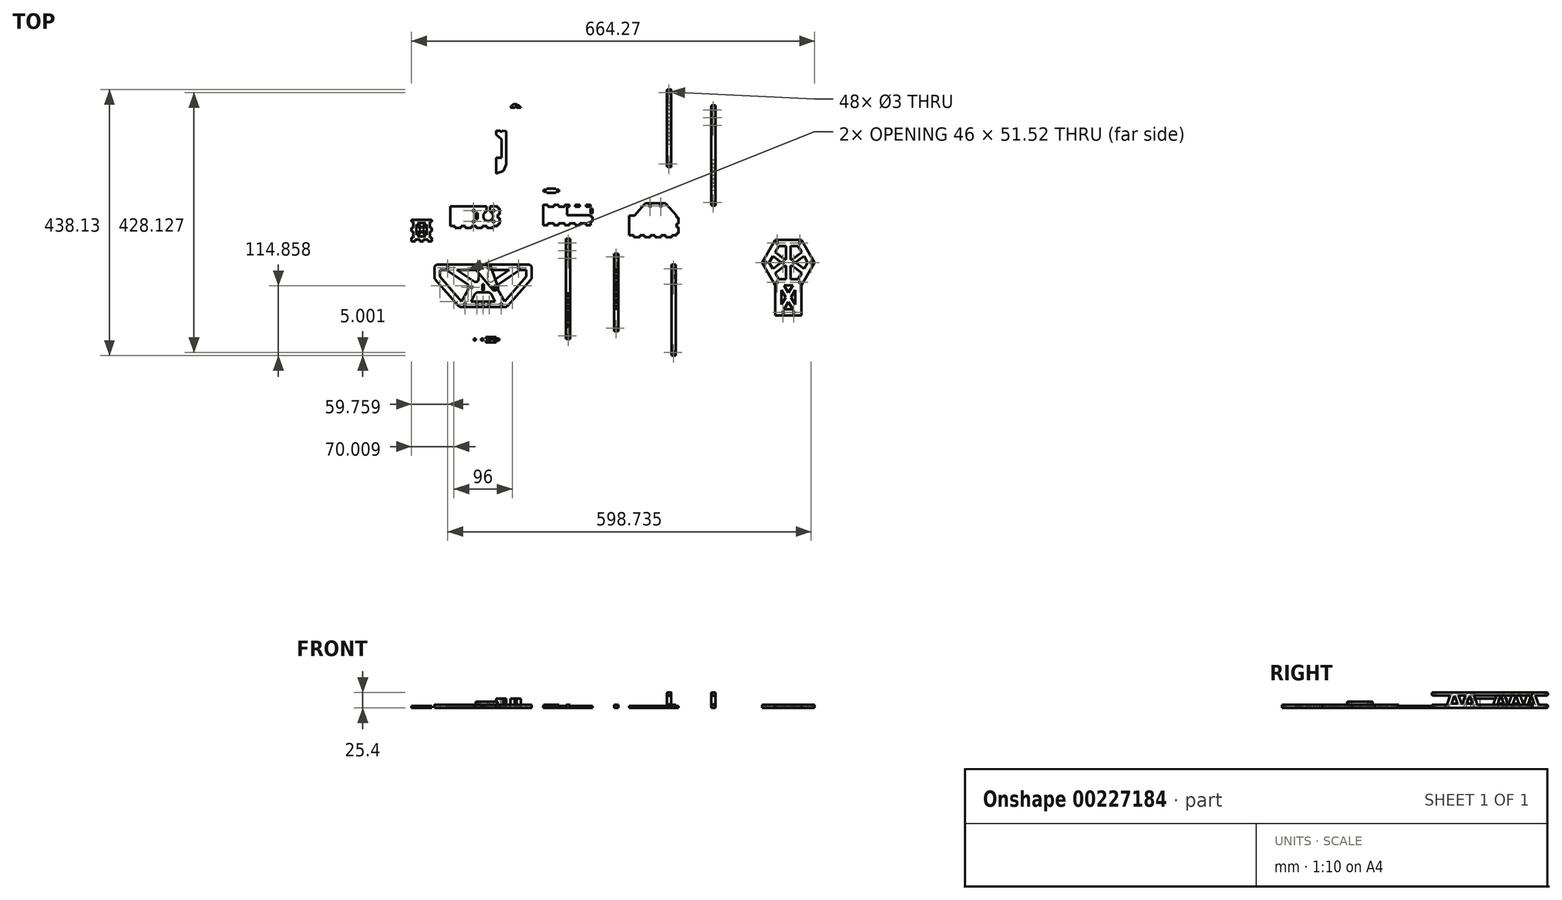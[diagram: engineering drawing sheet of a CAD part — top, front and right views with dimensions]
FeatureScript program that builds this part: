
annotation { "Feature Type Name" : "Feature", "Feature Type Description" : "" }
export const myFeature = defineFeature(function(context is Context, id is Id, definition is map)
    precondition{}
    {
        {
            var Q0;
            Q0=qCreatedBy(makeId("Top.planeOp"),FACE);
            var sketch = newSketch(context, id + "F0", { "sketchPlane" : qUnion([Q0])});
            skLineSegment(sketch, "E0.bottom", {"start": v(-33.91, 60.52) * mm, "end": v(-193.91, 60.52) * mm});
            skLineSegment(sketch, "E0.top", {"start": v(-33.91, 51.52) * mm, "end": v(-193.91, 51.52) * mm});
            skLineSegment(sketch, "E0.left", {"start": v(-33.91, 60.52) * mm, "end": v(-33.91, 51.52) * mm});
            skLineSegment(sketch, "E0.right", {"start": v(-193.91, 60.52) * mm, "end": v(-193.91, 51.52) * mm});
            skCircle(sketch, "E1", {"center": v(-172.16, 55.57) * mm, "radius": 1.5 * mm});
            skLineSegment(sketch, "E2.bottom", {"start": v(-88.91, 27.77) * mm, "end": v(-138.91, 27.77) * mm});
            skLineSegment(sketch, "E2.top", {"start": v(-88.91, 18.77) * mm, "end": v(-138.91, 18.77) * mm});
            skLineSegment(sketch, "E2.left", {"start": v(-88.91, 27.77) * mm, "end": v(-88.91, 18.77) * mm});
            skLineSegment(sketch, "E2.right", {"start": v(-138.91, 27.77) * mm, "end": v(-138.91, 18.77) * mm});
            skPoint(sketch, "E2.centerSnap0", {"position": v(-113.91, 51.52) * mm});
            skLineSegment(sketch, "E3", {"start": v(-121.41, 27.77) * mm, "end": v(-121.41, 51.52) * mm});
            skLineSegment(sketch, "E4", {"start": v(-113.91, 60.52) * mm, "end": v(-113.91, 18.77) * mm, "construction": true});
            skLineSegment(sketch, "E5.MirrorCS", {"start": v(-106.41, 27.77) * mm, "end": v(-106.41, 51.52) * mm});
            skPoint(sketch, "E6.centerSnap0", {"position": v(-138.91, 23.27) * mm});
            skCircle(sketch, "E7.MirrorC", {"center": v(-133.04, 23.27) * mm, "radius": 1.5 * mm});
            skCircle(sketch, "E8", {"center": v(-55.66, 55.57) * mm, "radius": 1.5 * mm});
            skLineSegment(sketch, "E9", {"start": v(-172.16, 55.57) * mm, "end": v(-55.66, 55.57) * mm, "construction": true});
            skLineSegment(sketch, "E10.bottom", {"start": v(-86.41, 0) * mm, "end": v(-141.41, 0) * mm});
            skLineSegment(sketch, "E10.top", {"start": v(-86.41, -9) * mm, "end": v(-141.41, -9) * mm});
            skLineSegment(sketch, "E10.left", {"start": v(-86.41, 0) * mm, "end": v(-86.41, -9) * mm});
            skLineSegment(sketch, "E10.right", {"start": v(-141.41, 0) * mm, "end": v(-141.41, -9) * mm});
            skLineSegment(sketch, "E11", {"start": v(-121.41, 18.77) * mm, "end": v(-121.41, 0) * mm});
            skLineSegment(sketch, "E12", {"start": v(-106.41, 18.77) * mm, "end": v(-106.41, 0) * mm});
            skCircle(sketch, "E13", {"center": v(-143.91, -4.5) * mm, "radius": 1.5 * mm});
            skPoint(sketch, "E13.centerSnap0", {"position": v(-141.41, -4.5) * mm});
            skLineSegment(sketch, "E14", {"start": v(-113.91, 18.77) * mm, "end": v(-113.91, -9) * mm});
            skCircle(sketch, "E15.MirrorC", {"center": v(-83.91, -4.5) * mm, "radius": 1.5 * mm});
            skLineSegment(sketch, "E16.bottom", {"start": v(22.73, 88.38) * mm, "end": v(29.73, 88.38) * mm});
            skLineSegment(sketch, "E16.top", {"start": v(22.73, -61.62) * mm, "end": v(29.73, -61.62) * mm});
            skLineSegment(sketch, "E16.left", {"start": v(22.73, 88.38) * mm, "end": v(22.73, -61.62) * mm});
            skLineSegment(sketch, "E16.right", {"start": v(29.73, 88.38) * mm, "end": v(29.73, -61.62) * mm});
            skCircle(sketch, "E17", {"center": v(26.23, 83.38) * mm, "radius": 1.5 * mm});
            skPoint(sketch, "E17.centerSnap0", {"position": v(26.23, 88.38) * mm});
            skLineSegment(sketch, "E18", {"start": v(22.73, 88.38) * mm, "end": v(22.73, 103.38) * mm});
            skLineSegment(sketch, "E19", {"start": v(22.73, 103.38) * mm, "end": v(29.73, 103.38) * mm});
            skLineSegment(sketch, "E20", {"start": v(29.73, 103.38) * mm, "end": v(29.73, 88.38) * mm});
            skCircle(sketch, "E21", {"center": v(26.23, 96.08) * mm, "radius": 1.5 * mm});
            skCircle(sketch, "E22", {"center": v(26.23, 70.68) * mm, "radius": 1.5 * mm});
            skLineSegment(sketch, "E23", {"start": v(26.23, 83.38) * mm, "end": v(26.23, 70.68) * mm});
            skCircle(sketch, "E24", {"center": v(26.23, -56.62) * mm, "radius": 1.5 * mm});
            skPoint(sketch, "E24.centerSnap0", {"position": v(26.23, -61.62) * mm});
            skLineSegment(sketch, "E25.bottom", {"start": v(101.72, 78.28) * mm, "end": v(108.72, 78.28) * mm});
            skLineSegment(sketch, "E25.top", {"start": v(101.72, -49.22) * mm, "end": v(108.72, -49.22) * mm});
            skLineSegment(sketch, "E25.left", {"start": v(101.72, 78.28) * mm, "end": v(101.72, -49.22) * mm});
            skLineSegment(sketch, "E25.right", {"start": v(108.72, 78.28) * mm, "end": v(108.72, -49.22) * mm});
            skCircle(sketch, "E26", {"center": v(105.22, 73.28) * mm, "radius": 1.5 * mm});
            skPoint(sketch, "E26.centerSnap0", {"position": v(105.22, 78.28) * mm});
            skCircle(sketch, "E27", {"center": v(105.22, -44.22) * mm, "radius": 1.5 * mm});
            skPoint(sketch, "E27.centerSnap0", {"position": v(105.22, -49.22) * mm});
            skLineSegment(sketch, "E28", {"start": v(-141.41, -9) * mm, "end": v(-193.91, 51.52) * mm});
            skLineSegment(sketch, "E29", {"start": v(-153.09, -9) * mm, "end": v(-141.41, -9) * mm});
            skLineSegment(sketch, "E30", {"start": v(-141.41, 0) * mm, "end": v(-149.22, 0) * mm});
            skLineSegment(sketch, "E31.MirrorCS", {"start": v(-86.41, -9) * mm, "end": v(-33.91, 51.52) * mm});
            skLineSegment(sketch, "E32.MirrorCS", {"start": v(-74.74, -9) * mm, "end": v(-86.41, -9) * mm});
            skLineSegment(sketch, "E33.MirrorCS", {"start": v(-86.41, 0) * mm, "end": v(-78.6, 0) * mm});
            skLineSegment(sketch, "E34", {"start": v(-88.91, 18.77) * mm, "end": v(-78.6, 0) * mm});
            skLineSegment(sketch, "E35", {"start": v(-99.18, 18.77) * mm, "end": v(-88.87, 0) * mm});
            skLineSegment(sketch, "E36.MirrorCS", {"start": v(-128.64, 18.77) * mm, "end": v(-138.95, 0) * mm});
            skLineSegment(sketch, "E37.MirrorCS", {"start": v(-138.91, 18.77) * mm, "end": v(-149.22, 0) * mm});
            skLineSegment(sketch, "E38", {"start": v(-42.91, 51.52) * mm, "end": v(-42.91, 41.14) * mm});
            skLineSegment(sketch, "E39", {"start": v(-33.91, 51.52) * mm, "end": v(-33.91, 37.39) * mm});
            skLineSegment(sketch, "E40", {"start": v(-33.91, 37.39) * mm, "end": v(-74.74, -9) * mm});
            skLineSegment(sketch, "E41.MirrorCS", {"start": v(-193.91, 37.39) * mm, "end": v(-153.09, -9) * mm});
            skLineSegment(sketch, "E42.MirrorCS", {"start": v(-193.91, 51.52) * mm, "end": v(-193.91, 37.39) * mm});
            skLineSegment(sketch, "E43.MirrorCS", {"start": v(-184.91, 51.52) * mm, "end": v(-184.91, 41.14) * mm});
            skLineSegment(sketch, "E44", {"start": v(-138.91, 27.77) * mm, "end": v(-174.34, 51.52) * mm});
            skLineSegment(sketch, "E45.MirrorCS", {"start": v(-88.91, 27.77) * mm, "end": v(-53.49, 51.52) * mm});
            skLineSegment(sketch, "E46", {"start": v(-149.22, 0) * mm, "end": v(-149.22, -9) * mm});
            skLineSegment(sketch, "E47", {"start": v(-138.6, -9) * mm, "end": v(-138.6, 0) * mm});
            skLineSegment(sketch, "E48", {"start": v(-138.6, 0) * mm, "end": v(-128.3, 18.77) * mm});
            skLineSegment(sketch, "E49.MirrorCS", {"start": v(-89.22, 0) * mm, "end": v(-99.53, 18.77) * mm});
            skLineSegment(sketch, "E50", {"start": v(-89.22, 0) * mm, "end": v(-89.22, -9) * mm});
            skLineSegment(sketch, "E51", {"start": v(-138.6, -9) * mm, "end": v(-123.35, 18.77) * mm});
            skLineSegment(sketch, "E52.MirrorCS", {"start": v(-89.22, -9) * mm, "end": v(-104.47, 18.77) * mm});
            skPoint(sketch, "E53.endSnap0", {"position": v(-156.62, 39.64) * mm});
            skLineSegment(sketch, "E54", {"start": v(-121.41, 27.77) * mm, "end": v(-156.84, 51.52) * mm});
            skLineSegment(sketch, "E55.MirrorCS", {"start": v(-106.41, 27.77) * mm, "end": v(-70.99, 51.52) * mm});
            skLineSegment(sketch, "E56.bottom", {"start": v(196.57, 45.9) * mm, "end": v(203.57, 45.9) * mm});
            skLineSegment(sketch, "E56.top", {"start": v(196.57, -89.1) * mm, "end": v(203.57, -89.1) * mm});
            skLineSegment(sketch, "E56.left", {"start": v(196.57, 45.9) * mm, "end": v(196.57, -89.1) * mm});
            skLineSegment(sketch, "E56.right", {"start": v(203.57, 45.9) * mm, "end": v(203.57, -89.1) * mm});
            skCircle(sketch, "E57", {"center": v(200.07, 40.9) * mm, "radius": 2.1 * mm});
            skPoint(sketch, "E57.centerSnap0", {"position": v(200.07, 45.9) * mm});
            skLineSegment(sketch, "E58", {"start": v(196.57, 45.9) * mm, "end": v(196.57, 60.9) * mm});
            skLineSegment(sketch, "E59", {"start": v(196.57, 60.9) * mm, "end": v(203.57, 60.9) * mm});
            skLineSegment(sketch, "E60", {"start": v(203.57, 60.9) * mm, "end": v(203.57, 45.9) * mm});
            skCircle(sketch, "E61", {"center": v(200.07, 53.6) * mm, "radius": 1.5 * mm});
            skCircle(sketch, "E62", {"center": v(200.07, 28.2) * mm, "radius": 1.5 * mm});
            skLineSegment(sketch, "E63", {"start": v(200.07, 40.9) * mm, "end": v(200.07, 28.2) * mm});
            skCircle(sketch, "E64", {"center": v(200.07, -84.1) * mm, "radius": 1.5 * mm});
            skPoint(sketch, "E64.centerSnap0", {"position": v(200.07, -89.1) * mm});
            skLineSegment(sketch, "E65.bottom", {"start": v(201.67, 42.5) * mm, "end": v(198.47, 42.5) * mm});
            skLineSegment(sketch, "E65.top", {"start": v(201.67, 39.3) * mm, "end": v(198.47, 39.3) * mm});
            skLineSegment(sketch, "E65.left", {"start": v(201.67, 42.5) * mm, "end": v(201.67, 39.3) * mm});
            skLineSegment(sketch, "E65.right", {"start": v(198.47, 42.5) * mm, "end": v(198.47, 39.3) * mm});
            skCircle(sketch, "E66", {"center": v(-105.16, 55.57) * mm, "radius": 1.5 * mm});
            skCircle(sketch, "E67.MirrorC", {"center": v(-122.66, 55.57) * mm, "radius": 1.5 * mm});
            skLineSegment(sketch, "E68", {"start": v(-127.38, 31.77) * mm, "end": v(-100.45, 31.77) * mm});
            skLineSegment(sketch, "E69.right", {"start": v(-137.03, 156.47) * mm, "end": v(-137.03, 124.47) * mm, "construction": true});
            skCircle(sketch, "E70", {"center": v(-96.53, 149.47) * mm, "radius": 1.5 * mm});
            skLineSegment(sketch, "E71", {"start": v(-137.03, 156.47) * mm, "end": v(-138.03, 156.47) * mm});
            skLineSegment(sketch, "E72", {"start": v(-138.03, 156.47) * mm, "end": v(-138.03, 124.47) * mm, "construction": true});
            skLineSegment(sketch, "E73", {"start": v(-138.03, 124.47) * mm, "end": v(-137.03, 124.47) * mm});
            skLineSegment(sketch, "E74.MirrorCS", {"start": v(-90.03, 156.47) * mm, "end": v(-90.03, 124.47) * mm});
            skLineSegment(sketch, "E75.MirrorCS", {"start": v(-90.03, 153.47) * mm, "end": v(-86.86, 153.47) * mm});
            skLineSegment(sketch, "E76.MirrorCS", {"start": v(-86.86, 153.47) * mm, "end": v(-86.86, 143.47) * mm});
            skLineSegment(sketch, "E77.MirrorCS", {"start": v(-86.86, 143.47) * mm, "end": v(-90.03, 143.47) * mm});
            skLineSegment(sketch, "E78.MirrorCS", {"start": v(-86.86, 137.47) * mm, "end": v(-90.03, 137.47) * mm});
            skLineSegment(sketch, "E79.MirrorCS", {"start": v(-86.86, 127.47) * mm, "end": v(-86.86, 137.47) * mm});
            skLineSegment(sketch, "E80.MirrorCS", {"start": v(-90.03, 127.47) * mm, "end": v(-86.86, 127.47) * mm});
            skCircle(sketch, "E81", {"center": v(-105.53, 140.47) * mm, "radius": 8 * mm});
            skLineSegment(sketch, "E82", {"start": v(-138.03, 156.47) * mm, "end": v(-168.03, 156.47) * mm});
            skLineSegment(sketch, "E83", {"start": v(-168.03, 156.47) * mm, "end": v(-168.03, 124.47) * mm});
            skLineSegment(sketch, "E84", {"start": v(-168.03, 124.47) * mm, "end": v(-138.03, 124.47) * mm});
            skLineSegment(sketch, "E85", {"start": v(-160.43, 124.47) * mm, "end": v(-160.43, 121.3) * mm});
            skLineSegment(sketch, "E86", {"start": v(-160.43, 121.3) * mm, "end": v(-150.43, 121.3) * mm});
            skLineSegment(sketch, "E87", {"start": v(-150.43, 121.3) * mm, "end": v(-150.43, 124.47) * mm});
            skLineSegment(sketch, "E88", {"start": v(-142.83, 124.47) * mm, "end": v(-142.83, 121.3) * mm});
            skLineSegment(sketch, "E89", {"start": v(-142.83, 121.3) * mm, "end": v(-132.83, 121.3) * mm});
            skLineSegment(sketch, "E90", {"start": v(-132.83, 121.3) * mm, "end": v(-132.83, 124.47) * mm});
            skLineSegment(sketch, "E91", {"start": v(-125.23, 124.47) * mm, "end": v(-125.23, 121.3) * mm});
            skLineSegment(sketch, "E92", {"start": v(-125.23, 121.3) * mm, "end": v(-115.23, 121.3) * mm});
            skLineSegment(sketch, "E93", {"start": v(-115.23, 121.3) * mm, "end": v(-115.23, 124.47) * mm});
            skLineSegment(sketch, "E94", {"start": v(-107.63, 124.47) * mm, "end": v(-107.63, 121.3) * mm});
            skLineSegment(sketch, "E95", {"start": v(-107.63, 121.3) * mm, "end": v(-97.63, 121.3) * mm});
            skLineSegment(sketch, "E96", {"start": v(-97.63, 121.3) * mm, "end": v(-97.63, 124.47) * mm});
            skCircle(sketch, "E97", {"center": v(-96.53, 149.47) * mm, "radius": 4 * mm, "construction": true});
            skCircle(sketch, "E98", {"center": v(-96.53, 131.57) * mm, "radius": 1.5 * mm});
            skCircle(sketch, "E99", {"center": v(-96.53, 131.57) * mm, "radius": 4 * mm, "construction": true});
            skLineSegment(sketch, "E100", {"start": v(-96.53, 153.47) * mm, "end": v(-96.53, 127.57) * mm, "construction": true});
            skCircle(sketch, "E101", {"center": v(-129.63, 149.47) * mm, "radius": 1.5 * mm});
            skCircle(sketch, "E102", {"center": v(-129.63, 149.47) * mm, "radius": 4 * mm, "construction": true});
            skLineSegment(sketch, "E103", {"start": v(-92.53, 149.47) * mm, "end": v(-133.63, 149.47) * mm, "construction": true});
            skCircle(sketch, "E104", {"center": v(-129.63, 131.57) * mm, "radius": 4 * mm, "construction": true});
            skCircle(sketch, "E105", {"center": v(-129.63, 131.57) * mm, "radius": 1.5 * mm});
            skLineSegment(sketch, "E106", {"start": v(-129.63, 153.47) * mm, "end": v(-129.63, 127.57) * mm, "construction": true});
            skLineSegment(sketch, "E107", {"start": v(-133.63, 131.57) * mm, "end": v(-92.53, 131.57) * mm, "construction": true});
            skCircle(sketch, "E108", {"center": v(-105.53, 140.47) * mm, "radius": 3 * mm});
            skLineSegment(sketch, "E109", {"start": v(-102.53, 140.47) * mm, "end": v(-102.53, 156.47) * mm});
            skLineSegment(sketch, "E110", {"start": v(-108.53, 140.47) * mm, "end": v(-108.53, 156.47) * mm});
            skLineSegment(sketch, "E111.bottom", {"start": v(63.2, 155.65) * mm, "end": v(-14.8, 155.65) * mm});
            skLineSegment(sketch, "E111.top", {"start": v(63.2, 128.65) * mm, "end": v(-14.8, 128.65) * mm});
            skLineSegment(sketch, "E111.left", {"start": v(63.2, 155.65) * mm, "end": v(63.2, 128.65) * mm});
            skPoint(sketch, "E111.middle", {"position": v(24.2, 142.15) * mm});
            skLineSegment(sketch, "E112.bottom", {"start": v(63.2, 152.65) * mm, "end": v(66.38, 152.65) * mm});
            skLineSegment(sketch, "E112.top", {"start": v(63.2, 145.15) * mm, "end": v(66.38, 145.15) * mm});
            skLineSegment(sketch, "E112.left", {"start": v(63.2, 152.65) * mm, "end": v(63.2, 145.15) * mm});
            skLineSegment(sketch, "E112.right", {"start": v(66.38, 152.65) * mm, "end": v(66.38, 145.15) * mm});
            skLineSegment(sketch, "E113", {"start": v(-14.8, 128.65) * mm, "end": v(-14.8, 125.47) * mm});
            skLineSegment(sketch, "E114", {"start": v(-14.8, 125.47) * mm, "end": v(-7.2, 125.47) * mm});
            skLineSegment(sketch, "E115", {"start": v(-7.2, 125.47) * mm, "end": v(-7.2, 128.65) * mm});
            skLineSegment(sketch, "E116", {"start": v(2.8, 128.65) * mm, "end": v(2.8, 125.49) * mm});
            skLineSegment(sketch, "E117", {"start": v(2.8, 125.49) * mm, "end": v(10.4, 125.49) * mm});
            skLineSegment(sketch, "E118", {"start": v(10.4, 125.49) * mm, "end": v(10.4, 128.66) * mm});
            skLineSegment(sketch, "E119", {"start": v(20.4, 128.65) * mm, "end": v(20.4, 125.49) * mm});
            skLineSegment(sketch, "E120", {"start": v(20.4, 125.49) * mm, "end": v(28, 125.49) * mm});
            skLineSegment(sketch, "E121", {"start": v(28, 125.49) * mm, "end": v(28, 128.65) * mm});
            skLineSegment(sketch, "E122", {"start": v(38, 128.65) * mm, "end": v(38, 125.47) * mm});
            skLineSegment(sketch, "E123", {"start": v(38, 125.47) * mm, "end": v(45.6, 125.47) * mm});
            skLineSegment(sketch, "E124", {"start": v(45.6, 125.47) * mm, "end": v(45.6, 128.65) * mm});
            skLineSegment(sketch, "E125", {"start": v(55.6, 128.65) * mm, "end": v(55.6, 125.47) * mm});
            skLineSegment(sketch, "E126", {"start": v(55.6, 125.47) * mm, "end": v(63.2, 125.47) * mm});
            skLineSegment(sketch, "E127", {"start": v(63.2, 125.47) * mm, "end": v(63.2, 128.65) * mm});
            skLineSegment(sketch, "E128.right", {"start": v(19.92, 142.9) * mm, "end": v(19.92, 149.9) * mm});
            skPoint(sketch, "E128.middle", {"position": v(4.7, 142.15) * mm});
            skLineSegment(sketch, "E129", {"start": v(24.2, 142.15) * mm, "end": v(-14.8, 142.15) * mm});
            skLineSegment(sketch, "E130", {"start": v(24.2, 142.15) * mm, "end": v(63.2, 142.15) * mm});
            skLineSegment(sketch, "E131", {"start": v(19.92, 142.9) * mm, "end": v(23.1, 142.9) * mm});
            skLineSegment(sketch, "E132", {"start": v(23.1, 142.9) * mm, "end": v(23.1, 149.9) * mm});
            skLineSegment(sketch, "E133", {"start": v(23.1, 149.9) * mm, "end": v(19.92, 149.9) * mm});
            skLineSegment(sketch, "E134.bottom", {"start": v(12.1, 142.9) * mm, "end": v(8.92, 142.9) * mm});
            skLineSegment(sketch, "E134.top", {"start": v(12.1, 149.9) * mm, "end": v(8.92, 149.9) * mm});
            skLineSegment(sketch, "E134.left", {"start": v(12.1, 142.9) * mm, "end": v(12.1, 149.9) * mm});
            skLineSegment(sketch, "E134.right", {"start": v(8.92, 142.9) * mm, "end": v(8.92, 149.9) * mm});
            skLineSegment(sketch, "E135", {"start": v(10.5, 142.9) * mm, "end": v(10.5, 149.9) * mm});
            skLineSegment(sketch, "E136", {"start": v(21.5, 142.9) * mm, "end": v(21.5, 149.9) * mm});
            skLineSegment(sketch, "E137", {"start": v(-14.8, 128.65) * mm, "end": v(-14.8, 155.65) * mm});
            skLineSegment(sketch, "E138", {"start": v(24.2, 125.49) * mm, "end": v(24.2, 162.54) * mm});
            skLineSegment(sketch, "E139.MirrorCS", {"start": v(-14.8, 158.82) * mm, "end": v(-7.2, 158.82) * mm});
            skLineSegment(sketch, "E140.MirrorCS", {"start": v(-14.8, 155.65) * mm, "end": v(-14.8, 158.82) * mm});
            skLineSegment(sketch, "E141.MirrorCS", {"start": v(-7.2, 158.82) * mm, "end": v(-7.2, 155.65) * mm});
            skLineSegment(sketch, "E142.MirrorCS", {"start": v(2.8, 158.8) * mm, "end": v(10.4, 158.8) * mm});
            skLineSegment(sketch, "E143.MirrorCS", {"start": v(2.8, 155.65) * mm, "end": v(2.8, 158.8) * mm});
            skLineSegment(sketch, "E144.MirrorCS", {"start": v(10.4, 158.8) * mm, "end": v(10.4, 155.63) * mm});
            skLineSegment(sketch, "E145.MirrorCS", {"start": v(20.4, 158.8) * mm, "end": v(28, 158.8) * mm});
            skLineSegment(sketch, "E146.MirrorCS", {"start": v(20.4, 155.65) * mm, "end": v(20.4, 158.8) * mm});
            skLineSegment(sketch, "E147.MirrorCS", {"start": v(28, 158.8) * mm, "end": v(28, 155.65) * mm});
            skLineSegment(sketch, "E148.MirrorCS", {"start": v(38, 158.82) * mm, "end": v(45.6, 158.82) * mm});
            skLineSegment(sketch, "E149.MirrorCS", {"start": v(38, 155.65) * mm, "end": v(38, 158.82) * mm});
            skLineSegment(sketch, "E150.MirrorCS", {"start": v(45.6, 158.82) * mm, "end": v(45.6, 155.65) * mm});
            skLineSegment(sketch, "E151.MirrorCS", {"start": v(55.6, 155.65) * mm, "end": v(55.6, 158.82) * mm});
            skLineSegment(sketch, "E152.MirrorCS", {"start": v(55.6, 158.82) * mm, "end": v(63.2, 158.82) * mm});
            skLineSegment(sketch, "E153.MirrorCS", {"start": v(63.2, 158.82) * mm, "end": v(63.2, 155.65) * mm});
            skLineSegment(sketch, "E154.MirrorCS", {"start": v(63.2, 139.15) * mm, "end": v(66.38, 139.15) * mm});
            skLineSegment(sketch, "E155.MirrorCS", {"start": v(66.38, 131.65) * mm, "end": v(66.38, 139.15) * mm});
            skLineSegment(sketch, "E156.MirrorCS", {"start": v(63.2, 131.65) * mm, "end": v(66.38, 131.65) * mm});
            skLineSegment(sketch, "E157.MirrorCS", {"start": v(204.72, 141.15) * mm, "end": v(204.72, 109.15) * mm});
            skLineSegment(sketch, "E158.MirrorCS", {"start": v(208.6, 146.33) * mm, "end": v(209.6, 146.33) * mm});
            skLineSegment(sketch, "E159.MirrorCS", {"start": v(207.9, 138.15) * mm, "end": v(207.9, 128.15) * mm});
            skLineSegment(sketch, "E160.MirrorCS", {"start": v(207.9, 112.15) * mm, "end": v(207.9, 122.15) * mm});
            skLineSegment(sketch, "E161", {"start": v(126.72, 141.15) * mm, "end": v(126.72, 109.15) * mm});
            skLineSegment(sketch, "E162", {"start": v(134.32, 109.15) * mm, "end": v(134.32, 105.97) * mm});
            skLineSegment(sketch, "E163", {"start": v(134.32, 105.97) * mm, "end": v(144.32, 105.97) * mm});
            skLineSegment(sketch, "E164", {"start": v(144.32, 105.97) * mm, "end": v(144.32, 109.15) * mm});
            skLineSegment(sketch, "E165", {"start": v(151.92, 109.15) * mm, "end": v(151.92, 105.97) * mm});
            skLineSegment(sketch, "E166", {"start": v(151.92, 105.97) * mm, "end": v(161.92, 105.97) * mm});
            skLineSegment(sketch, "E167", {"start": v(161.92, 105.97) * mm, "end": v(161.92, 109.15) * mm});
            skLineSegment(sketch, "E168", {"start": v(169.52, 109.15) * mm, "end": v(169.52, 105.97) * mm});
            skLineSegment(sketch, "E169", {"start": v(169.52, 105.97) * mm, "end": v(179.52, 105.97) * mm});
            skLineSegment(sketch, "E170", {"start": v(179.52, 105.97) * mm, "end": v(179.52, 109.15) * mm});
            skLineSegment(sketch, "E171", {"start": v(187.12, 109.15) * mm, "end": v(187.12, 105.97) * mm});
            skLineSegment(sketch, "E172", {"start": v(187.12, 105.97) * mm, "end": v(197.12, 105.97) * mm});
            skLineSegment(sketch, "E173", {"start": v(197.12, 105.97) * mm, "end": v(197.12, 109.15) * mm});
            skPoint(sketch, "E174.middle", {"position": v(170.6, 130.33) * mm});
            skLineSegment(sketch, "E175", {"start": v(126.72, 141.15) * mm, "end": v(204.72, 141.15) * mm});
            skLineSegment(sketch, "E176", {"start": v(126.72, 109.15) * mm, "end": v(204.72, 109.15) * mm});
            skLineSegment(sketch, "E177", {"start": v(207.9, 138.15) * mm, "end": v(204.72, 138.15) * mm});
            skLineSegment(sketch, "E178", {"start": v(207.9, 128.15) * mm, "end": v(204.72, 128.15) * mm});
            skLineSegment(sketch, "E179", {"start": v(207.9, 122.15) * mm, "end": v(204.72, 122.15) * mm});
            skLineSegment(sketch, "E180", {"start": v(207.9, 112.15) * mm, "end": v(204.72, 112.15) * mm});
            skLineSegment(sketch, "E181.bottom", {"start": v(126.72, 109.15) * mm, "end": v(108.72, 109.15) * mm});
            skLineSegment(sketch, "E181.top", {"start": v(126.72, 141.15) * mm, "end": v(108.72, 141.15) * mm});
            skLineSegment(sketch, "E181.left", {"start": v(126.72, 109.15) * mm, "end": v(126.72, 141.15) * mm});
            skLineSegment(sketch, "E181.right", {"start": v(108.72, 109.15) * mm, "end": v(108.72, 141.15) * mm});
            skLineSegment(sketch, "E182", {"start": v(108.72, 118.5) * mm, "end": v(126.72, 118.5) * mm});
            skLineSegment(sketch, "E183", {"start": v(108.72, 122.55) * mm, "end": v(126.72, 122.55) * mm});
            skLineSegment(sketch, "E184", {"start": v(126.72, 109.15) * mm, "end": v(108.72, 122.55) * mm});
            skLineSegment(sketch, "E185.bottom", {"start": v(186.35, 161.9) * mm, "end": v(153.8, 161.9) * mm});
            skLineSegment(sketch, "E185.top", {"start": v(186.35, 152.9) * mm, "end": v(153.8, 152.9) * mm});
            skLineSegment(sketch, "E185.left", {"start": v(186.35, 161.9) * mm, "end": v(186.35, 152.9) * mm});
            skLineSegment(sketch, "E185.right", {"start": v(153.8, 161.9) * mm, "end": v(153.8, 152.9) * mm});
            skPoint(sketch, "E185.middle", {"position": v(170.07, 157.4) * mm});
            skLineSegment(sketch, "E186", {"start": v(170.07, 152.9) * mm, "end": v(170.07, 141.15) * mm, "construction": true});
            skLineSegment(sketch, "E187", {"start": v(166.07, 141.15) * mm, "end": v(166.07, 152.9) * mm, "construction": true});
            skLineSegment(sketch, "E188.MirrorCS", {"start": v(174.07, 141.15) * mm, "end": v(174.07, 152.9) * mm, "construction": true});
            skCircle(sketch, "E189", {"center": v(178.82, 157.4) * mm, "radius": 1.5 * mm});
            skLineSegment(sketch, "E190", {"start": v(170.07, 157.4) * mm, "end": v(178.82, 157.4) * mm});
            skCircle(sketch, "E191.MirrorC", {"center": v(161.32, 157.4) * mm, "radius": 1.5 * mm});
            skLineSegment(sketch, "E192.MirrorCS", {"start": v(170.07, 157.4) * mm, "end": v(161.32, 157.4) * mm});
            skLineSegment(sketch, "E193", {"start": v(153.8, 152.9) * mm, "end": v(153.8, 141.15) * mm});
            skLineSegment(sketch, "E194", {"start": v(186.35, 152.9) * mm, "end": v(186.35, 141.15) * mm});
            skLineSegment(sketch, "E195", {"start": v(158.8, 152.9) * mm, "end": v(158.8, 141.15) * mm});
            skLineSegment(sketch, "E196.MirrorCS", {"start": v(181.35, 152.9) * mm, "end": v(181.35, 141.15) * mm});
            skLineSegment(sketch, "E197.bottom", {"start": v(199.72, 136.15) * mm, "end": v(131.72, 136.15) * mm});
            skLineSegment(sketch, "E197.top", {"start": v(199.72, 114.15) * mm, "end": v(131.72, 114.15) * mm});
            skLineSegment(sketch, "E197.left", {"start": v(199.72, 136.15) * mm, "end": v(199.72, 114.15) * mm});
            skLineSegment(sketch, "E197.right", {"start": v(131.72, 136.15) * mm, "end": v(131.72, 114.15) * mm});
            skPoint(sketch, "E197.middle", {"position": v(165.72, 125.15) * mm});
            skPoint(sketch, "E197.middle.positionSnap0", {"position": v(165.72, 141.15) * mm});
            skPoint(sketch, "E197.middle.positionSnap1", {"position": v(126.72, 125.15) * mm});
            skPoint(sketch, "E197.centerSnap0", {"position": v(165.72, 141.15) * mm});
            skPoint(sketch, "E197.centerSnap1", {"position": v(126.72, 125.15) * mm});
            skLineSegment(sketch, "E198", {"start": v(131.72, 136.15) * mm, "end": v(199.72, 114.15) * mm, "construction": true});
            skLineSegment(sketch, "E199", {"start": v(199.72, 136.15) * mm, "end": v(131.72, 114.15) * mm, "construction": true});
            skLineSegment(sketch, "E200", {"start": v(131.72, 115.73) * mm, "end": v(194.84, 136.15) * mm});
            skLineSegment(sketch, "E201", {"start": v(136.59, 114.15) * mm, "end": v(199.72, 134.57) * mm});
            skLineSegment(sketch, "E202", {"start": v(131.72, 134.57) * mm, "end": v(194.84, 114.15) * mm});
            skLineSegment(sketch, "E203", {"start": v(136.59, 136.15) * mm, "end": v(199.72, 115.73) * mm});
            skLineSegment(sketch, "E204.bottom", {"start": v(-201.6, 134.27) * mm, "end": v(-228.6, 134.27) * mm});
            skLineSegment(sketch, "E204.top", {"start": v(-201.6, 102.27) * mm, "end": v(-228.6, 102.27) * mm});
            skLineSegment(sketch, "E204.left", {"start": v(-201.6, 134.27) * mm, "end": v(-201.6, 102.27) * mm});
            skLineSegment(sketch, "E204.right", {"start": v(-228.6, 134.27) * mm, "end": v(-228.6, 102.27) * mm});
            skPoint(sketch, "E204.middle", {"position": v(-215.1, 118.27) * mm});
            skLineSegment(sketch, "E205", {"start": v(-215.1, 134.27) * mm, "end": v(-215.1, 102.27) * mm, "construction": true});
            skLineSegment(sketch, "E206", {"start": v(-218.1, 102.27) * mm, "end": v(-218.1, 99.1) * mm});
            skLineSegment(sketch, "E207", {"start": v(-218.1, 99.1) * mm, "end": v(-212.1, 99.1) * mm});
            skLineSegment(sketch, "E208", {"start": v(-212.1, 99.1) * mm, "end": v(-212.1, 102.27) * mm});
            skLineSegment(sketch, "E209", {"start": v(-204.6, 99.1) * mm, "end": v(-204.6, 102.27) * mm});
            skLineSegment(sketch, "E210", {"start": v(-201.6, 121.27) * mm, "end": v(-198.3, 121.27) * mm});
            skLineSegment(sketch, "E211", {"start": v(-198.3, 121.27) * mm, "end": v(-198.3, 115.27) * mm});
            skLineSegment(sketch, "E212", {"start": v(-198.3, 115.27) * mm, "end": v(-201.6, 115.27) * mm});
            skLineSegment(sketch, "E213", {"start": v(-201.6, 134.27) * mm, "end": v(-198.3, 134.27) * mm});
            skLineSegment(sketch, "E214", {"start": v(-198.3, 134.27) * mm, "end": v(-198.3, 131.27) * mm});
            skLineSegment(sketch, "E215", {"start": v(-198.3, 131.27) * mm, "end": v(-201.6, 131.27) * mm});
            skLineSegment(sketch, "E216", {"start": v(-228.6, 118.27) * mm, "end": v(-201.6, 118.27) * mm, "construction": true});
            skLineSegment(sketch, "E217.MirrorCS", {"start": v(-198.3, 105.27) * mm, "end": v(-201.6, 105.27) * mm});
            skLineSegment(sketch, "E218.MirrorCS", {"start": v(-198.3, 102.27) * mm, "end": v(-198.3, 105.27) * mm});
            skLineSegment(sketch, "E219.MirrorCS", {"start": v(-201.6, 102.27) * mm, "end": v(-198.3, 102.27) * mm});
            skLineSegment(sketch, "E220.MirrorCS", {"start": v(-228.6, 134.27) * mm, "end": v(-231.92, 134.27) * mm});
            skLineSegment(sketch, "E221.MirrorCS", {"start": v(-231.92, 131.27) * mm, "end": v(-228.6, 131.27) * mm});
            skLineSegment(sketch, "E222.MirrorCS", {"start": v(-231.92, 134.27) * mm, "end": v(-231.92, 131.27) * mm});
            skLineSegment(sketch, "E223.MirrorCS", {"start": v(-228.6, 121.27) * mm, "end": v(-231.92, 121.27) * mm});
            skLineSegment(sketch, "E224.MirrorCS", {"start": v(-231.92, 121.27) * mm, "end": v(-231.92, 115.27) * mm});
            skLineSegment(sketch, "E225.MirrorCS", {"start": v(-231.92, 115.27) * mm, "end": v(-228.6, 115.27) * mm});
            skLineSegment(sketch, "E226.MirrorCS", {"start": v(-231.92, 105.27) * mm, "end": v(-228.6, 105.27) * mm});
            skLineSegment(sketch, "E227.MirrorCS", {"start": v(-228.6, 102.27) * mm, "end": v(-231.92, 102.27) * mm});
            skLineSegment(sketch, "E228.MirrorCS", {"start": v(-231.92, 102.27) * mm, "end": v(-231.92, 105.27) * mm});
            skLineSegment(sketch, "E229", {"start": v(-204.6, 99.1) * mm, "end": v(-198.3, 99.1) * mm});
            skLineSegment(sketch, "E230", {"start": v(-198.3, 99.1) * mm, "end": v(-198.3, 102.27) * mm});
            skLineSegment(sketch, "E231.MirrorCS", {"start": v(-225.6, 99.1) * mm, "end": v(-225.6, 102.27) * mm});
            skLineSegment(sketch, "E232.MirrorCS", {"start": v(-225.6, 99.1) * mm, "end": v(-231.92, 99.1) * mm});
            skLineSegment(sketch, "E233.MirrorCS", {"start": v(-231.92, 99.1) * mm, "end": v(-231.92, 102.27) * mm});
            skLineSegment(sketch, "E234.bottom", {"start": v(-206.6, 129.27) * mm, "end": v(-223.6, 129.27) * mm});
            skLineSegment(sketch, "E234.top", {"start": v(-206.6, 107.27) * mm, "end": v(-223.6, 107.27) * mm});
            skLineSegment(sketch, "E234.left", {"start": v(-206.6, 129.27) * mm, "end": v(-206.6, 107.27) * mm});
            skLineSegment(sketch, "E234.right", {"start": v(-223.6, 129.27) * mm, "end": v(-223.6, 107.27) * mm});
            skLineSegment(sketch, "E235", {"start": v(-223.6, 129.27) * mm, "end": v(-206.6, 107.27) * mm, "construction": true});
            skLineSegment(sketch, "E236", {"start": v(-221.71, 129.27) * mm, "end": v(-206.6, 109.72) * mm});
            skLineSegment(sketch, "E237", {"start": v(-223.6, 126.82) * mm, "end": v(-208.5, 107.27) * mm});
            skLineSegment(sketch, "E238", {"start": v(-223.6, 107.27) * mm, "end": v(-206.6, 129.27) * mm, "construction": true});
            skLineSegment(sketch, "E239", {"start": v(-223.6, 109.72) * mm, "end": v(-208.5, 129.27) * mm});
            skLineSegment(sketch, "E240", {"start": v(-221.71, 107.27) * mm, "end": v(-206.6, 126.82) * mm});
            skLineSegment(sketch, "E241.bottom", {"start": v(-98.91, 84.52) * mm, "end": v(-128.91, 84.52) * mm});
            skLineSegment(sketch, "E241.top", {"start": v(-98.91, 75.52) * mm, "end": v(-128.91, 75.52) * mm});
            skLineSegment(sketch, "E241.left", {"start": v(-98.91, 84.52) * mm, "end": v(-98.91, 75.52) * mm});
            skLineSegment(sketch, "E241.right", {"start": v(-128.91, 84.52) * mm, "end": v(-128.91, 75.52) * mm});
            skPoint(sketch, "E241.middle", {"position": v(-113.91, 80.02) * mm});
            skLineSegment(sketch, "E242", {"start": v(-113.91, 60.52) * mm, "end": v(-113.91, 75.52) * mm});
            skPoint(sketch, "E243.centerSnap0", {"position": v(-128.91, 80.02) * mm});
            skCircle(sketch, "E244", {"center": v(-122.66, 80.02) * mm, "radius": 1.5 * mm});
            skCircle(sketch, "E245.MirrorC", {"center": v(-105.16, 80.02) * mm, "radius": 1.5 * mm});
            skLineSegment(sketch, "E246", {"start": v(-128.91, 84.52) * mm, "end": v(-144.39, 60.52) * mm});
            skLineSegment(sketch, "E247", {"start": v(-124, 75.52) * mm, "end": v(-133.68, 60.52) * mm});
            skLineSegment(sketch, "E248.MirrorCS", {"start": v(-103.82, 75.52) * mm, "end": v(-94.14, 60.52) * mm});
            skLineSegment(sketch, "E249.MirrorCS", {"start": v(-98.91, 84.52) * mm, "end": v(-83.43, 60.52) * mm});
            skCircle(sketch, "E250", {"center": v(-94.79, 23.27) * mm, "radius": 2.25 * mm});
            skLineSegment(sketch, "E251", {"start": v(158.8, 152.9) * mm, "end": v(181.35, 141.15) * mm});
            skLineSegment(sketch, "E252", {"start": v(158.8, 141.15) * mm, "end": v(181.35, 152.9) * mm, "construction": true});
            skLineSegment(sketch, "E253", {"start": v(158.8, 151.2) * mm, "end": v(178.1, 141.15) * mm});
            skLineSegment(sketch, "E254", {"start": v(162.04, 152.9) * mm, "end": v(181.35, 142.84) * mm});
            skLineSegment(sketch, "E255", {"start": v(158.8, 142.84) * mm, "end": v(178.1, 152.9) * mm});
            skLineSegment(sketch, "E256", {"start": v(162.04, 141.15) * mm, "end": v(181.35, 151.2) * mm});
            skPoint(sketch, "E257.middle", {"position": v(-118.95, 23.27) * mm});
            skLineSegment(sketch, "E258.bottom", {"start": v(-126.02, -58.38) * mm, "end": v(-92.36, -58.38) * mm});
            skLineSegment(sketch, "E258.top", {"start": v(-126.02, -67.38) * mm, "end": v(-92.36, -67.38) * mm});
            skLineSegment(sketch, "E258.left", {"start": v(-126.02, -58.38) * mm, "end": v(-126.02, -67.38) * mm});
            skLineSegment(sketch, "E258.right", {"start": v(-92.36, -58.38) * mm, "end": v(-92.36, -67.38) * mm});
            skLineSegment(sketch, "E259", {"start": v(-92.36, -61.38) * mm, "end": v(-87.28, -61.38) * mm});
            skLineSegment(sketch, "E260", {"start": v(-87.28, -61.38) * mm, "end": v(-87.28, -64.38) * mm});
            skLineSegment(sketch, "E261", {"start": v(-87.28, -64.38) * mm, "end": v(-92.36, -64.38) * mm});
            skLineSegment(sketch, "E262", {"start": v(-126.02, -61.38) * mm, "end": v(-129.2, -61.38) * mm});
            skLineSegment(sketch, "E263", {"start": v(-129.2, -61.38) * mm, "end": v(-129.2, -64.38) * mm});
            skLineSegment(sketch, "E264", {"start": v(-129.2, -64.38) * mm, "end": v(-126.02, -64.38) * mm});
            skPoint(sketch, "E265.middle.positionSnap0", {"position": v(-168.03, 140.47) * mm});
            skPoint(sketch, "E265.centerSnap0", {"position": v(-168.03, 140.47) * mm});
            skLineSegment(sketch, "E266", {"start": v(-90.03, 156.47) * mm, "end": v(-137.03, 156.47) * mm});
            skLineSegment(sketch, "E267", {"start": v(-90.03, 124.47) * mm, "end": v(-137.03, 124.47) * mm});
            skLineSegment(sketch, "E268.bottom", {"start": v(-112.41, 28.35) * mm, "end": v(-115.41, 28.35) * mm});
            skLineSegment(sketch, "E268.top", {"start": v(-112.41, 23.27) * mm, "end": v(-115.41, 23.27) * mm});
            skLineSegment(sketch, "E268.left", {"start": v(-112.41, 28.35) * mm, "end": v(-112.41, 23.27) * mm});
            skLineSegment(sketch, "E268.right", {"start": v(-115.41, 28.35) * mm, "end": v(-115.41, 23.27) * mm});
            skPoint(sketch, "E268.middle", {"position": v(-113.91, 25.8) * mm});
            skLineSegment(sketch, "E269.MirrorCS", {"start": v(-112.41, 18.19) * mm, "end": v(-115.41, 18.19) * mm});
            skLineSegment(sketch, "E270", {"start": v(-125.55, 14.77) * mm, "end": v(-102.27, 14.77) * mm});
            skLineSegment(sketch, "E271", {"start": v(-168.03, 140.47) * mm, "end": v(-90.03, 140.47) * mm, "construction": true});
            skPoint(sketch, "E272.middle", {"position": v(-127.84, 144.26) * mm});
            skLineSegment(sketch, "E273", {"start": v(-115.41, 23.27) * mm, "end": v(-115.41, 18.19) * mm});
            skLineSegment(sketch, "E274", {"start": v(-112.41, 23.27) * mm, "end": v(-112.41, 18.19) * mm});
            skLineSegment(sketch, "E275.bottom", {"start": v(-123.14, 145.55) * mm, "end": v(-126.14, 145.55) * mm});
            skLineSegment(sketch, "E275.top", {"start": v(-123.14, 135.4) * mm, "end": v(-126.14, 135.4) * mm});
            skLineSegment(sketch, "E275.left", {"start": v(-123.14, 145.55) * mm, "end": v(-123.14, 135.4) * mm});
            skLineSegment(sketch, "E275.right", {"start": v(-126.14, 145.55) * mm, "end": v(-126.14, 135.4) * mm});
            skPoint(sketch, "E275.middle", {"position": v(-124.64, 140.47) * mm});
            skLineSegment(sketch, "E276.bottom", {"start": v(27.73, 43.38) * mm, "end": v(24.73, 43.38) * mm});
            skLineSegment(sketch, "E276.top", {"start": v(27.73, 38.3) * mm, "end": v(24.73, 38.3) * mm});
            skLineSegment(sketch, "E276.left", {"start": v(27.73, 43.38) * mm, "end": v(27.73, 38.3) * mm});
            skLineSegment(sketch, "E276.right", {"start": v(24.73, 43.38) * mm, "end": v(24.73, 38.3) * mm});
            skPoint(sketch, "E276.middle", {"position": v(26.23, 40.84) * mm});
            skLineSegment(sketch, "E277.bottom", {"start": v(-9.18, 185.71) * mm, "end": v(6.06, 185.71) * mm});
            skLineSegment(sketch, "E277.top", {"start": v(-9.18, 178.71) * mm, "end": v(6.06, 178.71) * mm});
            skLineSegment(sketch, "E277.left", {"start": v(-9.18, 185.71) * mm, "end": v(-9.18, 178.71) * mm});
            skLineSegment(sketch, "E277.right", {"start": v(6.06, 185.71) * mm, "end": v(6.06, 178.71) * mm});
            skLineSegment(sketch, "E278", {"start": v(6.06, 183.71) * mm, "end": v(11.14, 183.71) * mm});
            skLineSegment(sketch, "E279", {"start": v(11.14, 183.71) * mm, "end": v(11.14, 180.71) * mm});
            skLineSegment(sketch, "E280", {"start": v(11.14, 180.71) * mm, "end": v(6.06, 180.71) * mm});
            skLineSegment(sketch, "E281", {"start": v(-1.56, 185.71) * mm, "end": v(-1.56, 178.71) * mm, "construction": true});
            skLineSegment(sketch, "E282.MirrorCS", {"start": v(-9.18, 183.71) * mm, "end": v(-14.26, 183.71) * mm});
            skLineSegment(sketch, "E283.MirrorCS", {"start": v(-14.26, 180.71) * mm, "end": v(-9.18, 180.71) * mm});
            skLineSegment(sketch, "E284.MirrorCS", {"start": v(-14.26, 183.71) * mm, "end": v(-14.26, 180.71) * mm});
            skLineSegment(sketch, "E285.bottom", {"start": v(24.73, 33.3) * mm, "end": v(27.73, 33.3) * mm});
            skLineSegment(sketch, "E285.top", {"start": v(24.73, 28.22) * mm, "end": v(27.73, 28.22) * mm});
            skLineSegment(sketch, "E285.left", {"start": v(24.73, 33.3) * mm, "end": v(24.73, 28.22) * mm});
            skLineSegment(sketch, "E285.right", {"start": v(27.73, 33.3) * mm, "end": v(27.73, 28.22) * mm});
            skLineSegment(sketch, "E286.bottom", {"start": v(24.73, 23.22) * mm, "end": v(27.73, 23.22) * mm});
            skLineSegment(sketch, "E286.top", {"start": v(24.73, 18.14) * mm, "end": v(27.73, 18.14) * mm});
            skLineSegment(sketch, "E286.left", {"start": v(24.73, 23.22) * mm, "end": v(24.73, 18.14) * mm});
            skLineSegment(sketch, "E286.right", {"start": v(27.73, 23.22) * mm, "end": v(27.73, 18.14) * mm});
            skLineSegment(sketch, "E287", {"start": v(26.23, 28.22) * mm, "end": v(26.23, 23.22) * mm});
            skLineSegment(sketch, "E288", {"start": v(26.23, 25.72) * mm, "end": v(29.73, 25.72) * mm});
            skLineSegment(sketch, "E289.MirrorCS", {"start": v(27.73, 8.06) * mm, "end": v(24.73, 8.06) * mm});
            skLineSegment(sketch, "E290.MirrorCS", {"start": v(24.73, 8.06) * mm, "end": v(24.73, 13.14) * mm});
            skLineSegment(sketch, "E291.MirrorCS", {"start": v(27.73, 13.14) * mm, "end": v(24.73, 13.14) * mm});
            skLineSegment(sketch, "E292.MirrorCS", {"start": v(27.73, 8.06) * mm, "end": v(27.73, 13.14) * mm});
            skLineSegment(sketch, "E293", {"start": v(26.23, 18.14) * mm, "end": v(26.23, 13.14) * mm});
            skLineSegment(sketch, "E294", {"start": v(26.23, 15.64) * mm, "end": v(29.73, 15.64) * mm});
            skLineSegment(sketch, "E295.MirrorCS", {"start": v(24.73, -2.02) * mm, "end": v(27.73, -2.02) * mm});
            skLineSegment(sketch, "E296.MirrorCS", {"start": v(24.73, -2.02) * mm, "end": v(24.73, 3.06) * mm});
            skLineSegment(sketch, "E297.MirrorCS", {"start": v(24.73, 3.06) * mm, "end": v(27.73, 3.06) * mm});
            skLineSegment(sketch, "E298.MirrorCS", {"start": v(27.73, -2.02) * mm, "end": v(27.73, 3.06) * mm});
            skLineSegment(sketch, "E299.MirrorCS", {"start": v(27.73, -7.02) * mm, "end": v(24.73, -7.02) * mm});
            skLineSegment(sketch, "E300.MirrorCS", {"start": v(24.73, -12.1) * mm, "end": v(24.73, -7.02) * mm});
            skLineSegment(sketch, "E301.MirrorCS", {"start": v(27.73, -12.1) * mm, "end": v(27.73, -7.02) * mm});
            skLineSegment(sketch, "E302.MirrorCS", {"start": v(27.73, -12.1) * mm, "end": v(24.73, -12.1) * mm});
            skLineSegment(sketch, "E303", {"start": v(26.23, -2.02) * mm, "end": v(26.23, -7.02) * mm});
            skLineSegment(sketch, "E304", {"start": v(26.23, -4.52) * mm, "end": v(29.73, -4.52) * mm});
            skLineSegment(sketch, "E305.MirrorCS", {"start": v(27.73, -17.1) * mm, "end": v(24.73, -17.1) * mm});
            skLineSegment(sketch, "E306.MirrorCS", {"start": v(24.73, -17.1) * mm, "end": v(24.73, -22.18) * mm});
            skLineSegment(sketch, "E307.MirrorCS", {"start": v(27.73, -17.1) * mm, "end": v(27.73, -22.18) * mm});
            skLineSegment(sketch, "E308.MirrorCS", {"start": v(27.73, -22.18) * mm, "end": v(24.73, -22.18) * mm});
            skLineSegment(sketch, "E309.MirrorCS", {"start": v(24.73, -27.18) * mm, "end": v(27.73, -27.18) * mm});
            skLineSegment(sketch, "E310.MirrorCS", {"start": v(24.73, -32.26) * mm, "end": v(24.73, -27.18) * mm});
            skLineSegment(sketch, "E311.MirrorCS", {"start": v(27.73, -32.26) * mm, "end": v(27.73, -27.18) * mm});
            skLineSegment(sketch, "E312.MirrorCS", {"start": v(24.73, -32.26) * mm, "end": v(27.73, -32.26) * mm});
            skLineSegment(sketch, "E313.MirrorCS", {"start": v(24.73, -37.26) * mm, "end": v(27.73, -37.26) * mm});
            skLineSegment(sketch, "E314.MirrorCS", {"start": v(27.73, -42.34) * mm, "end": v(27.73, -37.26) * mm});
            skLineSegment(sketch, "E315.MirrorCS", {"start": v(24.73, -42.34) * mm, "end": v(24.73, -37.26) * mm});
            skLineSegment(sketch, "E316.MirrorCS", {"start": v(24.73, -42.34) * mm, "end": v(27.73, -42.34) * mm});
            skLineSegment(sketch, "E317.bottom", {"start": v(106.72, 63.28) * mm, "end": v(103.72, 63.28) * mm});
            skLineSegment(sketch, "E317.top", {"start": v(106.72, 58.2) * mm, "end": v(103.72, 58.2) * mm});
            skLineSegment(sketch, "E317.left", {"start": v(106.72, 63.28) * mm, "end": v(106.72, 58.2) * mm});
            skLineSegment(sketch, "E317.right", {"start": v(103.72, 63.28) * mm, "end": v(103.72, 58.2) * mm});
            skPoint(sketch, "E317.middle", {"position": v(105.22, 60.74) * mm});
            skLineSegment(sketch, "E318.bottom", {"start": v(103.72, 53.2) * mm, "end": v(106.72, 53.2) * mm});
            skLineSegment(sketch, "E318.top", {"start": v(103.72, 48.12) * mm, "end": v(106.72, 48.12) * mm});
            skLineSegment(sketch, "E318.left", {"start": v(103.72, 53.2) * mm, "end": v(103.72, 48.12) * mm});
            skLineSegment(sketch, "E318.right", {"start": v(106.72, 53.2) * mm, "end": v(106.72, 48.12) * mm});
            skLineSegment(sketch, "E319.bottom", {"start": v(103.72, 43.12) * mm, "end": v(106.72, 43.12) * mm});
            skLineSegment(sketch, "E319.top", {"start": v(103.72, 38.04) * mm, "end": v(106.72, 38.04) * mm});
            skLineSegment(sketch, "E319.left", {"start": v(103.72, 43.12) * mm, "end": v(103.72, 38.04) * mm});
            skLineSegment(sketch, "E319.right", {"start": v(106.72, 43.12) * mm, "end": v(106.72, 38.04) * mm});
            skLineSegment(sketch, "E320.bottom", {"start": v(103.72, 33.04) * mm, "end": v(106.72, 33.04) * mm});
            skLineSegment(sketch, "E320.top", {"start": v(103.72, 27.96) * mm, "end": v(106.72, 27.96) * mm});
            skLineSegment(sketch, "E320.left", {"start": v(103.72, 33.04) * mm, "end": v(103.72, 27.96) * mm});
            skLineSegment(sketch, "E320.right", {"start": v(106.72, 33.04) * mm, "end": v(106.72, 27.96) * mm});
            skLineSegment(sketch, "E321.bottom", {"start": v(103.72, 22.96) * mm, "end": v(106.72, 22.96) * mm});
            skLineSegment(sketch, "E321.top", {"start": v(103.72, 17.88) * mm, "end": v(106.72, 17.88) * mm});
            skLineSegment(sketch, "E321.left", {"start": v(103.72, 22.96) * mm, "end": v(103.72, 17.88) * mm});
            skLineSegment(sketch, "E321.right", {"start": v(106.72, 22.96) * mm, "end": v(106.72, 17.88) * mm});
            skLineSegment(sketch, "E322", {"start": v(105.22, 27.96) * mm, "end": v(105.22, 22.96) * mm});
            skLineSegment(sketch, "E323", {"start": v(105.22, 25.46) * mm, "end": v(108.72, 25.46) * mm});
            skLineSegment(sketch, "E324.MirrorCS", {"start": v(103.72, 12.88) * mm, "end": v(106.72, 12.88) * mm});
            skLineSegment(sketch, "E325.MirrorCS", {"start": v(103.72, 7.8) * mm, "end": v(103.72, 12.88) * mm});
            skLineSegment(sketch, "E326.MirrorCS", {"start": v(103.72, 7.8) * mm, "end": v(106.72, 7.8) * mm});
            skLineSegment(sketch, "E327.MirrorCS", {"start": v(106.72, 7.8) * mm, "end": v(106.72, 12.88) * mm});
            skLineSegment(sketch, "E328.MirrorCS", {"start": v(103.72, -2.28) * mm, "end": v(106.72, -2.28) * mm});
            skLineSegment(sketch, "E329.MirrorCS", {"start": v(103.72, -2.28) * mm, "end": v(103.72, 2.8) * mm});
            skLineSegment(sketch, "E330.MirrorCS", {"start": v(103.72, 2.8) * mm, "end": v(106.72, 2.8) * mm});
            skLineSegment(sketch, "E331.MirrorCS", {"start": v(106.72, -2.28) * mm, "end": v(106.72, 2.8) * mm});
            skLineSegment(sketch, "E332.MirrorCS", {"start": v(106.72, -7.28) * mm, "end": v(103.72, -7.28) * mm});
            skLineSegment(sketch, "E333.MirrorCS", {"start": v(103.72, -12.36) * mm, "end": v(103.72, -7.28) * mm});
            skLineSegment(sketch, "E334.MirrorCS", {"start": v(106.72, -12.36) * mm, "end": v(103.72, -12.36) * mm});
            skLineSegment(sketch, "E335.MirrorCS", {"start": v(106.72, -12.36) * mm, "end": v(106.72, -7.28) * mm});
            skLineSegment(sketch, "E336.bottom", {"start": v(103.72, -17.36) * mm, "end": v(106.72, -17.36) * mm});
            skLineSegment(sketch, "E336.top", {"start": v(103.72, -22.44) * mm, "end": v(106.72, -22.44) * mm});
            skLineSegment(sketch, "E336.left", {"start": v(103.72, -17.36) * mm, "end": v(103.72, -22.44) * mm});
            skLineSegment(sketch, "E336.right", {"start": v(106.72, -17.36) * mm, "end": v(106.72, -22.44) * mm});
            skLineSegment(sketch, "E337.bottom", {"start": v(103.72, -27.44) * mm, "end": v(106.72, -27.44) * mm});
            skLineSegment(sketch, "E337.top", {"start": v(103.72, -32.52) * mm, "end": v(106.72, -32.52) * mm});
            skLineSegment(sketch, "E337.left", {"start": v(103.72, -27.44) * mm, "end": v(103.72, -32.52) * mm});
            skLineSegment(sketch, "E337.right", {"start": v(106.72, -27.44) * mm, "end": v(106.72, -32.52) * mm});
            skPoint(sketch, "E338.middle.positionSnap0", {"position": v(-126.02, -62.88) * mm});
            skPoint(sketch, "E338.centerSnap0", {"position": v(-126.02, -62.88) * mm});
            skLineSegment(sketch, "E339", {"start": v(-109.19, -58.38) * mm, "end": v(-109.19, -67.38) * mm});
            skLineSegment(sketch, "E340", {"start": v(186.35, 161.9) * mm, "end": v(204.72, 141.15) * mm});
            skLineSegment(sketch, "E341.MirrorCS", {"start": v(153.8, 161.9) * mm, "end": v(135.43, 141.15) * mm});
            skLineSegment(sketch, "E342.bottom", {"start": v(380.32, 63.96) * mm, "end": v(397.82, 63.96) * mm, "construction": true});
            skLineSegment(sketch, "E342.top", {"start": v(380.32, -18.03) * mm, "end": v(397.82, -18.03) * mm, "construction": true});
            skLineSegment(sketch, "E342.right", {"start": v(397.82, 63.96) * mm, "end": v(397.82, -18.03) * mm, "construction": true});
            skCircle(sketch, "E343", {"center": v(380.32, 63.96) * mm, "radius": 1.5 * mm});
            skCircle(sketch, "E344", {"center": v(397.82, 63.96) * mm, "radius": 1.5 * mm});
            skCircle(sketch, "E345", {"center": v(380.32, -18.03) * mm, "radius": 1.5 * mm});
            skCircle(sketch, "E346", {"center": v(397.82, -18.03) * mm, "radius": 1.5 * mm});
            skPoint(sketch, "E347.startSnap1", {"position": v(389.07, 63.96) * mm});
            skLineSegment(sketch, "E348.MirrorCS", {"start": v(351.57, 63.96) * mm, "end": v(370.32, 96.44) * mm, "construction": true});
            skLineSegment(sketch, "E349", {"start": v(345.8, 63.96) * mm, "end": v(351.57, 63.96) * mm, "construction": true});
            skLineSegment(sketch, "E350", {"start": v(345.8, 63.96) * mm, "end": v(367.44, 101.44) * mm});
            skLineSegment(sketch, "E351.MirrorCS", {"start": v(432.35, 63.96) * mm, "end": v(410.71, 101.44) * mm});
            skLineSegment(sketch, "E352.MirrorCS", {"start": v(345.8, 63.96) * mm, "end": v(367.44, 26.48) * mm});
            skLineSegment(sketch, "E353.MirrorCS", {"start": v(432.35, 63.96) * mm, "end": v(410.71, 26.48) * mm});
            skLineSegment(sketch, "E354", {"start": v(351.57, 63.96) * mm, "end": v(357.35, 63.96) * mm, "construction": true});
            skLineSegment(sketch, "E355", {"start": v(357.35, 63.96) * mm, "end": v(373.21, 91.44) * mm});
            skLineSegment(sketch, "E356.MirrorCS", {"start": v(420.8, 63.96) * mm, "end": v(404.94, 91.44) * mm});
            skLineSegment(sketch, "E357.MirrorCS", {"start": v(357.35, 63.96) * mm, "end": v(373.21, 36.48) * mm});
            skLineSegment(sketch, "E358.MirrorCS", {"start": v(420.8, 63.96) * mm, "end": v(404.94, 36.48) * mm});
            skCircle(sketch, "E359", {"center": v(351.57, 63.96) * mm, "radius": 1.5 * mm});
            skPoint(sketch, "E360.middle", {"position": v(389.07, 22.96) * mm});
            skLineSegment(sketch, "E361.bottom", {"start": v(401.32, 68.96) * mm, "end": v(376.82, 68.96) * mm});
            skLineSegment(sketch, "E361.top", {"start": v(401.32, 58.96) * mm, "end": v(376.82, 58.96) * mm});
            skLineSegment(sketch, "E361.left", {"start": v(401.32, 68.96) * mm, "end": v(401.32, 58.96) * mm});
            skLineSegment(sketch, "E361.right", {"start": v(376.82, 68.96) * mm, "end": v(376.82, 58.96) * mm});
            skLineSegment(sketch, "E362", {"start": v(376.82, 68.96) * mm, "end": v(365.28, 77.7) * mm, "construction": true});
            skLineSegment(sketch, "E363", {"start": v(383.04, 68.96) * mm, "end": v(367.17, 80.97) * mm});
            skLineSegment(sketch, "E364", {"start": v(376.82, 64.26) * mm, "end": v(363.39, 74.42) * mm});
            skLineSegment(sketch, "E365", {"start": v(389.07, 68.96) * mm, "end": v(389.07, 88.44) * mm, "construction": true});
            skLineSegment(sketch, "E366.MirrorCS", {"start": v(395.1, 68.96) * mm, "end": v(410.98, 80.97) * mm});
            skLineSegment(sketch, "E367.MirrorCS", {"start": v(401.32, 68.96) * mm, "end": v(412.87, 77.7) * mm, "construction": true});
            skLineSegment(sketch, "E368.MirrorCS", {"start": v(401.32, 64.26) * mm, "end": v(414.76, 74.42) * mm});
            skLineSegment(sketch, "E369.MirrorCS", {"start": v(401.32, 58.96) * mm, "end": v(412.87, 50.22) * mm, "construction": true});
            skLineSegment(sketch, "E370.MirrorCS", {"start": v(389.07, 58.96) * mm, "end": v(389.07, 39.48) * mm, "construction": true});
            skLineSegment(sketch, "E371.MirrorCS", {"start": v(376.82, 58.96) * mm, "end": v(365.28, 50.22) * mm, "construction": true});
            skLineSegment(sketch, "E372.MirrorCS", {"start": v(376.82, 63.66) * mm, "end": v(363.39, 53.5) * mm});
            skLineSegment(sketch, "E373.MirrorCS", {"start": v(383.04, 58.96) * mm, "end": v(367.17, 46.95) * mm});
            skLineSegment(sketch, "E374.MirrorCS", {"start": v(395.1, 58.96) * mm, "end": v(410.98, 46.95) * mm});
            skLineSegment(sketch, "E375.MirrorCS", {"start": v(401.32, 63.66) * mm, "end": v(414.76, 53.5) * mm});
            skLineSegment(sketch, "E376", {"start": v(373.21, 36.48) * mm, "end": v(404.94, 36.48) * mm});
            skLineSegment(sketch, "E377", {"start": v(367.44, 26.48) * mm, "end": v(410.71, 26.48) * mm});
            skLineSegment(sketch, "E378", {"start": v(367.44, 101.44) * mm, "end": v(410.71, 101.44) * mm});
            skLineSegment(sketch, "E379", {"start": v(373.21, 91.44) * mm, "end": v(404.94, 91.44) * mm});
            skLineSegment(sketch, "E380", {"start": v(380.32, 63.96) * mm, "end": v(380.32, -18.03) * mm, "construction": true});
            skLineSegment(sketch, "E381.bottom", {"start": v(410.71, -13.03) * mm, "end": v(367.44, -13.03) * mm});
            skLineSegment(sketch, "E381.top", {"start": v(410.71, -23.03) * mm, "end": v(367.44, -23.03) * mm});
            skLineSegment(sketch, "E381.left", {"start": v(410.71, -13.03) * mm, "end": v(410.71, -23.03) * mm});
            skLineSegment(sketch, "E381.right", {"start": v(367.44, -13.03) * mm, "end": v(367.44, -23.03) * mm});
            skPoint(sketch, "E381.middle", {"position": v(389.07, -18.03) * mm});
            skLineSegment(sketch, "E382", {"start": v(367.44, 26.48) * mm, "end": v(367.44, -13.03) * mm});
            skLineSegment(sketch, "E383", {"start": v(410.71, 26.48) * mm, "end": v(410.71, -13.03) * mm});
            skLineSegment(sketch, "E384", {"start": v(377.44, -13.03) * mm, "end": v(377.44, 26.48) * mm});
            skLineSegment(sketch, "E385.MirrorCS", {"start": v(400.71, -13.03) * mm, "end": v(400.71, 26.48) * mm});
            skLineSegment(sketch, "E386", {"start": v(377.44, 26.48) * mm, "end": v(400.71, -13.03) * mm, "construction": true});
            skLineSegment(sketch, "E387", {"start": v(377.44, 19.1) * mm, "end": v(396.36, -13.03) * mm});
            skLineSegment(sketch, "E388", {"start": v(381.79, 26.48) * mm, "end": v(400.71, -5.64) * mm});
            skLineSegment(sketch, "E389.MirrorCS", {"start": v(396.36, 26.48) * mm, "end": v(377.44, -5.64) * mm});
            skLineSegment(sketch, "E390.MirrorCS", {"start": v(400.71, 26.48) * mm, "end": v(377.44, -13.03) * mm, "construction": true});
            skLineSegment(sketch, "E391.MirrorCS", {"start": v(400.71, 19.1) * mm, "end": v(381.79, -13.03) * mm});
            skLineSegment(sketch, "E392.MirrorCS", {"start": v(426.57, 63.96) * mm, "end": v(407.82, 96.44) * mm, "construction": true});
            skCircle(sketch, "E393.MirrorC", {"center": v(426.57, 63.96) * mm, "radius": 1.5 * mm});
            skLineSegment(sketch, "E394.MirrorCS", {"start": v(351.57, 63.96) * mm, "end": v(370.32, 31.48) * mm, "construction": true});
            skLineSegment(sketch, "E395.MirrorCS", {"start": v(426.57, 63.96) * mm, "end": v(407.82, 31.48) * mm, "construction": true});
            skCircle(sketch, "E396", {"center": v(370.32, 96.44) * mm, "radius": 1.5 * mm});
            skCircle(sketch, "E397.MirrorC", {"center": v(407.82, 96.44) * mm, "radius": 1.5 * mm});
            skCircle(sketch, "E398.MirrorC", {"center": v(370.32, 31.48) * mm, "radius": 1.5 * mm});
            skCircle(sketch, "E399.MirrorC", {"center": v(407.82, 31.48) * mm, "radius": 1.5 * mm});
            skLineSegment(sketch, "E400", {"start": v(385.32, 68.96) * mm, "end": v(385.32, 91.44) * mm});
            skLineSegment(sketch, "E401.MirrorCS", {"start": v(392.82, 68.96) * mm, "end": v(392.82, 91.44) * mm});
            skLineSegment(sketch, "E402.MirrorCS", {"start": v(385.32, 58.96) * mm, "end": v(385.32, 36.48) * mm});
            skLineSegment(sketch, "E403.MirrorCS", {"start": v(392.82, 58.96) * mm, "end": v(392.82, 36.48) * mm});
            skLineSegment(sketch, "E404.bottom", {"start": v(94.98, 342.71) * mm, "end": v(101.98, 342.71) * mm});
            skLineSegment(sketch, "E404.top", {"start": v(94.98, 192.71) * mm, "end": v(101.98, 192.71) * mm});
            skCircle(sketch, "E405", {"center": v(98.48, 337.71) * mm, "radius": 1.5 * mm});
            skPoint(sketch, "E405.centerSnap0", {"position": v(98.48, 342.71) * mm});
            skLineSegment(sketch, "E406", {"start": v(94.98, 342.71) * mm, "end": v(94.98, 357.71) * mm});
            skLineSegment(sketch, "E407", {"start": v(94.98, 357.71) * mm, "end": v(101.98, 357.71) * mm});
            skLineSegment(sketch, "E408", {"start": v(101.98, 357.71) * mm, "end": v(101.98, 342.71) * mm});
            skCircle(sketch, "E409", {"center": v(98.48, 350.41) * mm, "radius": 1.5 * mm});
            skCircle(sketch, "E410", {"center": v(98.48, 325.01) * mm, "radius": 1.5 * mm});
            skLineSegment(sketch, "E411", {"start": v(98.48, 337.71) * mm, "end": v(98.48, 325.01) * mm});
            skCircle(sketch, "E412", {"center": v(98.48, 197.71) * mm, "radius": 1.5 * mm});
            skPoint(sketch, "E412.centerSnap0", {"position": v(98.48, 192.71) * mm});
            skLineSegment(sketch, "E413", {"start": v(101.98, 192.71) * mm, "end": v(101.98, 342.71) * mm});
            skLineSegment(sketch, "E414", {"start": v(94.98, 342.71) * mm, "end": v(94.98, 192.71) * mm});
            skLineSegment(sketch, "E415", {"start": v(-60.74, 332.14) * mm, "end": v(-43.74, 332.14) * mm});
            skLineSegment(sketch, "E416", {"start": v(-60.74, 332.14) * mm, "end": v(-92.34, 281.14) * mm});
            skLineSegment(sketch, "E417", {"start": v(-43.74, 332.14) * mm, "end": v(-75.6, 280.72) * mm});
            skLineSegment(sketch, "E418", {"start": v(-92.34, 281.14) * mm, "end": v(-92.34, 274.84) * mm});
            skLineSegment(sketch, "E419", {"start": v(-75.6, 280.72) * mm, "end": v(-75.6, 225.72) * mm});
            skLineSegment(sketch, "E420", {"start": v(-75.6, 225.72) * mm, "end": v(-80.37, 214.7) * mm});
            skLineSegment(sketch, "E421", {"start": v(-80.37, 214.7) * mm, "end": v(-92.36, 210.84) * mm});
            skLineSegment(sketch, "E422", {"start": v(-92.36, 210.84) * mm, "end": v(-92.36, 228.84) * mm});
            skLineSegment(sketch, "E423", {"start": v(-92.34, 274.84) * mm, "end": v(-83.74, 274.84) * mm});
            skLineSegment(sketch, "E424", {"start": v(-83.74, 274.84) * mm, "end": v(-83.74, 228.84) * mm});
            skLineSegment(sketch, "E425", {"start": v(-83.74, 228.84) * mm, "end": v(-92.36, 228.84) * mm});
            skLineSegment(sketch, "E426", {"start": v(-92.34, 274.84) * mm, "end": v(-83.74, 266.84) * mm});
            skLineSegment(sketch, "E427", {"start": v(-92.36, 228.84) * mm, "end": v(-83.74, 236.86) * mm});
            skLineSegment(sketch, "E428", {"start": v(-92.34, 281.14) * mm, "end": v(-75.6, 280.72) * mm});
            skCircle(sketch, "E429", {"center": v(-83.97, 280.93) * mm, "radius": 1.5 * mm});
            skLineSegment(sketch, "E430", {"start": v(-68.77, 319.18) * mm, "end": v(-51.77, 319.18) * mm});
            skCircle(sketch, "E431", {"center": v(-60.27, 319.18) * mm, "radius": 1.5 * mm});
            skLineSegment(sketch, "E432", {"start": v(-83.97, 280.93) * mm, "end": v(-60.27, 280.93) * mm, "construction": true});
            skLineSegment(sketch, "E433", {"start": v(-60.27, 280.93) * mm, "end": v(-60.27, 319.18) * mm, "construction": true});
            skLineSegment(sketch, "E434", {"start": v(-83.97, 280.93) * mm, "end": v(-60.27, 319.18) * mm, "construction": true});
            skLineSegment(sketch, "E435", {"start": v(-51.2, 320.1) * mm, "end": v(-63.49, 327.71) * mm});
            skLineSegment(sketch, "E436.bottom", {"start": v(188.74, 349.03) * mm, "end": v(195.74, 349.03) * mm});
            skLineSegment(sketch, "E436.top", {"start": v(188.74, 221.53) * mm, "end": v(195.74, 221.53) * mm});
            skLineSegment(sketch, "E436.left", {"start": v(188.74, 349.03) * mm, "end": v(188.74, 221.53) * mm});
            skLineSegment(sketch, "E436.right", {"start": v(195.74, 349.03) * mm, "end": v(195.74, 221.53) * mm});
            skCircle(sketch, "E437", {"center": v(192.24, 344.03) * mm, "radius": 1.5 * mm});
            skPoint(sketch, "E437.centerSnap0", {"position": v(192.24, 349.03) * mm});
            skCircle(sketch, "E438", {"center": v(192.24, 226.53) * mm, "radius": 1.5 * mm});
            skPoint(sketch, "E438.centerSnap0", {"position": v(192.24, 221.53) * mm});
            skLineSegment(sketch, "E439.bottom", {"start": v(261.86, 307.93) * mm, "end": v(268.86, 307.93) * mm});
            skLineSegment(sketch, "E439.top", {"start": v(261.86, 157.93) * mm, "end": v(268.86, 157.93) * mm});
            skCircle(sketch, "E440", {"center": v(265.36, 302.93) * mm, "radius": 1.5 * mm});
            skPoint(sketch, "E440.centerSnap0", {"position": v(265.36, 307.93) * mm});
            skLineSegment(sketch, "E441", {"start": v(261.86, 307.93) * mm, "end": v(261.86, 322.93) * mm});
            skLineSegment(sketch, "E442", {"start": v(261.86, 322.93) * mm, "end": v(268.86, 322.93) * mm});
            skLineSegment(sketch, "E443", {"start": v(268.86, 322.93) * mm, "end": v(268.86, 307.93) * mm});
            skCircle(sketch, "E444", {"center": v(265.36, 315.63) * mm, "radius": 1.5 * mm});
            skCircle(sketch, "E445", {"center": v(265.36, 290.23) * mm, "radius": 1.5 * mm});
            skLineSegment(sketch, "E446", {"start": v(265.36, 302.93) * mm, "end": v(265.36, 290.23) * mm});
            skCircle(sketch, "E447", {"center": v(265.36, 162.93) * mm, "radius": 1.5 * mm});
            skPoint(sketch, "E447.centerSnap0", {"position": v(265.36, 157.93) * mm});
            skLineSegment(sketch, "E448", {"start": v(268.86, 157.93) * mm, "end": v(268.86, 307.93) * mm});
            skLineSegment(sketch, "E449", {"start": v(261.86, 307.93) * mm, "end": v(261.86, 157.93) * mm});
            skLineSegment(sketch, "E450", {"start": v(-92.36, 228.84) * mm, "end": v(-92.36, 236.86) * mm});
            skLineSegment(sketch, "E451", {"start": v(-92.36, 236.86) * mm, "end": v(-83.74, 236.86) * mm});
            skCircle(sketch, "E452", {"center": v(-103.91, -4.5) * mm, "radius": 1.5 * mm});
            skPoint(sketch, "E452.centerSnap0", {"position": v(-89.22, -4.5) * mm});
            skCircle(sketch, "E453.MirrorC", {"center": v(-123.91, -4.5) * mm, "radius": 1.5 * mm});
            skCircle(sketch, "E454", {"center": v(-113.91, -4.5) * mm, "radius": 1.5 * mm});
            skCircle(sketch, "E455", {"center": v(-109.19, -62.88) * mm, "radius": 1.75 * mm});
            skArc(sketch, "E456", {"start": v(-105.19, -64.63) * mm, "mid": v(-104.64, -62.88) * mm, "end": v(-105.19, -61.13) * mm});
            skLineSegment(sketch, "E457", {"start": v(-105.19, -61.13) * mm, "end": v(-109.19, -61.13) * mm, "construction": true});
            skLineSegment(sketch, "E458", {"start": v(-105.19, -64.63) * mm, "end": v(-109.19, -64.63) * mm, "construction": true});
            skLineSegment(sketch, "E459", {"start": v(-105.19, -61.13) * mm, "end": v(-101.69, -61.13) * mm});
            skLineSegment(sketch, "E460", {"start": v(-105.19, -64.63) * mm, "end": v(-101.69, -64.63) * mm});
            skArc(sketch, "E461", {"start": v(-101.69, -64.63) * mm, "mid": v(-101.14, -62.88) * mm, "end": v(-101.69, -61.13) * mm});
            skLineSegment(sketch, "E462", {"start": v(-101.69, -61.13) * mm, "end": v(-97.69, -61.13) * mm, "construction": true});
            skLineSegment(sketch, "E463", {"start": v(-101.69, -64.63) * mm, "end": v(-97.69, -64.63) * mm, "construction": true});
            skArc(sketch, "E464", {"start": v(-97.69, -64.63) * mm, "mid": v(-97.14, -62.88) * mm, "end": v(-97.69, -61.13) * mm});
            skLineSegment(sketch, "E465", {"start": v(-97.69, -61.13) * mm, "end": v(-94.19, -61.13) * mm});
            skLineSegment(sketch, "E466", {"start": v(-97.69, -64.63) * mm, "end": v(-94.19, -64.63) * mm});
            skArc(sketch, "E467", {"start": v(-94.19, -64.63) * mm, "mid": v(-93.64, -62.88) * mm, "end": v(-94.19, -61.13) * mm});
            skArc(sketch, "E468.MirrorCS", {"start": v(-113.19, -64.63) * mm, "mid": v(-113.74, -62.88) * mm, "end": v(-113.19, -61.13) * mm});
            skLineSegment(sketch, "E469.MirrorCS", {"start": v(-113.19, -61.13) * mm, "end": v(-116.69, -61.13) * mm});
            skLineSegment(sketch, "E470.MirrorCS", {"start": v(-113.19, -64.63) * mm, "end": v(-116.69, -64.63) * mm});
            skArc(sketch, "E471.MirrorCS", {"start": v(-116.69, -64.63) * mm, "mid": v(-117.24, -62.88) * mm, "end": v(-116.69, -61.13) * mm});
            skArc(sketch, "E472.MirrorCS", {"start": v(-120.69, -64.63) * mm, "mid": v(-121.24, -62.88) * mm, "end": v(-120.69, -61.13) * mm});
            skLineSegment(sketch, "E473.MirrorCS", {"start": v(-120.69, -64.63) * mm, "end": v(-124.19, -64.63) * mm});
            skArc(sketch, "E474.MirrorCS", {"start": v(-124.19, -64.63) * mm, "mid": v(-124.74, -62.88) * mm, "end": v(-124.19, -61.13) * mm});
            skLineSegment(sketch, "E475.MirrorCS", {"start": v(-120.69, -61.13) * mm, "end": v(-124.19, -61.13) * mm});
            skSolve(sketch);
        }
        {
            var Q0;
            {var subQ0=sQuery(id+"F0.wireOp",EDGE,"E3");var subQ1=sQuery(id+"F0.wireOp",EDGE,"E0.top");var subQ2=makeQuery(id+"F0.imprint","INTERSECT",VERTEX,{"derivedFrom":[subQ1,subQ0]});Q0=makeQuery(id+"F0.imprint","IMPRINT",FACE,{"disambiguationData":[TD([[makeQuery(id+"F0.imprint","IMPRINT",EDGE,{"disambiguationData":[TD([[subQ2,1.0]])],"derivedFrom":subQ1}),1.0]])]});}
            var Q1;
            {var subQ10=sQuery(id+"F0.wireOp",EDGE,"E2.left");Q1=makeQuery(id+"F0.imprint","IMPRINT",FACE,{"disambiguationData":[TD([[makeQuery(id+"F0.imprint","IMPRINT",EDGE,{"derivedFrom":subQ10}),-1.0]])]});}
            var Q2;
            {var subQ28=sQuery(id+"F0.wireOp",EDGE,"E16.bottom");Q2=makeQuery(id+"F0.imprint","IMPRINT",FACE,{"disambiguationData":[TD([[makeQuery(id+"F0.imprint","IMPRINT",EDGE,{"derivedFrom":subQ28}),-1.0]])]});}
            var Q3;
            Q3=makeQuery(id+"F0.imprint","IMPRINT",FACE,{"disambiguationData":[TD([[makeQuery(id+"F0.imprint","IMPRINT",EDGE,{"derivedFrom":sQuery(id+"F0.wireOp",EDGE,"E16.bottom")}),1.0]])]});
            var Q4;
            {var subQ6=sQuery(id+"F0.wireOp",EDGE,"E25.bottom");Q4=makeQuery(id+"F0.imprint","IMPRINT",FACE,{"disambiguationData":[TD([[makeQuery(id+"F0.imprint","IMPRINT",EDGE,{"derivedFrom":subQ6}),-1.0]])]});}
            var Q5;
            {var subQ1=sQuery(id+"F0.wireOp",EDGE,"E10.right");Q5=makeQuery(id+"F0.imprint","IMPRINT",FACE,{"disambiguationData":[TD([[makeQuery(id+"F0.imprint","IMPRINT",EDGE,{"derivedFrom":subQ1}),-1.0]])]});}
            var Q6;
            {var subQ1=sQuery(id+"F0.wireOp",EDGE,"E10.left");Q6=makeQuery(id+"F0.imprint","IMPRINT",FACE,{"disambiguationData":[TD([[makeQuery(id+"F0.imprint","IMPRINT",EDGE,{"derivedFrom":subQ1}),1.0]])]});}
            var Q7;
            {var subQ5=sQuery(id+"F0.wireOp",EDGE,"E0.left");Q7=makeQuery(id+"F0.imprint","IMPRINT",FACE,{"disambiguationData":[TD([[makeQuery(id+"F0.imprint","IMPRINT",EDGE,{"derivedFrom":subQ5}),-1.0]])]});}
            var Q8;
            {var subQ0=sQuery(id+"F0.wireOp",EDGE,"E30");Q8=makeQuery(id+"F0.imprint","IMPRINT",FACE,{"disambiguationData":[TD([[makeQuery(id+"F0.imprint","IMPRINT",EDGE,{"derivedFrom":subQ0}),-1.0]])]});}
            var Q9;
            {var subQ1=sQuery(id+"F0.wireOp",EDGE,"E33.MirrorCS");Q9=makeQuery(id+"F0.imprint","IMPRINT",FACE,{"disambiguationData":[TD([[makeQuery(id+"F0.imprint","IMPRINT",EDGE,{"derivedFrom":subQ1}),1.0]])]});}
            var Q10;
            {var subQ0=sQuery(id+"F0.wireOp",EDGE,"E10.left");Q10=makeQuery(id+"F0.imprint","IMPRINT",FACE,{"disambiguationData":[TD([[makeQuery(id+"F0.imprint","IMPRINT",EDGE,{"derivedFrom":subQ0}),-1.0]])]});}
            var Q11;
            {var subQ0=sQuery(id+"F0.wireOp",EDGE,"E10.right");Q11=makeQuery(id+"F0.imprint","IMPRINT",FACE,{"disambiguationData":[TD([[makeQuery(id+"F0.imprint","IMPRINT",EDGE,{"derivedFrom":subQ0}),1.0]])]});}
            var Q12;
            {var subQ3=sQuery(id+"F0.wireOp",EDGE,"E38");Q12=makeQuery(id+"F0.imprint","IMPRINT",FACE,{"disambiguationData":[TD([[makeQuery(id+"F0.imprint","IMPRINT",EDGE,{"derivedFrom":subQ3}),1.0]])]});}
            var Q13;
            {var subQ3=sQuery(id+"F0.wireOp",EDGE,"E43.MirrorCS");Q13=makeQuery(id+"F0.imprint","IMPRINT",FACE,{"disambiguationData":[TD([[makeQuery(id+"F0.imprint","IMPRINT",EDGE,{"derivedFrom":subQ3}),-1.0]])]});}
            var Q14;
            {var subQ0=sQuery(id+"F0.wireOp",EDGE,"E46");Q14=makeQuery(id+"F0.imprint","IMPRINT",FACE,{"disambiguationData":[TD([[makeQuery(id+"F0.imprint","IMPRINT",EDGE,{"derivedFrom":subQ0}),1.0]])]});}
            var Q15;
            {var subQ6=sQuery(id+"F0.wireOp",EDGE,"E32.MirrorCS");Q15=makeQuery(id+"F0.imprint","IMPRINT",FACE,{"disambiguationData":[TD([[makeQuery(id+"F0.imprint","IMPRINT",EDGE,{"derivedFrom":subQ6}),-1.0]])]});}
            var Q16;
            {var subQ0=sQuery(id+"F0.wireOp",EDGE,"E36.MirrorCS");Q16=makeQuery(id+"F0.imprint","IMPRINT",FACE,{"disambiguationData":[TD([[makeQuery(id+"F0.imprint","IMPRINT",EDGE,{"derivedFrom":subQ0}),1.0]])]});}
            var Q17;
            {var subQ0=sQuery(id+"F0.wireOp",EDGE,"E35");Q17=makeQuery(id+"F0.imprint","IMPRINT",FACE,{"disambiguationData":[TD([[makeQuery(id+"F0.imprint","IMPRINT",EDGE,{"derivedFrom":subQ0}),-1.0]])]});}
            var Q18;
            {var subQ0=sQuery(id+"F0.wireOp",EDGE,"E41.MirrorCS");Q18=makeQuery(id+"F0.imprint","IMPRINT",FACE,{"disambiguationData":[TD([[makeQuery(id+"F0.imprint","IMPRINT",EDGE,{"derivedFrom":subQ0}),1.0]])]});}
            var Q19;
            {var subQ0=sQuery(id+"F0.wireOp",EDGE,"E48");Q19=makeQuery(id+"F0.imprint","IMPRINT",FACE,{"disambiguationData":[TD([[makeQuery(id+"F0.imprint","IMPRINT",EDGE,{"derivedFrom":subQ0}),-1.0]])]});}
            var Q20;
            {var subQ4=sQuery(id+"F0.wireOp",EDGE,"E49.MirrorCS");Q20=makeQuery(id+"F0.imprint","IMPRINT",FACE,{"disambiguationData":[TD([[makeQuery(id+"F0.imprint","IMPRINT",EDGE,{"derivedFrom":subQ4}),1.0]])]});}
            var Q21;
            {var subQ0=sQuery(id+"F0.wireOp",EDGE,"E50");Q21=makeQuery(id+"F0.imprint","IMPRINT",FACE,{"disambiguationData":[TD([[makeQuery(id+"F0.imprint","IMPRINT",EDGE,{"derivedFrom":subQ0}),-1.0]])]});}
            var Q22;
            {var subQ0=sQuery(id+"F0.wireOp",EDGE,"E47");Q22=makeQuery(id+"F0.imprint","IMPRINT",FACE,{"disambiguationData":[TD([[makeQuery(id+"F0.imprint","IMPRINT",EDGE,{"derivedFrom":subQ0}),-1.0]])]});}
            var Q23;
            {var subQ4=sQuery(id+"F0.wireOp",EDGE,"E44");Q23=makeQuery(id+"F0.imprint","IMPRINT",FACE,{"disambiguationData":[TD([[makeQuery(id+"F0.imprint","IMPRINT",EDGE,{"derivedFrom":subQ4}),-1.0]])]});}
            var Q24;
            {var subQ4=sQuery(id+"F0.wireOp",EDGE,"E45.MirrorCS");Q24=makeQuery(id+"F0.imprint","IMPRINT",FACE,{"disambiguationData":[TD([[makeQuery(id+"F0.imprint","IMPRINT",EDGE,{"derivedFrom":subQ4}),1.0]])]});}
            var Q25;
            {var subQ0=sQuery(id+"F0.wireOp",EDGE,"E65.bottom");var subQ1=sQuery(id+"F0.wireOp",EDGE,"E57");var subQ2=makeQuery(id+"F0.imprint","INTERSECT",VERTEX,{"disambiguationData":[OD(0.0)],"derivedFrom":[subQ1,subQ0]});Q25=makeQuery(id+"F0.imprint","IMPRINT",FACE,{"disambiguationData":[TD([[makeQuery(id+"F0.imprint","IMPRINT",EDGE,{"disambiguationData":[TD([[subQ2,1.0]])],"derivedFrom":subQ1}),-1.0]])]});}
            var Q26;
            {var subQ0=sQuery(id+"F0.wireOp",EDGE,"E65.bottom");var subQ1=sQuery(id+"F0.wireOp",EDGE,"E57");var subQ2=makeQuery(id+"F0.imprint","INTERSECT",VERTEX,{"disambiguationData":[OD(1.0)],"derivedFrom":[subQ1,subQ0]});Q26=makeQuery(id+"F0.imprint","IMPRINT",FACE,{"disambiguationData":[TD([[makeQuery(id+"F0.imprint","IMPRINT",EDGE,{"disambiguationData":[TD([[subQ2,-1.0]])],"derivedFrom":subQ1}),-1.0]])]});}
            var Q27;
            {var subQ0=sQuery(id+"F0.wireOp",EDGE,"E65.bottom");var subQ1=sQuery(id+"F0.wireOp",EDGE,"E57");var subQ2=makeQuery(id+"F0.imprint","INTERSECT",VERTEX,{"disambiguationData":[OD(0.0)],"derivedFrom":[subQ1,subQ0]});Q27=makeQuery(id+"F0.imprint","IMPRINT",FACE,{"disambiguationData":[TD([[makeQuery(id+"F0.imprint","IMPRINT",EDGE,{"disambiguationData":[TD([[subQ2,-1.0]])],"derivedFrom":subQ1}),1.0]])]});}
            var Q28;
            {var subQ0=sQuery(id+"F0.wireOp",EDGE,"E65.right");var subQ1=sQuery(id+"F0.wireOp",EDGE,"E57");var subQ2=makeQuery(id+"F0.imprint","INTERSECT",VERTEX,{"disambiguationData":[OD(0.0)],"derivedFrom":[subQ1,subQ0]});Q28=makeQuery(id+"F0.imprint","IMPRINT",FACE,{"disambiguationData":[TD([[makeQuery(id+"F0.imprint","IMPRINT",EDGE,{"disambiguationData":[TD([[subQ2,-1.0]])],"derivedFrom":subQ1}),1.0]])]});}
            var Q29;
            Q29=makeQuery(id+"F0.imprint","IMPRINT",FACE,{"disambiguationData":[TD([[makeQuery(id+"F0.imprint","IMPRINT",EDGE,{"derivedFrom":sQuery(id+"F0.wireOp",EDGE,"E56.bottom")}),-1.0]])]});
            var Q30;
            {var subQ0=sQuery(id+"F0.wireOp",EDGE,"E65.right");var subQ1=sQuery(id+"F0.wireOp",EDGE,"E57");var subQ2=makeQuery(id+"F0.imprint","INTERSECT",VERTEX,{"disambiguationData":[OD(1.0)],"derivedFrom":[subQ1,subQ0]});Q30=makeQuery(id+"F0.imprint","IMPRINT",FACE,{"disambiguationData":[TD([[makeQuery(id+"F0.imprint","IMPRINT",EDGE,{"disambiguationData":[TD([[subQ2,-1.0]])],"derivedFrom":subQ1}),-1.0]])]});}
            var Q31;
            {var subQ0=sQuery(id+"F0.wireOp",EDGE,"E63");var subQ1=sQuery(id+"F0.wireOp",EDGE,"E57");var subQ2=makeQuery(id+"F0.imprint","INTERSECT",VERTEX,{"derivedFrom":[subQ1,subQ0]});Q31=makeQuery(id+"F0.imprint","IMPRINT",FACE,{"disambiguationData":[TD([[makeQuery(id+"F0.imprint","IMPRINT",EDGE,{"disambiguationData":[TD([[subQ2,-1.0]])],"derivedFrom":subQ1}),1.0]])]});}
            var Q32;
            {var subQ0=sQuery(id+"F0.wireOp",EDGE,"E65.top");var subQ1=sQuery(id+"F0.wireOp",EDGE,"E57");var subQ2=makeQuery(id+"F0.imprint","INTERSECT",VERTEX,{"disambiguationData":[OD(1.0)],"derivedFrom":[subQ1,subQ0]});Q32=makeQuery(id+"F0.imprint","IMPRINT",FACE,{"disambiguationData":[TD([[makeQuery(id+"F0.imprint","IMPRINT",EDGE,{"disambiguationData":[TD([[subQ2,-1.0]])],"derivedFrom":subQ1}),-1.0]])]});}
            var Q33;
            {var subQ0=sQuery(id+"F0.wireOp",EDGE,"E63");var subQ1=sQuery(id+"F0.wireOp",EDGE,"E57");var subQ2=makeQuery(id+"F0.imprint","INTERSECT",VERTEX,{"derivedFrom":[subQ1,subQ0]});Q33=makeQuery(id+"F0.imprint","IMPRINT",FACE,{"disambiguationData":[TD([[makeQuery(id+"F0.imprint","IMPRINT",EDGE,{"disambiguationData":[TD([[subQ2,1.0]])],"derivedFrom":subQ1}),1.0]])]});}
            var Q34;
            {var subQ0=sQuery(id+"F0.wireOp",EDGE,"E65.left");var subQ1=sQuery(id+"F0.wireOp",EDGE,"E57");var subQ2=makeQuery(id+"F0.imprint","INTERSECT",VERTEX,{"disambiguationData":[OD(0.0)],"derivedFrom":[subQ1,subQ0]});Q34=makeQuery(id+"F0.imprint","IMPRINT",FACE,{"disambiguationData":[TD([[makeQuery(id+"F0.imprint","IMPRINT",EDGE,{"disambiguationData":[TD([[subQ2,1.0]])],"derivedFrom":subQ1}),1.0]])]});}
            var Q35;
            Q35=makeQuery(id+"F0.imprint","IMPRINT",FACE,{"disambiguationData":[TD([[makeQuery(id+"F0.imprint","IMPRINT",EDGE,{"derivedFrom":sQuery(id+"F0.wireOp",EDGE,"E56.bottom")}),1.0]])]});
            var Q36;
            {var subQ0=sQuery(id+"F0.wireOp",EDGE,"E54");var subQ3=sQuery(id+"F0.wireOp",EDGE,"E68");var subQ5=makeQuery(id+"F0.imprint","INTERSECT",VERTEX,{"derivedFrom":[subQ0,subQ3]});Q36=makeQuery(id+"F0.imprint","IMPRINT",FACE,{"disambiguationData":[TD([[makeQuery(id+"F0.imprint","IMPRINT",EDGE,{"disambiguationData":[TD([[subQ5,-1.0]])],"derivedFrom":subQ3}),-1.0]])]});}
            var Q37;
            {var subQ0=sQuery(id+"F0.wireOp",EDGE,"E55.MirrorCS");var subQ3=sQuery(id+"F0.wireOp",EDGE,"E68");var subQ5=makeQuery(id+"F0.imprint","INTERSECT",VERTEX,{"derivedFrom":[subQ0,subQ3]});Q37=makeQuery(id+"F0.imprint","IMPRINT",FACE,{"disambiguationData":[TD([[makeQuery(id+"F0.imprint","IMPRINT",EDGE,{"disambiguationData":[TD([[subQ5,1.0]])],"derivedFrom":subQ3}),-1.0]])]});}
            var Q38;
            Q38=makeQuery(id+"F0.imprint","IMPRINT",FACE,{"disambiguationData":[TD([[makeQuery(id+"F0.imprint","IMPRINT",EDGE,{"derivedFrom":sQuery(id+"F0.wireOp",EDGE,"E338.bottom")}),-1.0]])]});
            var Q39;
            {var subQ0=sQuery(id+"F0.wireOp",EDGE,"E259");Q39=makeQuery(id+"F0.imprint","IMPRINT",FACE,{"disambiguationData":[TD([[makeQuery(id+"F0.imprint","IMPRINT",EDGE,{"derivedFrom":subQ0}),-1.0]])]});}
            var Q40;
            {var subQ0=sQuery(id+"F0.wireOp",EDGE,"E262");Q40=makeQuery(id+"F0.imprint","IMPRINT",FACE,{"disambiguationData":[TD([[makeQuery(id+"F0.imprint","IMPRINT",EDGE,{"derivedFrom":subQ0}),1.0]])]});}
            var Q41;
            {var subQ6=sQuery(id+"F0.wireOp",EDGE,"E268.bottom");Q41=makeQuery(id+"F0.imprint","IMPRINT",FACE,{"disambiguationData":[TD([[makeQuery(id+"F0.imprint","IMPRINT",EDGE,{"derivedFrom":subQ6}),-1.0]])]});}
            var Q42;
            {var subQ7=sQuery(id+"F0.wireOp",EDGE,"E12");var subQ8=sQuery(id+"F0.wireOp",EDGE,"E2.top");var subQ9=makeQuery(id+"F0.imprint","INTERSECT",VERTEX,{"derivedFrom":[subQ8,subQ7]});Q42=makeQuery(id+"F0.imprint","IMPRINT",FACE,{"disambiguationData":[TD([[makeQuery(id+"F0.imprint","IMPRINT",EDGE,{"disambiguationData":[TD([[subQ9,-1.0]])],"derivedFrom":subQ8}),1.0]])]});}
            var Q43;
            {var subQ7=sQuery(id+"F0.wireOp",EDGE,"E11");var subQ8=sQuery(id+"F0.wireOp",EDGE,"E2.top");var subQ9=makeQuery(id+"F0.imprint","INTERSECT",VERTEX,{"derivedFrom":[subQ8,subQ7]});Q43=makeQuery(id+"F0.imprint","IMPRINT",FACE,{"disambiguationData":[TD([[makeQuery(id+"F0.imprint","IMPRINT",EDGE,{"disambiguationData":[TD([[subQ9,1.0]])],"derivedFrom":subQ8}),1.0]])]});}
            var Q44;
            {var subQ0=sQuery(id+"F0.wireOp",EDGE,"E12");var subQ1=sQuery(id+"F0.wireOp",EDGE,"E2.top");var subQ2=makeQuery(id+"F0.imprint","INTERSECT",VERTEX,{"derivedFrom":[subQ1,subQ0]});Q44=makeQuery(id+"F0.imprint","IMPRINT",FACE,{"disambiguationData":[TD([[makeQuery(id+"F0.imprint","IMPRINT",EDGE,{"disambiguationData":[TD([[subQ2,1.0]])],"derivedFrom":subQ1}),1.0]])]});}
            var Q45;
            {var subQ0=sQuery(id+"F0.wireOp",EDGE,"E11");var subQ1=sQuery(id+"F0.wireOp",EDGE,"E2.top");var subQ2=makeQuery(id+"F0.imprint","INTERSECT",VERTEX,{"derivedFrom":[subQ1,subQ0]});Q45=makeQuery(id+"F0.imprint","IMPRINT",FACE,{"disambiguationData":[TD([[makeQuery(id+"F0.imprint","IMPRINT",EDGE,{"disambiguationData":[TD([[subQ2,-1.0]])],"derivedFrom":subQ1}),1.0]])]});}
            var Q46;
            {var subQ5=sQuery(id+"F0.wireOp",EDGE,"E2.right");Q46=makeQuery(id+"F0.imprint","IMPRINT",FACE,{"disambiguationData":[TD([[makeQuery(id+"F0.imprint","IMPRINT",EDGE,{"derivedFrom":subQ5}),1.0]])]});}
            var Q47;
            {var subQ3=sQuery(id+"F0.wireOp",EDGE,"E277.bottom");Q47=makeQuery(id+"F0.imprint","IMPRINT",FACE,{"disambiguationData":[TD([[makeQuery(id+"F0.imprint","IMPRINT",EDGE,{"derivedFrom":subQ3}),-1.0]])]});}
            var Q48;
            {var subQ0=sQuery(id+"F0.wireOp",EDGE,"E278");Q48=makeQuery(id+"F0.imprint","IMPRINT",FACE,{"disambiguationData":[TD([[makeQuery(id+"F0.imprint","IMPRINT",EDGE,{"derivedFrom":subQ0}),-1.0]])]});}
            var Q49;
            {var subQ0=sQuery(id+"F0.wireOp",EDGE,"E282.MirrorCS");Q49=makeQuery(id+"F0.imprint","IMPRINT",FACE,{"disambiguationData":[TD([[makeQuery(id+"F0.imprint","IMPRINT",EDGE,{"derivedFrom":subQ0}),1.0]])]});}
            var Q50;
            {var subQ0=sQuery(id+"F0.wireOp",EDGE,"E286.right");Q50=makeQuery(id+"F0.imprint","IMPRINT",FACE,{"disambiguationData":[TD([[makeQuery(id+"F0.imprint","IMPRINT",EDGE,{"derivedFrom":subQ0}),1.0]])]});}
            var Q51;
            Q51=makeQuery(id+"F0.imprint","IMPRINT",FACE,{"disambiguationData":[TD([[makeQuery(id+"F0.imprint","IMPRINT",EDGE,{"derivedFrom":sQuery(id+"F0.wireOp",EDGE,"E276.bottom")}),1.0]])]});
            var Q52;
            Q52=makeQuery(id+"F0.imprint","IMPRINT",FACE,{"disambiguationData":[TD([[makeQuery(id+"F0.imprint","IMPRINT",EDGE,{"derivedFrom":sQuery(id+"F0.wireOp",EDGE,"E285.bottom")}),-1.0]])]});
            var Q53;
            {var subQ3=sQuery(id+"F0.wireOp",EDGE,"E286.left");Q53=makeQuery(id+"F0.imprint","IMPRINT",FACE,{"disambiguationData":[TD([[makeQuery(id+"F0.imprint","IMPRINT",EDGE,{"derivedFrom":subQ3}),1.0]])]});}
            var Q54;
            Q54=makeQuery(id+"F0.imprint","IMPRINT",FACE,{"disambiguationData":[TD([[makeQuery(id+"F0.imprint","IMPRINT",EDGE,{"derivedFrom":sQuery(id+"F0.wireOp",EDGE,"E337.bottom")}),-1.0]])]});
            var Q55;
            Q55=makeQuery(id+"F0.imprint","IMPRINT",FACE,{"disambiguationData":[TD([[makeQuery(id+"F0.imprint","IMPRINT",EDGE,{"derivedFrom":sQuery(id+"F0.wireOp",EDGE,"E336.bottom")}),-1.0]])]});
            var Q56;
            Q56=makeQuery(id+"F0.imprint","IMPRINT",FACE,{"disambiguationData":[TD([[makeQuery(id+"F0.imprint","IMPRINT",EDGE,{"derivedFrom":sQuery(id+"F0.wireOp",EDGE,"E350")}),-1.0]])]});
            var Q57;
            Q57=makeQuery(id+"F0.imprint","IMPRINT",FACE,{"disambiguationData":[TD([[makeQuery(id+"F0.imprint","IMPRINT",EDGE,{"derivedFrom":sQuery(id+"F0.wireOp",EDGE,"E345")}),-1.0]])]});
            var Q58;
            Q58=makeQuery(id+"F0.imprint","IMPRINT",FACE,{"disambiguationData":[TD([[makeQuery(id+"F0.imprint","IMPRINT",EDGE,{"derivedFrom":sQuery(id+"F0.wireOp",EDGE,"E343")}),-1.0]])]});
            var Q59;
            {var subQ0=sQuery(id+"F0.wireOp",EDGE,"E363");Q59=makeQuery(id+"F0.imprint","IMPRINT",FACE,{"disambiguationData":[TD([[makeQuery(id+"F0.imprint","IMPRINT",EDGE,{"derivedFrom":subQ0}),1.0]])]});}
            var Q60;
            {var subQ3=sQuery(id+"F0.wireOp",EDGE,"E374.MirrorCS");Q60=makeQuery(id+"F0.imprint","IMPRINT",FACE,{"disambiguationData":[TD([[makeQuery(id+"F0.imprint","IMPRINT",EDGE,{"derivedFrom":subQ3}),1.0]])]});}
            var Q61;
            {var subQ0=sQuery(id+"F0.wireOp",EDGE,"E366.MirrorCS");Q61=makeQuery(id+"F0.imprint","IMPRINT",FACE,{"disambiguationData":[TD([[makeQuery(id+"F0.imprint","IMPRINT",EDGE,{"derivedFrom":subQ0}),-1.0]])]});}
            var Q62;
            {var subQ0=sQuery(id+"F0.wireOp",EDGE,"E372.MirrorCS");Q62=makeQuery(id+"F0.imprint","IMPRINT",FACE,{"disambiguationData":[TD([[makeQuery(id+"F0.imprint","IMPRINT",EDGE,{"derivedFrom":subQ0}),1.0]])]});}
            var Q63;
            {var subQ4=sQuery(id+"F0.wireOp",EDGE,"E382");Q63=makeQuery(id+"F0.imprint","IMPRINT",FACE,{"disambiguationData":[TD([[makeQuery(id+"F0.imprint","IMPRINT",EDGE,{"derivedFrom":subQ4}),1.0]])]});}
            var Q64;
            {var subQ4=sQuery(id+"F0.wireOp",EDGE,"E383");Q64=makeQuery(id+"F0.imprint","IMPRINT",FACE,{"disambiguationData":[TD([[makeQuery(id+"F0.imprint","IMPRINT",EDGE,{"derivedFrom":subQ4}),-1.0]])]});}
            var Q65;
            {var subQ1=sQuery(id+"F0.wireOp",EDGE,"E377");var subQ7=sQuery(id+"F0.wireOp",EDGE,"E385.MirrorCS");var subQ8=makeQuery(id+"F0.imprint","INTERSECT",VERTEX,{"derivedFrom":[subQ1,subQ7]});Q65=makeQuery(id+"F0.imprint","IMPRINT",FACE,{"disambiguationData":[TD([[makeQuery(id+"F0.imprint","IMPRINT",EDGE,{"disambiguationData":[TD([[subQ8,1.0]])],"derivedFrom":subQ1}),-1.0]])]});}
            var Q66;
            {var subQ1=sQuery(id+"F0.wireOp",EDGE,"E381.bottom");var subQ5=sQuery(id+"F0.wireOp",EDGE,"E385.MirrorCS");var subQ6=makeQuery(id+"F0.imprint","INTERSECT",VERTEX,{"derivedFrom":[subQ1,subQ5]});Q66=makeQuery(id+"F0.imprint","IMPRINT",FACE,{"disambiguationData":[TD([[makeQuery(id+"F0.imprint","IMPRINT",EDGE,{"disambiguationData":[TD([[subQ6,-1.0]])],"derivedFrom":subQ1}),-1.0]])]});}
            var Q67;
            {var subQ0=sQuery(id+"F0.wireOp",EDGE,"E389.MirrorCS");var subQ1=sQuery(id+"F0.wireOp",EDGE,"E387");var subQ2=makeQuery(id+"F0.imprint","INTERSECT",VERTEX,{"derivedFrom":[subQ1,subQ0]});Q67=makeQuery(id+"F0.imprint","IMPRINT",FACE,{"disambiguationData":[TD([[makeQuery(id+"F0.imprint","IMPRINT",EDGE,{"disambiguationData":[TD([[subQ2,-1.0]])],"derivedFrom":subQ1}),1.0]])]});}
            var Q68;
            {var subQ1=sQuery(id+"F0.wireOp",EDGE,"E377");var subQ6=sQuery(id+"F0.wireOp",EDGE,"E384");var subQ9=makeQuery(id+"F0.imprint","INTERSECT",VERTEX,{"derivedFrom":[subQ1,subQ6]});Q68=makeQuery(id+"F0.imprint","IMPRINT",FACE,{"disambiguationData":[TD([[makeQuery(id+"F0.imprint","IMPRINT",EDGE,{"disambiguationData":[TD([[subQ9,-1.0]])],"derivedFrom":subQ1}),-1.0]])]});}
            var Q69;
            {var subQ1=sQuery(id+"F0.wireOp",EDGE,"E384");var subQ7=sQuery(id+"F0.wireOp",EDGE,"E381.bottom");var subQ8=makeQuery(id+"F0.imprint","INTERSECT",VERTEX,{"derivedFrom":[subQ7,subQ1]});Q69=makeQuery(id+"F0.imprint","IMPRINT",FACE,{"disambiguationData":[TD([[makeQuery(id+"F0.imprint","IMPRINT",EDGE,{"disambiguationData":[TD([[subQ8,1.0]])],"derivedFrom":subQ7}),-1.0]])]});}
            var Q70;
            {var subQ0=sQuery(id+"F0.wireOp",EDGE,"E400");Q70=makeQuery(id+"F0.imprint","IMPRINT",FACE,{"disambiguationData":[TD([[makeQuery(id+"F0.imprint","IMPRINT",EDGE,{"derivedFrom":subQ0}),-1.0]])]});}
            var Q71;
            {var subQ0=sQuery(id+"F0.wireOp",EDGE,"E402.MirrorCS");Q71=makeQuery(id+"F0.imprint","IMPRINT",FACE,{"disambiguationData":[TD([[makeQuery(id+"F0.imprint","IMPRINT",EDGE,{"derivedFrom":subQ0}),1.0]])]});}
            var Q72;
            Q72=makeQuery(id+"F0.imprint","IMPRINT",FACE,{"disambiguationData":[TD([[makeQuery(id+"F0.imprint","IMPRINT",EDGE,{"derivedFrom":sQuery(id+"F0.wireOp",EDGE,"E436.bottom")}),-1.0]])]});
            var Q73;
            Q73=makeQuery(id+"F0.imprint","IMPRINT",FACE,{"disambiguationData":[TD([[makeQuery(id+"F0.imprint","IMPRINT",EDGE,{"derivedFrom":sQuery(id+"F0.wireOp",EDGE,"E439.bottom")}),-1.0]])]});
            var Q74;
            Q74=makeQuery(id+"F0.imprint","IMPRINT",FACE,{"disambiguationData":[TD([[makeQuery(id+"F0.imprint","IMPRINT",EDGE,{"derivedFrom":sQuery(id+"F0.wireOp",EDGE,"E439.bottom")}),1.0]])]});
            var Q75;
            {var subQ5=sQuery(id+"F0.wireOp",EDGE,"E10.bottom");var subQ6=makeQuery(id+"F0.imprint","INTERSECT",VERTEX,{"derivedFrom":[subQ5,sQuery(id+"F0.wireOp",EDGE,"E11")]});Q75=makeQuery(id+"F0.imprint","IMPRINT",FACE,{"disambiguationData":[TD([[makeQuery(id+"F0.imprint","IMPRINT",EDGE,{"disambiguationData":[TD([[subQ6,1.0]])],"derivedFrom":subQ5}),1.0]])]});}
            var Q76;
            {var subQ3=sQuery(id+"F0.wireOp",EDGE,"E10.bottom");var subQ5=makeQuery(id+"F0.imprint","INTERSECT",VERTEX,{"derivedFrom":[subQ3,sQuery(id+"F0.wireOp",EDGE,"E12")]});Q76=makeQuery(id+"F0.imprint","IMPRINT",FACE,{"disambiguationData":[TD([[makeQuery(id+"F0.imprint","IMPRINT",EDGE,{"disambiguationData":[TD([[subQ5,1.0]])],"derivedFrom":subQ3}),1.0]])]});}
            var Q77;
            Q77=makeQuery(id+"F0.imprint","IMPRINT",FACE,{"disambiguationData":[TD([[makeQuery(id+"F0.imprint","IMPRINT",EDGE,{"derivedFrom":sQuery(id+"F0.wireOp",EDGE,"E456")}),1.0]])]});
            var Q78;
            Q78=makeQuery(id+"F0.imprint","IMPRINT",FACE,{"disambiguationData":[TD([[makeQuery(id+"F0.imprint","IMPRINT",EDGE,{"derivedFrom":sQuery(id+"F0.wireOp",EDGE,"E468.MirrorCS")}),-1.0]])]});
            extrude(context, id + "F1", {"entities" : qUnion([Q0, Q1, Q2, Q3, Q4, Q5, Q6, Q7, Q8, Q9, Q10, Q11, Q12, Q13, Q14, Q15, Q16, Q17, Q18, Q19, Q20, Q21, Q22, Q23, Q24, Q25, Q26, Q27, Q28, Q29, Q30, Q31, Q32, Q33, Q34, Q35, Q36, Q37, Q38, Q39, Q40, Q41, Q42, Q43, Q44, Q45, Q46, Q47, Q48, Q49, Q50, Q51, Q52, Q53, Q54, Q55, Q56, Q57, Q58, Q59, Q60, Q61, Q62, Q63, Q64, Q65, Q66, Q67, Q68, Q69, Q70, Q71, Q72, Q73, Q74, Q75, Q76, Q77, Q78]), "depth" : 5.08 * mm, "offsetDistance" : 25 * mm});
        }
        {
            var Q0;
            Q0=makeQuery(id+"F1.opExtrude","SWEPT_EDGE",EDGE,{"disambiguationData":[OSD([sQuery(id+"F0.wireOp",EDGE,"E51"),sQuery(id+"F0.wireOp",EDGE,"E270")])]});
            var Q1;
            Q1=makeQuery(id+"F1.opExtrude","SWEPT_EDGE",EDGE,{"disambiguationData":[OSD([sQuery(id+"F0.wireOp",EDGE,"E0.bottom"),sQuery(id+"F0.wireOp",EDGE,"E0.right")])]});
            var Q2;
            Q2=makeQuery(id+"F1.opExtrude","SWEPT_EDGE",EDGE,{"disambiguationData":[OSD([sQuery(id+"F0.wireOp",EDGE,"E41.MirrorCS"),sQuery(id+"F0.wireOp",EDGE,"E42.MirrorCS")])]});
            var Q3;
            Q3=makeQuery(id+"F1.opExtrude","SWEPT_EDGE",EDGE,{"disambiguationData":[OSD([sQuery(id+"F0.wireOp",EDGE,"E0.bottom"),sQuery(id+"F0.wireOp",EDGE,"E0.left")])]});
            var Q4;
            Q4=makeQuery(id+"F1.opExtrude","SWEPT_EDGE",EDGE,{"disambiguationData":[OSD([sQuery(id+"F0.wireOp",EDGE,"E39"),sQuery(id+"F0.wireOp",EDGE,"E40")])]});
            var Q5;
            Q5=makeQuery(id+"F1.opExtrude","SWEPT_EDGE",EDGE,{"disambiguationData":[OSD([sQuery(id+"F0.wireOp",EDGE,"E32.MirrorCS"),sQuery(id+"F0.wireOp",EDGE,"E40")])]});
            var Q6;
            Q6=makeQuery(id+"F1.opExtrude","SWEPT_EDGE",EDGE,{"disambiguationData":[OSD([sQuery(id+"F0.wireOp",EDGE,"E29"),sQuery(id+"F0.wireOp",EDGE,"E41.MirrorCS")])]});
            var Q7;
            Q7=makeQuery(id+"F1.opExtrude","SWEPT_EDGE",EDGE,{"disambiguationData":[OSD([sQuery(id+"F0.wireOp",EDGE,"E52.MirrorCS"),sQuery(id+"F0.wireOp",EDGE,"E270")])]});
            var Q8;
            Q8=makeQuery(id+"F1.opExtrude","SWEPT_EDGE",EDGE,{"disambiguationData":[OSD([sQuery(id+"F0.wireOp",EDGE,"E0.top"),sQuery(id+"F0.wireOp",EDGE,"E3")])]});
            var Q9;
            Q9=makeQuery(id+"F1.opExtrude","SWEPT_EDGE",EDGE,{"disambiguationData":[OSD([sQuery(id+"F0.wireOp",EDGE,"E0.top"),sQuery(id+"F0.wireOp",EDGE,"E5.MirrorCS")])]});
            var Q10;
            Q10=makeQuery(id+"F1.opExtrude","SWEPT_EDGE",EDGE,{"disambiguationData":[OSD([sQuery(id+"F0.wireOp",EDGE,"E3"),sQuery(id+"F0.wireOp",EDGE,"E68")])]});
            var Q11;
            Q11=makeQuery(id+"F1.opExtrude","SWEPT_EDGE",EDGE,{"disambiguationData":[OSD([sQuery(id+"F0.wireOp",EDGE,"E5.MirrorCS"),sQuery(id+"F0.wireOp",EDGE,"E68")])]});
            var Q12;
            Q12=makeQuery(id+"F1.opExtrude","SWEPT_EDGE",EDGE,{"disambiguationData":[OSD([sQuery(id+"F0.wireOp",EDGE,"E55.MirrorCS"),sQuery(id+"F0.wireOp",EDGE,"E68")])]});
            var Q13;
            Q13=makeQuery(id+"F1.opExtrude","SWEPT_EDGE",EDGE,{"disambiguationData":[OSD([sQuery(id+"F0.wireOp",EDGE,"E54"),sQuery(id+"F0.wireOp",EDGE,"E68")])]});
            fillet(context, id + "F2", {"entities" : qUnion([Q0, Q1, Q2, Q3, Q4, Q5, Q6, Q7, Q8, Q9, Q10, Q11, Q12, Q13]), "radius" : 5 * mm, "tangentPropagation" : true, "allowEdgeOverflow" : false});
        }
        {
            var Q0;
            {var subQ1=sQuery(id+"F0.wireOp",EDGE,"E128.right");Q0=makeQuery(id+"F0.imprint","IMPRINT",FACE,{"disambiguationData":[TD([[makeQuery(id+"F0.imprint","IMPRINT",EDGE,{"derivedFrom":subQ1}),1.0]])]});}
            var Q1;
            {var subQ0=sQuery(id+"F0.wireOp",EDGE,"E69.left");Q1=makeQuery(id+"F0.imprint","IMPRINT",FACE,{"disambiguationData":[TD([[makeQuery(id+"F0.imprint","IMPRINT",EDGE,{"derivedFrom":subQ0}),-1.0]])]});}
            var Q2;
            {var subQ6=sQuery(id+"F0.wireOp",EDGE,"E129");Q2=makeQuery(id+"F0.imprint","IMPRINT",FACE,{"disambiguationData":[TD([[makeQuery(id+"F0.imprint","IMPRINT",EDGE,{"derivedFrom":subQ6}),1.0]])]});}
            var Q3;
            {var subQ10=sQuery(id+"F0.wireOp",EDGE,"E112.left");Q3=makeQuery(id+"F0.imprint","IMPRINT",FACE,{"disambiguationData":[TD([[makeQuery(id+"F0.imprint","IMPRINT",EDGE,{"derivedFrom":subQ10}),-1.0]])]});}
            var Q4;
            {var subQ9=sQuery(id+"F0.wireOp",EDGE,"E130");Q4=makeQuery(id+"F0.imprint","IMPRINT",FACE,{"disambiguationData":[TD([[makeQuery(id+"F0.imprint","IMPRINT",EDGE,{"derivedFrom":subQ9}),-1.0]])]});}
            var Q5;
            {var subQ4=sQuery(id+"F0.wireOp",EDGE,"E142.MirrorCS");Q5=makeQuery(id+"F0.imprint","IMPRINT",FACE,{"disambiguationData":[TD([[makeQuery(id+"F0.imprint","IMPRINT",EDGE,{"derivedFrom":subQ4}),-1.0]])]});}
            var Q6;
            Q6=makeQuery(id+"F0.imprint","IMPRINT",FACE,{"disambiguationData":[TD([[makeQuery(id+"F0.imprint","IMPRINT",EDGE,{"derivedFrom":sQuery(id+"F0.wireOp",EDGE,"E148.MirrorCS")}),-1.0]])]});
            var Q7;
            {var subQ0=sQuery(id+"F0.wireOp",EDGE,"E146.MirrorCS");Q7=makeQuery(id+"F0.imprint","IMPRINT",FACE,{"disambiguationData":[TD([[makeQuery(id+"F0.imprint","IMPRINT",EDGE,{"derivedFrom":subQ0}),-1.0]])]});}
            var Q8;
            {var subQ0=sQuery(id+"F0.wireOp",EDGE,"E75.MirrorCS");Q8=makeQuery(id+"F0.imprint","IMPRINT",FACE,{"disambiguationData":[TD([[makeQuery(id+"F0.imprint","IMPRINT",EDGE,{"derivedFrom":subQ0}),-1.0]])]});}
            var Q9;
            {var subQ0=sQuery(id+"F0.wireOp",EDGE,"E116");Q9=makeQuery(id+"F0.imprint","IMPRINT",FACE,{"disambiguationData":[TD([[makeQuery(id+"F0.imprint","IMPRINT",EDGE,{"derivedFrom":subQ0}),1.0]])]});}
            var Q10;
            {var subQ0=sQuery(id+"F0.wireOp",EDGE,"E113");Q10=makeQuery(id+"F0.imprint","IMPRINT",FACE,{"disambiguationData":[TD([[makeQuery(id+"F0.imprint","IMPRINT",EDGE,{"derivedFrom":subQ0}),1.0]])]});}
            var Q11;
            {var subQ0=sQuery(id+"F0.wireOp",EDGE,"E122");Q11=makeQuery(id+"F0.imprint","IMPRINT",FACE,{"disambiguationData":[TD([[makeQuery(id+"F0.imprint","IMPRINT",EDGE,{"derivedFrom":subQ0}),1.0]])]});}
            var Q12;
            {var subQ2=sQuery(id+"F0.wireOp",EDGE,"E151.MirrorCS");Q12=makeQuery(id+"F0.imprint","IMPRINT",FACE,{"disambiguationData":[TD([[makeQuery(id+"F0.imprint","IMPRINT",EDGE,{"derivedFrom":subQ2}),-1.0]])]});}
            var Q13;
            {var subQ0=sQuery(id+"F0.wireOp",EDGE,"E91");Q13=makeQuery(id+"F0.imprint","IMPRINT",FACE,{"disambiguationData":[TD([[makeQuery(id+"F0.imprint","IMPRINT",EDGE,{"derivedFrom":subQ0}),1.0]])]});}
            var Q14;
            Q14=makeQuery(id+"F0.imprint","IMPRINT",FACE,{"disambiguationData":[TD([[makeQuery(id+"F0.imprint","IMPRINT",EDGE,{"derivedFrom":sQuery(id+"F0.wireOp",EDGE,"E139.MirrorCS")}),-1.0]])]});
            var Q15;
            {var subQ0=sQuery(id+"F0.wireOp",EDGE,"E119");Q15=makeQuery(id+"F0.imprint","IMPRINT",FACE,{"disambiguationData":[TD([[makeQuery(id+"F0.imprint","IMPRINT",EDGE,{"derivedFrom":subQ0}),1.0]])]});}
            var Q16;
            {var subQ0=sQuery(id+"F0.wireOp",EDGE,"E78.MirrorCS");Q16=makeQuery(id+"F0.imprint","IMPRINT",FACE,{"disambiguationData":[TD([[makeQuery(id+"F0.imprint","IMPRINT",EDGE,{"derivedFrom":subQ0}),1.0]])]});}
            var Q17;
            {var subQ0=sQuery(id+"F0.wireOp",EDGE,"E94");Q17=makeQuery(id+"F0.imprint","IMPRINT",FACE,{"disambiguationData":[TD([[makeQuery(id+"F0.imprint","IMPRINT",EDGE,{"derivedFrom":subQ0}),1.0]])]});}
            var Q18;
            {var subQ0=sQuery(id+"F0.wireOp",EDGE,"E147.MirrorCS");Q18=makeQuery(id+"F0.imprint","IMPRINT",FACE,{"disambiguationData":[TD([[makeQuery(id+"F0.imprint","IMPRINT",EDGE,{"derivedFrom":subQ0}),-1.0]])]});}
            var Q19;
            {var subQ2=sQuery(id+"F0.wireOp",EDGE,"E125");Q19=makeQuery(id+"F0.imprint","IMPRINT",FACE,{"disambiguationData":[TD([[makeQuery(id+"F0.imprint","IMPRINT",EDGE,{"derivedFrom":subQ2}),1.0]])]});}
            var Q20;
            {var subQ0=sQuery(id+"F0.wireOp",EDGE,"E121");Q20=makeQuery(id+"F0.imprint","IMPRINT",FACE,{"disambiguationData":[TD([[makeQuery(id+"F0.imprint","IMPRINT",EDGE,{"derivedFrom":subQ0}),1.0]])]});}
            var Q21;
            Q21=makeQuery(id+"F0.imprint","IMPRINT",FACE,{"disambiguationData":[TD([[makeQuery(id+"F0.imprint","IMPRINT",EDGE,{"derivedFrom":sQuery(id+"F0.wireOp",EDGE,"E69.left")}),1.0]])]});
            var Q22;
            {var subQ0=sQuery(id+"F0.wireOp",EDGE,"E154.MirrorCS");Q22=makeQuery(id+"F0.imprint","IMPRINT",FACE,{"disambiguationData":[TD([[makeQuery(id+"F0.imprint","IMPRINT",EDGE,{"derivedFrom":subQ0}),-1.0]])]});}
            var Q23;
            Q23=makeQuery(id+"F0.imprint","IMPRINT",FACE,{"disambiguationData":[TD([[makeQuery(id+"F0.imprint","IMPRINT",EDGE,{"derivedFrom":sQuery(id+"F0.wireOp",EDGE,"e9396e54-f83c-4728-87f9-c82e892d8226.bottom")}),-1.0]])]});
            var Q24;
            Q24=makeQuery(id+"F0.imprint","IMPRINT",FACE,{"disambiguationData":[TD([[makeQuery(id+"F0.imprint","IMPRINT",EDGE,{"derivedFrom":sQuery(id+"F0.wireOp",EDGE,"E112.bottom")}),-1.0]])]});
            var Q25;
            {var subQ0=sQuery(id+"F0.wireOp",EDGE,"E134.left");Q25=makeQuery(id+"F0.imprint","IMPRINT",FACE,{"disambiguationData":[TD([[makeQuery(id+"F0.imprint","IMPRINT",EDGE,{"derivedFrom":subQ0}),1.0]])]});}
            var Q26;
            Q26=makeQuery(id+"F0.imprint","IMPRINT",FACE,{"disambiguationData":[TD([[makeQuery(id+"F0.imprint","IMPRINT",EDGE,{"derivedFrom":sQuery(id+"F0.wireOp",EDGE,"46dbd811-14a4-4d06-a60a-d565d8d64afb.bottom")}),-1.0]])]});
            var Q27;
            {var subQ1=sQuery(id+"F0.wireOp",EDGE,"E73");Q27=makeQuery(id+"F0.imprint","IMPRINT",FACE,{"disambiguationData":[TD([[makeQuery(id+"F0.imprint","IMPRINT",EDGE,{"derivedFrom":subQ1}),-1.0]])]});}
            var Q28;
            {var subQ0=sQuery(id+"F0.wireOp",EDGE,"E134.right");Q28=makeQuery(id+"F0.imprint","IMPRINT",FACE,{"disambiguationData":[TD([[makeQuery(id+"F0.imprint","IMPRINT",EDGE,{"derivedFrom":subQ0}),-1.0]])]});}
            var Q29;
            Q29=makeQuery(id+"F0.imprint","IMPRINT",FACE,{"disambiguationData":[TD([[makeQuery(id+"F0.imprint","IMPRINT",EDGE,{"derivedFrom":sQuery(id+"F0.wireOp",EDGE,"12650880-9e35-4a89-a6c9-7a82fa3b4b18.bottom")}),-1.0]])]});
            var Q30;
            {var subQ0=sQuery(id+"F0.wireOp",EDGE,"E128.right");Q30=makeQuery(id+"F0.imprint","IMPRINT",FACE,{"disambiguationData":[TD([[makeQuery(id+"F0.imprint","IMPRINT",EDGE,{"derivedFrom":subQ0}),-1.0]])]});}
            var Q31;
            {var subQ0=sQuery(id+"F0.wireOp",EDGE,"E132");Q31=makeQuery(id+"F0.imprint","IMPRINT",FACE,{"disambiguationData":[TD([[makeQuery(id+"F0.imprint","IMPRINT",EDGE,{"derivedFrom":subQ0}),1.0]])]});}
            var Q32;
            {var subQ0=sQuery(id+"F0.wireOp",EDGE,"a3ccca05-ff92-47aa-8b78-ca77b52352e8");Q32=makeQuery(id+"F0.imprint","IMPRINT",FACE,{"disambiguationData":[TD([[makeQuery(id+"F0.imprint","IMPRINT",EDGE,{"derivedFrom":subQ0}),1.0]])]});}
            var Q33;
            {var subQ0=sQuery(id+"F0.wireOp",EDGE,"a3ccca05-ff92-47aa-8b78-ca77b52352e8");Q33=makeQuery(id+"F0.imprint","IMPRINT",FACE,{"disambiguationData":[TD([[makeQuery(id+"F0.imprint","IMPRINT",EDGE,{"derivedFrom":subQ0}),-1.0]])]});}
            var Q34;
            Q34=makeQuery(id+"F0.imprint","IMPRINT",FACE,{"disambiguationData":[TD([[makeQuery(id+"F0.imprint","IMPRINT",EDGE,{"derivedFrom":sQuery(id+"F0.wireOp",EDGE,"E160.MirrorCS")}),1.0]])]});
            var Q35;
            {var subQ9=sQuery(id+"F0.wireOp",EDGE,"E157.MirrorCS");var subQ31=sQuery(id+"F0.wireOp",EDGE,"E175");var subQ32=makeQuery(id+"F0.imprint","INTERSECT",VERTEX,{"derivedFrom":[subQ9,subQ31]});Q35=makeQuery(id+"F0.imprint","IMPRINT",FACE,{"disambiguationData":[TD([[makeQuery(id+"F0.imprint","IMPRINT",EDGE,{"disambiguationData":[TD([[subQ32,-1.0]])],"derivedFrom":subQ9}),-1.0]])]});}
            var Q36;
            {var subQ0=sQuery(id+"F0.wireOp",EDGE,"0b5fd9b5-5623-4f21-b6aa-7471e8c1aff0");Q36=makeQuery(id+"F0.imprint","IMPRINT",FACE,{"disambiguationData":[TD([[makeQuery(id+"F0.imprint","IMPRINT",EDGE,{"derivedFrom":subQ0}),-1.0]])]});}
            var Q37;
            {var subQ0=sQuery(id+"F0.wireOp",EDGE,"b92e4a5a-a64c-4d77-bf11-0f9a19bca047");Q37=makeQuery(id+"F0.imprint","IMPRINT",FACE,{"disambiguationData":[TD([[makeQuery(id+"F0.imprint","IMPRINT",EDGE,{"derivedFrom":subQ0}),-1.0]])]});}
            var Q38;
            {var subQ3=sQuery(id+"F0.wireOp",EDGE,"397e5c37-a89a-4139-8744-8d356609f999");Q38=makeQuery(id+"F0.imprint","IMPRINT",FACE,{"disambiguationData":[TD([[makeQuery(id+"F0.imprint","IMPRINT",EDGE,{"derivedFrom":subQ3}),-1.0]])]});}
            var Q39;
            Q39=makeQuery(id+"F0.imprint","IMPRINT",FACE,{"disambiguationData":[TD([[makeQuery(id+"F0.imprint","IMPRINT",EDGE,{"derivedFrom":sQuery(id+"F0.wireOp",EDGE,"E159.MirrorCS")}),-1.0]])]});
            var Q40;
            Q40=makeQuery(id+"F0.imprint","IMPRINT",FACE,{"disambiguationData":[TD([[makeQuery(id+"F0.imprint","IMPRINT",EDGE,{"derivedFrom":sQuery(id+"F0.wireOp",EDGE,"E185.bottom")}),1.0]])]});
            var Q41;
            {var subQ3=sQuery(id+"F0.wireOp",EDGE,"82faf99f-bf58-4b2e-a2b4-a88ec8648361.MirrorCS");Q41=makeQuery(id+"F0.imprint","IMPRINT",FACE,{"disambiguationData":[TD([[makeQuery(id+"F0.imprint","IMPRINT",EDGE,{"derivedFrom":subQ3}),1.0]])]});}
            var Q42;
            {var subQ0=sQuery(id+"F0.wireOp",EDGE,"E165");Q42=makeQuery(id+"F0.imprint","IMPRINT",FACE,{"disambiguationData":[TD([[makeQuery(id+"F0.imprint","IMPRINT",EDGE,{"derivedFrom":subQ0}),1.0]])]});}
            var Q43;
            {var subQ0=sQuery(id+"F0.wireOp",EDGE,"E162");Q43=makeQuery(id+"F0.imprint","IMPRINT",FACE,{"disambiguationData":[TD([[makeQuery(id+"F0.imprint","IMPRINT",EDGE,{"derivedFrom":subQ0}),1.0]])]});}
            var Q44;
            {var subQ0=sQuery(id+"F0.wireOp",EDGE,"E193");var subQ8=sQuery(id+"F0.wireOp",EDGE,"E175");var subQ9=makeQuery(id+"F0.imprint","INTERSECT",VERTEX,{"derivedFrom":[subQ8,subQ0]});Q44=makeQuery(id+"F0.imprint","IMPRINT",FACE,{"disambiguationData":[TD([[makeQuery(id+"F0.imprint","IMPRINT",EDGE,{"disambiguationData":[TD([[subQ9,-1.0]])],"derivedFrom":subQ8}),1.0]])]});}
            var Q45;
            {var subQ1=sQuery(id+"F0.wireOp",EDGE,"E197.right");var subQ7=sQuery(id+"F0.wireOp",EDGE,"E197.bottom");var subQ8=makeQuery(id+"F0.imprint","INTERSECT",VERTEX,{"derivedFrom":[subQ7,subQ1]});Q45=makeQuery(id+"F0.imprint","IMPRINT",FACE,{"disambiguationData":[TD([[makeQuery(id+"F0.imprint","IMPRINT",EDGE,{"disambiguationData":[TD([[subQ8,1.0]])],"derivedFrom":subQ7}),1.0]])]});}
            var Q46;
            {var subQ1=sQuery(id+"F0.wireOp",EDGE,"E197.top");var subQ7=sQuery(id+"F0.wireOp",EDGE,"E197.left");var subQ8=makeQuery(id+"F0.imprint","INTERSECT",VERTEX,{"derivedFrom":[subQ1,subQ7]});Q46=makeQuery(id+"F0.imprint","IMPRINT",FACE,{"disambiguationData":[TD([[makeQuery(id+"F0.imprint","IMPRINT",EDGE,{"disambiguationData":[TD([[subQ8,-1.0]])],"derivedFrom":subQ1}),-1.0]])]});}
            var Q47;
            {var subQ0=sQuery(id+"F0.wireOp",EDGE,"E171");Q47=makeQuery(id+"F0.imprint","IMPRINT",FACE,{"disambiguationData":[TD([[makeQuery(id+"F0.imprint","IMPRINT",EDGE,{"derivedFrom":subQ0}),1.0]])]});}
            var Q48;
            {var subQ0=sQuery(id+"F0.wireOp",EDGE,"E168");Q48=makeQuery(id+"F0.imprint","IMPRINT",FACE,{"disambiguationData":[TD([[makeQuery(id+"F0.imprint","IMPRINT",EDGE,{"derivedFrom":subQ0}),1.0]])]});}
            var Q49;
            {var subQ0=sQuery(id+"F0.wireOp",EDGE,"E194");var subQ5=sQuery(id+"F0.wireOp",EDGE,"E175");var subQ8=makeQuery(id+"F0.imprint","INTERSECT",VERTEX,{"derivedFrom":[subQ5,subQ0]});Q49=makeQuery(id+"F0.imprint","IMPRINT",FACE,{"disambiguationData":[TD([[makeQuery(id+"F0.imprint","IMPRINT",EDGE,{"disambiguationData":[TD([[subQ8,1.0]])],"derivedFrom":subQ5}),1.0]])]});}
            var Q50;
            {var subQ1=sQuery(id+"F0.wireOp",EDGE,"E197.right");var subQ5=sQuery(id+"F0.wireOp",EDGE,"E197.top");var subQ6=makeQuery(id+"F0.imprint","INTERSECT",VERTEX,{"derivedFrom":[subQ5,subQ1]});Q50=makeQuery(id+"F0.imprint","IMPRINT",FACE,{"disambiguationData":[TD([[makeQuery(id+"F0.imprint","IMPRINT",EDGE,{"disambiguationData":[TD([[subQ6,1.0]])],"derivedFrom":subQ5}),-1.0]])]});}
            var Q51;
            {var subQ1=sQuery(id+"F0.wireOp",EDGE,"E197.left");var subQ5=sQuery(id+"F0.wireOp",EDGE,"E197.bottom");var subQ6=makeQuery(id+"F0.imprint","INTERSECT",VERTEX,{"derivedFrom":[subQ5,subQ1]});Q51=makeQuery(id+"F0.imprint","IMPRINT",FACE,{"disambiguationData":[TD([[makeQuery(id+"F0.imprint","IMPRINT",EDGE,{"disambiguationData":[TD([[subQ6,-1.0]])],"derivedFrom":subQ5}),1.0]])]});}
            var Q52;
            {var subQ0=sQuery(id+"F0.wireOp",EDGE,"E202");var subQ1=sQuery(id+"F0.wireOp",EDGE,"E200");var subQ2=makeQuery(id+"F0.imprint","INTERSECT",VERTEX,{"derivedFrom":[subQ1,subQ0]});Q52=makeQuery(id+"F0.imprint","IMPRINT",FACE,{"disambiguationData":[TD([[makeQuery(id+"F0.imprint","IMPRINT",EDGE,{"disambiguationData":[TD([[subQ2,-1.0]])],"derivedFrom":subQ1}),-1.0]])]});}
            var Q53;
            {var subQ16=sQuery(id+"F0.wireOp",EDGE,"E204.bottom");Q53=makeQuery(id+"F0.imprint","IMPRINT",FACE,{"disambiguationData":[TD([[makeQuery(id+"F0.imprint","IMPRINT",EDGE,{"derivedFrom":subQ16}),1.0]])]});}
            var Q54;
            {var subQ1=sQuery(id+"F0.wireOp",EDGE,"E234.right");var subQ7=sQuery(id+"F0.wireOp",EDGE,"E234.top");var subQ8=makeQuery(id+"F0.imprint","INTERSECT",VERTEX,{"derivedFrom":[subQ7,subQ1]});Q54=makeQuery(id+"F0.imprint","IMPRINT",FACE,{"disambiguationData":[TD([[makeQuery(id+"F0.imprint","IMPRINT",EDGE,{"disambiguationData":[TD([[subQ8,1.0]])],"derivedFrom":subQ7}),-1.0]])]});}
            var Q55;
            {var subQ0=sQuery(id+"F0.wireOp",EDGE,"E210");Q55=makeQuery(id+"F0.imprint","IMPRINT",FACE,{"disambiguationData":[TD([[makeQuery(id+"F0.imprint","IMPRINT",EDGE,{"derivedFrom":subQ0}),-1.0]])]});}
            var Q56;
            {var subQ0=sQuery(id+"F0.wireOp",EDGE,"E206");Q56=makeQuery(id+"F0.imprint","IMPRINT",FACE,{"disambiguationData":[TD([[makeQuery(id+"F0.imprint","IMPRINT",EDGE,{"derivedFrom":subQ0}),1.0]])]});}
            var Q57;
            {var subQ0=sQuery(id+"F0.wireOp",EDGE,"E223.MirrorCS");Q57=makeQuery(id+"F0.imprint","IMPRINT",FACE,{"disambiguationData":[TD([[makeQuery(id+"F0.imprint","IMPRINT",EDGE,{"derivedFrom":subQ0}),1.0]])]});}
            var Q58;
            {var subQ1=sQuery(id+"F0.wireOp",EDGE,"E234.right");var subQ5=sQuery(id+"F0.wireOp",EDGE,"E234.bottom");var subQ6=makeQuery(id+"F0.imprint","INTERSECT",VERTEX,{"derivedFrom":[subQ5,subQ1]});Q58=makeQuery(id+"F0.imprint","IMPRINT",FACE,{"disambiguationData":[TD([[makeQuery(id+"F0.imprint","IMPRINT",EDGE,{"disambiguationData":[TD([[subQ6,1.0]])],"derivedFrom":subQ5}),1.0]])]});}
            var Q59;
            {var subQ5=sQuery(id+"F0.wireOp",EDGE,"E234.left");var subQ6=sQuery(id+"F0.wireOp",EDGE,"E234.bottom");var subQ7=makeQuery(id+"F0.imprint","INTERSECT",VERTEX,{"derivedFrom":[subQ6,subQ5]});Q59=makeQuery(id+"F0.imprint","IMPRINT",FACE,{"disambiguationData":[TD([[makeQuery(id+"F0.imprint","IMPRINT",EDGE,{"disambiguationData":[TD([[subQ7,-1.0]])],"derivedFrom":subQ6}),1.0]])]});}
            var Q60;
            {var subQ1=sQuery(id+"F0.wireOp",EDGE,"E234.top");var subQ6=sQuery(id+"F0.wireOp",EDGE,"E234.left");var subQ9=makeQuery(id+"F0.imprint","INTERSECT",VERTEX,{"derivedFrom":[subQ1,subQ6]});Q60=makeQuery(id+"F0.imprint","IMPRINT",FACE,{"disambiguationData":[TD([[makeQuery(id+"F0.imprint","IMPRINT",EDGE,{"disambiguationData":[TD([[subQ9,-1.0]])],"derivedFrom":subQ1}),-1.0]])]});}
            var Q61;
            {var subQ0=sQuery(id+"F0.wireOp",EDGE,"E239");var subQ1=sQuery(id+"F0.wireOp",EDGE,"E236");var subQ2=makeQuery(id+"F0.imprint","INTERSECT",VERTEX,{"derivedFrom":[subQ1,subQ0]});Q61=makeQuery(id+"F0.imprint","IMPRINT",FACE,{"disambiguationData":[TD([[makeQuery(id+"F0.imprint","IMPRINT",EDGE,{"disambiguationData":[TD([[subQ2,-1.0]])],"derivedFrom":subQ1}),-1.0]])]});}
            var Q62;
            {var subQ0=sQuery(id+"F0.wireOp",EDGE,"E227.MirrorCS");Q62=makeQuery(id+"F0.imprint","IMPRINT",FACE,{"disambiguationData":[TD([[makeQuery(id+"F0.imprint","IMPRINT",EDGE,{"derivedFrom":subQ0}),1.0]])]});}
            var Q63;
            {var subQ0=sQuery(id+"F0.wireOp",EDGE,"E220.MirrorCS");Q63=makeQuery(id+"F0.imprint","IMPRINT",FACE,{"disambiguationData":[TD([[makeQuery(id+"F0.imprint","IMPRINT",EDGE,{"derivedFrom":subQ0}),1.0]])]});}
            var Q64;
            {var subQ1=sQuery(id+"F0.wireOp",EDGE,"E209");Q64=makeQuery(id+"F0.imprint","IMPRINT",FACE,{"disambiguationData":[TD([[makeQuery(id+"F0.imprint","IMPRINT",EDGE,{"derivedFrom":subQ1}),-1.0]])]});}
            var Q65;
            {var subQ0=sQuery(id+"F0.wireOp",EDGE,"E213");Q65=makeQuery(id+"F0.imprint","IMPRINT",FACE,{"disambiguationData":[TD([[makeQuery(id+"F0.imprint","IMPRINT",EDGE,{"derivedFrom":subQ0}),-1.0]])]});}
            var Q66;
            {var subQ2=sQuery(id+"F0.wireOp",EDGE,"E217.MirrorCS");Q66=makeQuery(id+"F0.imprint","IMPRINT",FACE,{"disambiguationData":[TD([[makeQuery(id+"F0.imprint","IMPRINT",EDGE,{"derivedFrom":subQ2}),1.0]])]});}
            var Q67;
            {var subQ2=sQuery(id+"F0.wireOp",EDGE,"E226.MirrorCS");Q67=makeQuery(id+"F0.imprint","IMPRINT",FACE,{"disambiguationData":[TD([[makeQuery(id+"F0.imprint","IMPRINT",EDGE,{"derivedFrom":subQ2}),-1.0]])]});}
            var Q68;
            {var subQ0=sQuery(id+"F0.wireOp",EDGE,"E200");var subQ1=sQuery(id+"F0.wireOp",EDGE,"E197.right");var subQ2=makeQuery(id+"F0.imprint","INTERSECT",VERTEX,{"derivedFrom":[subQ1,subQ0]});Q68=makeQuery(id+"F0.imprint","IMPRINT",FACE,{"disambiguationData":[TD([[makeQuery(id+"F0.imprint","IMPRINT",EDGE,{"disambiguationData":[TD([[subQ2,1.0]])],"derivedFrom":subQ1}),1.0]])]});}
            var Q69;
            {var subQ0=sQuery(id+"F0.wireOp",EDGE,"E200");var subQ1=sQuery(id+"F0.wireOp",EDGE,"E197.bottom");var subQ2=makeQuery(id+"F0.imprint","INTERSECT",VERTEX,{"derivedFrom":[subQ1,subQ0]});Q69=makeQuery(id+"F0.imprint","IMPRINT",FACE,{"disambiguationData":[TD([[makeQuery(id+"F0.imprint","IMPRINT",EDGE,{"disambiguationData":[TD([[subQ2,-1.0]])],"derivedFrom":subQ1}),1.0]])]});}
            var Q70;
            {var subQ0=sQuery(id+"F0.wireOp",EDGE,"E201");var subQ1=sQuery(id+"F0.wireOp",EDGE,"E197.left");var subQ2=makeQuery(id+"F0.imprint","INTERSECT",VERTEX,{"derivedFrom":[subQ1,subQ0]});Q70=makeQuery(id+"F0.imprint","IMPRINT",FACE,{"disambiguationData":[TD([[makeQuery(id+"F0.imprint","IMPRINT",EDGE,{"disambiguationData":[TD([[subQ2,-1.0]])],"derivedFrom":subQ1}),-1.0]])]});}
            var Q71;
            {var subQ0=sQuery(id+"F0.wireOp",EDGE,"E201");var subQ1=sQuery(id+"F0.wireOp",EDGE,"E197.top");var subQ2=makeQuery(id+"F0.imprint","INTERSECT",VERTEX,{"derivedFrom":[subQ1,subQ0]});Q71=makeQuery(id+"F0.imprint","IMPRINT",FACE,{"disambiguationData":[TD([[makeQuery(id+"F0.imprint","IMPRINT",EDGE,{"disambiguationData":[TD([[subQ2,1.0]])],"derivedFrom":subQ1}),-1.0]])]});}
            var Q72;
            {var subQ0=sQuery(id+"F0.wireOp",EDGE,"E255");var subQ1=sQuery(id+"F0.wireOp",EDGE,"E251");var subQ2=makeQuery(id+"F0.imprint","INTERSECT",VERTEX,{"derivedFrom":[subQ1,subQ0]});Q72=makeQuery(id+"F0.imprint","IMPRINT",FACE,{"disambiguationData":[TD([[makeQuery(id+"F0.imprint","IMPRINT",EDGE,{"disambiguationData":[TD([[subQ2,-1.0]])],"derivedFrom":subQ1}),1.0]])]});}
            var Q73;
            {var subQ0=sQuery(id+"F0.wireOp",EDGE,"E255");var subQ1=sQuery(id+"F0.wireOp",EDGE,"E251");var subQ2=makeQuery(id+"F0.imprint","INTERSECT",VERTEX,{"derivedFrom":[subQ1,subQ0]});Q73=makeQuery(id+"F0.imprint","IMPRINT",FACE,{"disambiguationData":[TD([[makeQuery(id+"F0.imprint","IMPRINT",EDGE,{"disambiguationData":[TD([[subQ2,-1.0]])],"derivedFrom":subQ1}),-1.0]])]});}
            var Q74;
            {var subQ1=sQuery(id+"F0.wireOp",EDGE,"E175");var subQ3=sQuery(id+"F0.wireOp",EDGE,"E253");var subQ4=makeQuery(id+"F0.imprint","INTERSECT",VERTEX,{"derivedFrom":[subQ1,subQ3]});Q74=makeQuery(id+"F0.imprint","IMPRINT",FACE,{"disambiguationData":[TD([[makeQuery(id+"F0.imprint","IMPRINT",EDGE,{"disambiguationData":[TD([[subQ4,1.0]])],"derivedFrom":subQ3}),1.0]])]});}
            var Q75;
            {var subQ1=sQuery(id+"F0.wireOp",EDGE,"E196.MirrorCS");var subQ3=sQuery(id+"F0.wireOp",EDGE,"E254");var subQ4=makeQuery(id+"F0.imprint","INTERSECT",VERTEX,{"derivedFrom":[subQ1,subQ3]});Q75=makeQuery(id+"F0.imprint","IMPRINT",FACE,{"disambiguationData":[TD([[makeQuery(id+"F0.imprint","IMPRINT",EDGE,{"disambiguationData":[TD([[subQ4,1.0]])],"derivedFrom":subQ3}),-1.0]])]});}
            var Q76;
            {var subQ1=sQuery(id+"F0.wireOp",EDGE,"E185.top");var subQ5=sQuery(id+"F0.wireOp",EDGE,"E196.MirrorCS");var subQ6=makeQuery(id+"F0.imprint","INTERSECT",VERTEX,{"derivedFrom":[subQ1,subQ5]});Q76=makeQuery(id+"F0.imprint","IMPRINT",FACE,{"disambiguationData":[TD([[makeQuery(id+"F0.imprint","IMPRINT",EDGE,{"disambiguationData":[TD([[subQ6,-1.0]])],"derivedFrom":subQ1}),1.0]])]});}
            var Q77;
            {var subQ1=sQuery(id+"F0.wireOp",EDGE,"E185.top");var subQ3=sQuery(id+"F0.wireOp",EDGE,"E254");var subQ4=makeQuery(id+"F0.imprint","INTERSECT",VERTEX,{"derivedFrom":[subQ1,subQ3]});Q77=makeQuery(id+"F0.imprint","IMPRINT",FACE,{"disambiguationData":[TD([[makeQuery(id+"F0.imprint","IMPRINT",EDGE,{"disambiguationData":[TD([[subQ4,-1.0]])],"derivedFrom":subQ3}),-1.0]])]});}
            var Q78;
            {var subQ1=sQuery(id+"F0.wireOp",EDGE,"E195");var subQ3=sQuery(id+"F0.wireOp",EDGE,"E253");var subQ4=makeQuery(id+"F0.imprint","INTERSECT",VERTEX,{"derivedFrom":[subQ1,subQ3]});Q78=makeQuery(id+"F0.imprint","IMPRINT",FACE,{"disambiguationData":[TD([[makeQuery(id+"F0.imprint","IMPRINT",EDGE,{"disambiguationData":[TD([[subQ4,-1.0]])],"derivedFrom":subQ3}),1.0]])]});}
            var Q79;
            {var subQ1=sQuery(id+"F0.wireOp",EDGE,"E195");var subQ7=sQuery(id+"F0.wireOp",EDGE,"E175");var subQ8=makeQuery(id+"F0.imprint","INTERSECT",VERTEX,{"derivedFrom":[subQ7,subQ1]});Q79=makeQuery(id+"F0.imprint","IMPRINT",FACE,{"disambiguationData":[TD([[makeQuery(id+"F0.imprint","IMPRINT",EDGE,{"disambiguationData":[TD([[subQ8,-1.0]])],"derivedFrom":subQ7}),1.0]])]});}
            var Q80;
            Q80=makeQuery(id+"F0.imprint","IMPRINT",FACE,{"disambiguationData":[TD([[makeQuery(id+"F0.imprint","IMPRINT",EDGE,{"derivedFrom":sQuery(id+"F0.wireOp",EDGE,"E70")}),-1.0]])]});
            var Q81;
            {var subQ0=sQuery(id+"F0.wireOp",EDGE,"E85");Q81=makeQuery(id+"F0.imprint","IMPRINT",FACE,{"disambiguationData":[TD([[makeQuery(id+"F0.imprint","IMPRINT",EDGE,{"derivedFrom":subQ0}),1.0]])]});}
            var Q82;
            Q82=makeQuery(id+"F0.imprint","IMPRINT",FACE,{"disambiguationData":[TD([[makeQuery(id+"F0.imprint","IMPRINT",EDGE,{"derivedFrom":sQuery(id+"F0.wireOp",EDGE,"E185.right")}),-1.0]])]});
            var Q83;
            {var subQ0=sQuery(id+"F0.wireOp",EDGE,"E253");var subQ1=sQuery(id+"F0.wireOp",EDGE,"E195");var subQ2=makeQuery(id+"F0.imprint","INTERSECT",VERTEX,{"derivedFrom":[subQ1,subQ0]});Q83=makeQuery(id+"F0.imprint","IMPRINT",FACE,{"disambiguationData":[TD([[makeQuery(id+"F0.imprint","IMPRINT",EDGE,{"disambiguationData":[TD([[subQ2,-1.0]])],"derivedFrom":subQ1}),1.0]])]});}
            var Q84;
            {var subQ0=sQuery(id+"F0.wireOp",EDGE,"E254");var subQ1=sQuery(id+"F0.wireOp",EDGE,"E185.top");var subQ2=makeQuery(id+"F0.imprint","INTERSECT",VERTEX,{"derivedFrom":[subQ1,subQ0]});Q84=makeQuery(id+"F0.imprint","IMPRINT",FACE,{"disambiguationData":[TD([[makeQuery(id+"F0.imprint","IMPRINT",EDGE,{"disambiguationData":[TD([[subQ2,1.0]])],"derivedFrom":subQ1}),1.0]])]});}
            var Q85;
            {var subQ0=sQuery(id+"F0.wireOp",EDGE,"E253");var subQ1=sQuery(id+"F0.wireOp",EDGE,"E175");var subQ2=makeQuery(id+"F0.imprint","INTERSECT",VERTEX,{"derivedFrom":[subQ1,subQ0]});Q85=makeQuery(id+"F0.imprint","IMPRINT",FACE,{"disambiguationData":[TD([[makeQuery(id+"F0.imprint","IMPRINT",EDGE,{"disambiguationData":[TD([[subQ2,1.0]])],"derivedFrom":subQ1}),1.0]])]});}
            var Q86;
            {var subQ0=sQuery(id+"F0.wireOp",EDGE,"E254");var subQ1=sQuery(id+"F0.wireOp",EDGE,"E196.MirrorCS");var subQ2=makeQuery(id+"F0.imprint","INTERSECT",VERTEX,{"derivedFrom":[subQ1,subQ0]});Q86=makeQuery(id+"F0.imprint","IMPRINT",FACE,{"disambiguationData":[TD([[makeQuery(id+"F0.imprint","IMPRINT",EDGE,{"disambiguationData":[TD([[subQ2,1.0]])],"derivedFrom":subQ1}),-1.0]])]});}
            var Q87;
            Q87=makeQuery(id+"F0.imprint","IMPRINT",FACE,{"disambiguationData":[TD([[makeQuery(id+"F0.imprint","IMPRINT",EDGE,{"derivedFrom":sQuery(id+"F0.wireOp",EDGE,"E185.left")}),1.0]])]});
            extrude(context, id + "F3", {"entities" : qUnion([Q0, Q1, Q2, Q3, Q4, Q5, Q6, Q7, Q8, Q9, Q10, Q11, Q12, Q13, Q14, Q15, Q16, Q17, Q18, Q19, Q20, Q21, Q22, Q23, Q24, Q25, Q26, Q27, Q28, Q29, Q30, Q31, Q32, Q33, Q34, Q35, Q36, Q37, Q38, Q39, Q40, Q41, Q42, Q43, Q44, Q45, Q46, Q47, Q48, Q49, Q50, Q51, Q52, Q53, Q54, Q55, Q56, Q57, Q58, Q59, Q60, Q61, Q62, Q63, Q64, Q65, Q66, Q67, Q68, Q69, Q70, Q71, Q72, Q73, Q74, Q75, Q76, Q77, Q78, Q79, Q80, Q81, Q82, Q83, Q84, Q85, Q86, Q87]), "depth" : 3.17 * mm, "offsetDistance" : 25 * mm});
        }
        {
            var Q0;
            Q0=makeQuery(id+"F3.opExtrude","SWEPT_EDGE",EDGE,{"disambiguationData":[OSD([sQuery(id+"F0.wireOp",EDGE,"E185.bottom"),sQuery(id+"F0.wireOp",EDGE,"E185.right")])]});
            var Q1;
            Q1=makeQuery(id+"F3.opExtrude","SWEPT_EDGE",EDGE,{"disambiguationData":[OSD([sQuery(id+"F0.wireOp",EDGE,"E185.bottom"),sQuery(id+"F0.wireOp",EDGE,"E185.left")])]});
            fillet(context, id + "F4", {"entities" : qUnion([Q0, Q1]), "radius" : 5 * mm, "tangentPropagation" : true, "allowEdgeOverflow" : false});
        }
        {
            var Q0;
            {var subQ0=sQuery(id+"F0.wireOp",EDGE,"E428");var subQ3=sQuery(id+"F0.wireOp",EDGE,"E429");var subQ4=makeQuery(id+"F0.imprint","INTERSECT",VERTEX,{"disambiguationData":[OD(0.0)],"derivedFrom":[subQ0,subQ3]});Q0=makeQuery(id+"F0.imprint","IMPRINT",FACE,{"disambiguationData":[TD([[makeQuery(id+"F0.imprint","IMPRINT",EDGE,{"disambiguationData":[TD([[subQ4,1.0]])],"derivedFrom":subQ3}),-1.0]])]});}
            var Q1;
            {var subQ8=sQuery(id+"F0.wireOp",EDGE,"E435");Q1=makeQuery(id+"F0.imprint","IMPRINT",FACE,{"disambiguationData":[TD([[makeQuery(id+"F0.imprint","IMPRINT",EDGE,{"derivedFrom":subQ8}),1.0]])]});}
            var Q2;
            {var subQ5=sQuery(id+"F0.wireOp",EDGE,"E418");Q2=makeQuery(id+"F0.imprint","IMPRINT",FACE,{"disambiguationData":[TD([[makeQuery(id+"F0.imprint","IMPRINT",EDGE,{"derivedFrom":subQ5}),1.0]])]});}
            var Q3;
            {var subQ0=sQuery(id+"F0.wireOp",EDGE,"E423");Q3=makeQuery(id+"F0.imprint","IMPRINT",FACE,{"disambiguationData":[TD([[makeQuery(id+"F0.imprint","IMPRINT",EDGE,{"derivedFrom":subQ0}),-1.0]])]});}
            var Q4;
            {var subQ0=sQuery(id+"F0.wireOp",EDGE,"E425");Q4=makeQuery(id+"F0.imprint","IMPRINT",FACE,{"disambiguationData":[TD([[makeQuery(id+"F0.imprint","IMPRINT",EDGE,{"derivedFrom":subQ0}),-1.0]])]});}
            var Q5;
            Q5=makeQuery(id+"F0.imprint","IMPRINT",FACE,{"disambiguationData":[TD([[makeQuery(id+"F0.imprint","IMPRINT",EDGE,{"derivedFrom":sQuery(id+"F0.wireOp",EDGE,"E427")}),1.0]])]});
            extrude(context, id + "F5", {"entities" : qUnion([Q0, Q1, Q2, Q3, Q4, Q5]), "depth" : 15.24 * mm, "offsetDistance" : 25 * mm});
        }
        {
            var Q0;
            Q0=makeQuery(id+"F5.opExtrude","SWEPT_EDGE",EDGE,{"disambiguationData":[OSD([sQuery(id+"F0.wireOp",EDGE,"E417"),sQuery(id+"F0.wireOp",EDGE,"E435")])]});
            var Q1;
            Q1=makeQuery(id+"F5.opExtrude","SWEPT_EDGE",EDGE,{"disambiguationData":[OSD([sQuery(id+"F0.wireOp",EDGE,"E416"),sQuery(id+"F0.wireOp",EDGE,"E435")])]});
            fillet(context, id + "F6", {"entities" : qUnion([Q0, Q1]), "radius" : 7.25 * mm, "tangentPropagation" : true, "allowEdgeOverflow" : false});
        }
        {
            var Q0;
            Q0=makeQuery(id+"F1.opExtrude","SWEPT_FACE",FACE,{"disambiguationData":[OSD([sQuery(id+"F0.wireOp",EDGE,"E436.left")])]});
            var sketch = newSketch(context, id + "F7", { "sketchPlane" : qUnion([Q0])});
            skLineSegment(sketch, "E476", {"start": v(-334.03, 5.08) * mm, "end": v(-321.48, 39.55) * mm});
            skLineSegment(sketch, "E477", {"start": v(-321.48, 39.55) * mm, "end": v(-308.93, 5.08) * mm});
            skLineSegment(sketch, "E478", {"start": v(-321.48, 39.55) * mm, "end": v(-321.48, 5.08) * mm, "construction": true});
            skLineSegment(sketch, "E479", {"start": v(-327.03, 5.08) * mm, "end": v(-321.48, 20.32) * mm});
            skLineSegment(sketch, "E480", {"start": v(-321.48, 20.32) * mm, "end": v(-315.93, 5.08) * mm});
            skLineSegment(sketch, "E481", {"start": v(-328.48, 20.32) * mm, "end": v(-314.48, 20.32) * mm});
            skLineSegment(sketch, "E482", {"start": v(-329.2, 18.32) * mm, "end": v(-313.75, 18.32) * mm});
            skLineSegment(sketch, "E483", {"start": v(-333.3, 7.08) * mm, "end": v(-309.66, 7.08) * mm});
            skLineSegment(sketch, "E484", {"start": v(-308.93, 5.08) * mm, "end": v(-308.93, 39.55) * mm, "construction": true});
            skLineSegment(sketch, "E485.MirrorCS", {"start": v(-296.39, 39.55) * mm, "end": v(-308.93, 5.08) * mm});
            skLineSegment(sketch, "E486.MirrorCS", {"start": v(-296.39, 20.32) * mm, "end": v(-301.93, 5.08) * mm});
            skLineSegment(sketch, "E487.MirrorCS", {"start": v(-296.39, 39.55) * mm, "end": v(-296.39, 5.08) * mm, "construction": true});
            skLineSegment(sketch, "E488.MirrorCS", {"start": v(-290.84, 5.08) * mm, "end": v(-296.39, 20.32) * mm});
            skLineSegment(sketch, "E489.MirrorCS", {"start": v(-283.84, 5.08) * mm, "end": v(-296.39, 39.55) * mm});
            skLineSegment(sketch, "E490.MirrorCS", {"start": v(-288.66, 18.32) * mm, "end": v(-304.12, 18.32) * mm});
            skLineSegment(sketch, "E491.MirrorCS", {"start": v(-289.39, 20.32) * mm, "end": v(-303.39, 20.32) * mm});
            skLineSegment(sketch, "E492.MirrorCS", {"start": v(-284.57, 7.08) * mm, "end": v(-308.2, 7.08) * mm});
            skLineSegment(sketch, "E493", {"start": v(-283.84, 5.08) * mm, "end": v(-283.84, 39.55) * mm, "construction": true});
            skLineSegment(sketch, "E494.MirrorCS", {"start": v(-283.84, 5.08) * mm, "end": v(-271.3, 39.55) * mm});
            skLineSegment(sketch, "E495.MirrorCS", {"start": v(-278.3, 20.32) * mm, "end": v(-264.3, 20.32) * mm});
            skLineSegment(sketch, "E496.MirrorCS", {"start": v(-279.02, 18.32) * mm, "end": v(-263.57, 18.32) * mm});
            skLineSegment(sketch, "E497.MirrorCS", {"start": v(-276.84, 5.08) * mm, "end": v(-271.3, 20.32) * mm});
            skLineSegment(sketch, "E498.MirrorCS", {"start": v(-283.11, 7.08) * mm, "end": v(-259.47, 7.08) * mm});
            skLineSegment(sketch, "E499.MirrorCS", {"start": v(-271.3, 20.32) * mm, "end": v(-265.75, 5.08) * mm});
            skLineSegment(sketch, "E500.MirrorCS", {"start": v(-271.3, 39.55) * mm, "end": v(-271.3, 5.08) * mm, "construction": true});
            skLineSegment(sketch, "E501.MirrorCS", {"start": v(-271.3, 39.55) * mm, "end": v(-258.75, 5.08) * mm});
            skLineSegment(sketch, "E502", {"start": v(-283.11, 7.08) * mm, "end": v(-284.57, 7.08) * mm});
            skLineSegment(sketch, "E503", {"start": v(-308.2, 7.08) * mm, "end": v(-309.66, 7.08) * mm});
            skSolve(sketch);
        }
        {
            var Q0;
            {var subQ0=sQuery(id+"F7.wireOp",EDGE,"E482");var subQ1=sQuery(id+"F7.wireOp",EDGE,"E477");var subQ2=makeQuery(id+"F7.imprint","INTERSECT",VERTEX,{"derivedFrom":[subQ1,subQ0]});Q0=makeQuery(id+"F7.imprint","IMPRINT",FACE,{"disambiguationData":[TD([[makeQuery(id+"F7.imprint","IMPRINT",EDGE,{"disambiguationData":[TD([[subQ2,-1.0]])],"derivedFrom":subQ1}),-1.0]])]});}
            var Q1;
            {var subQ0=sQuery(id+"F7.wireOp",EDGE,"E481");var subQ1=sQuery(id+"F7.wireOp",EDGE,"E477");var subQ2=makeQuery(id+"F7.imprint","INTERSECT",VERTEX,{"derivedFrom":[subQ1,subQ0]});Q1=makeQuery(id+"F7.imprint","IMPRINT",FACE,{"disambiguationData":[TD([[makeQuery(id+"F7.imprint","IMPRINT",EDGE,{"disambiguationData":[TD([[subQ2,-1.0]])],"derivedFrom":subQ1}),-1.0]])]});}
            var Q2;
            {var subQ0=sQuery(id+"F7.wireOp",EDGE,"E481");var subQ1=sQuery(id+"F7.wireOp",EDGE,"E476");var subQ2=makeQuery(id+"F7.imprint","INTERSECT",VERTEX,{"derivedFrom":[subQ1,subQ0]});Q2=makeQuery(id+"F7.imprint","IMPRINT",FACE,{"disambiguationData":[TD([[makeQuery(id+"F7.imprint","IMPRINT",EDGE,{"disambiguationData":[TD([[subQ2,1.0]])],"derivedFrom":subQ1}),-1.0]])]});}
            var Q3;
            {var subQ1=sQuery(id+"F7.wireOp",EDGE,"E479");var subQ3=sQuery(id+"F7.wireOp",EDGE,"E482");var subQ4=makeQuery(id+"F7.imprint","INTERSECT",VERTEX,{"derivedFrom":[subQ1,subQ3]});Q3=makeQuery(id+"F7.imprint","IMPRINT",FACE,{"disambiguationData":[TD([[makeQuery(id+"F7.imprint","IMPRINT",EDGE,{"disambiguationData":[TD([[subQ4,-1.0]])],"derivedFrom":subQ3}),1.0]])]});}
            var Q4;
            {var subQ0=sQuery(id+"F7.wireOp",EDGE,"E482");var subQ1=sQuery(id+"F7.wireOp",EDGE,"E476");var subQ2=makeQuery(id+"F7.imprint","INTERSECT",VERTEX,{"derivedFrom":[subQ1,subQ0]});Q4=makeQuery(id+"F7.imprint","IMPRINT",FACE,{"disambiguationData":[TD([[makeQuery(id+"F7.imprint","IMPRINT",EDGE,{"disambiguationData":[TD([[subQ2,1.0]])],"derivedFrom":subQ1}),-1.0]])]});}
            var Q5;
            {var subQ0=sQuery(id+"F7.wireOp",EDGE,"E476");var subQ1=makeQuery(id+"F1.opExtrude","CAP_EDGE",EDGE,{"disambiguationData":[OSD([sQuery(id+"F0.wireOp",EDGE,"E436.left")])],"isStart":false});var subQ2=makeQuery(id+"F7.imprint","INTERSECT",VERTEX,{"derivedFrom":[subQ1,subQ0]});Q5=makeQuery(id+"F7.imprint","IMPRINT",FACE,{"disambiguationData":[TD([[makeQuery(id+"F7.imprint","IMPRINT",EDGE,{"disambiguationData":[TD([[subQ2,-1.0]])],"derivedFrom":subQ0}),-1.0]])]});}
            var Q6;
            {var subQ0=sQuery(id+"F7.wireOp",EDGE,"E479");var subQ1=makeQuery(id+"F1.opExtrude","CAP_EDGE",EDGE,{"disambiguationData":[OSD([sQuery(id+"F0.wireOp",EDGE,"E436.left")])],"isStart":false});var subQ2=makeQuery(id+"F7.imprint","INTERSECT",VERTEX,{"derivedFrom":[subQ1,subQ0]});Q6=makeQuery(id+"F7.imprint","IMPRINT",FACE,{"disambiguationData":[TD([[makeQuery(id+"F7.imprint","IMPRINT",EDGE,{"disambiguationData":[TD([[subQ2,-1.0]])],"derivedFrom":subQ0}),-1.0]])]});}
            var Q7;
            {var subQ1=makeQuery(id+"F1.opExtrude","CAP_EDGE",EDGE,{"disambiguationData":[OSD([sQuery(id+"F0.wireOp",EDGE,"E436.left")])],"isStart":false});var subQ5=sQuery(id+"F7.wireOp",EDGE,"E480");var subQ6=makeQuery(id+"F7.imprint","INTERSECT",VERTEX,{"derivedFrom":[subQ1,subQ5]});Q7=makeQuery(id+"F7.imprint","IMPRINT",FACE,{"disambiguationData":[TD([[makeQuery(id+"F7.imprint","IMPRINT",EDGE,{"disambiguationData":[TD([[subQ6,1.0]])],"derivedFrom":subQ5}),1.0]])]});}
            var Q8;
            {var subQ1=makeQuery(id+"F1.opExtrude","CAP_EDGE",EDGE,{"disambiguationData":[OSD([sQuery(id+"F0.wireOp",EDGE,"E436.left")])],"isStart":false});var subQ5=sQuery(id+"F7.wireOp",EDGE,"E486.MirrorCS");var subQ6=makeQuery(id+"F7.imprint","INTERSECT",VERTEX,{"derivedFrom":[subQ1,subQ5]});Q8=makeQuery(id+"F7.imprint","IMPRINT",FACE,{"disambiguationData":[TD([[makeQuery(id+"F7.imprint","IMPRINT",EDGE,{"disambiguationData":[TD([[subQ6,1.0]])],"derivedFrom":subQ5}),-1.0]])]});}
            var Q9;
            {var subQ0=sQuery(id+"F7.wireOp",EDGE,"E490.MirrorCS");var subQ1=sQuery(id+"F7.wireOp",EDGE,"E485.MirrorCS");var subQ2=makeQuery(id+"F7.imprint","INTERSECT",VERTEX,{"derivedFrom":[subQ1,subQ0]});Q9=makeQuery(id+"F7.imprint","IMPRINT",FACE,{"disambiguationData":[TD([[makeQuery(id+"F7.imprint","IMPRINT",EDGE,{"disambiguationData":[TD([[subQ2,1.0]])],"derivedFrom":subQ1}),1.0]])]});}
            var Q10;
            {var subQ1=sQuery(id+"F7.wireOp",EDGE,"E486.MirrorCS");var subQ3=sQuery(id+"F7.wireOp",EDGE,"E490.MirrorCS");var subQ4=makeQuery(id+"F7.imprint","INTERSECT",VERTEX,{"derivedFrom":[subQ1,subQ3]});Q10=makeQuery(id+"F7.imprint","IMPRINT",FACE,{"disambiguationData":[TD([[makeQuery(id+"F7.imprint","IMPRINT",EDGE,{"disambiguationData":[TD([[subQ4,1.0]])],"derivedFrom":subQ3}),-1.0]])]});}
            var Q11;
            {var subQ3=sQuery(id+"F7.wireOp",EDGE,"E490.MirrorCS");var subQ5=sQuery(id+"F7.wireOp",EDGE,"E489.MirrorCS");var subQ6=makeQuery(id+"F7.imprint","INTERSECT",VERTEX,{"derivedFrom":[subQ5,subQ3]});Q11=makeQuery(id+"F7.imprint","IMPRINT",FACE,{"disambiguationData":[TD([[makeQuery(id+"F7.imprint","IMPRINT",EDGE,{"disambiguationData":[TD([[subQ6,-1.0]])],"derivedFrom":subQ5}),1.0]])]});}
            var Q12;
            {var subQ0=sQuery(id+"F7.wireOp",EDGE,"E492.MirrorCS");var subQ1=sQuery(id+"F7.wireOp",EDGE,"E488.MirrorCS");var subQ2=makeQuery(id+"F7.imprint","INTERSECT",VERTEX,{"derivedFrom":[subQ1,subQ0]});Q12=makeQuery(id+"F7.imprint","IMPRINT",FACE,{"disambiguationData":[TD([[makeQuery(id+"F7.imprint","IMPRINT",EDGE,{"disambiguationData":[TD([[subQ2,-1.0]])],"derivedFrom":subQ1}),-1.0]])]});}
            var Q13;
            {var subQ0=sQuery(id+"F7.wireOp",EDGE,"E488.MirrorCS");var subQ1=makeQuery(id+"F1.opExtrude","CAP_EDGE",EDGE,{"disambiguationData":[OSD([sQuery(id+"F0.wireOp",EDGE,"E436.left")])],"isStart":false});var subQ2=makeQuery(id+"F7.imprint","INTERSECT",VERTEX,{"derivedFrom":[subQ1,subQ0]});Q13=makeQuery(id+"F7.imprint","IMPRINT",FACE,{"disambiguationData":[TD([[makeQuery(id+"F7.imprint","IMPRINT",EDGE,{"disambiguationData":[TD([[subQ2,-1.0]])],"derivedFrom":subQ0}),-1.0]])]});}
            var Q14;
            {var subQ0=sQuery(id+"F7.wireOp",EDGE,"E490.MirrorCS");var subQ1=sQuery(id+"F7.wireOp",EDGE,"E485.MirrorCS");var subQ2=makeQuery(id+"F7.imprint","INTERSECT",VERTEX,{"derivedFrom":[subQ1,subQ0]});Q14=makeQuery(id+"F7.imprint","IMPRINT",FACE,{"disambiguationData":[TD([[makeQuery(id+"F7.imprint","IMPRINT",EDGE,{"disambiguationData":[TD([[subQ2,-1.0]])],"derivedFrom":subQ1}),1.0]])]});}
            var Q15;
            {var subQ0=sQuery(id+"F7.wireOp",EDGE,"E495.MirrorCS");var subQ1=sQuery(id+"F7.wireOp",EDGE,"E494.MirrorCS");var subQ2=makeQuery(id+"F7.imprint","INTERSECT",VERTEX,{"derivedFrom":[subQ1,subQ0]});Q15=makeQuery(id+"F7.imprint","IMPRINT",FACE,{"disambiguationData":[TD([[makeQuery(id+"F7.imprint","IMPRINT",EDGE,{"disambiguationData":[TD([[subQ2,1.0]])],"derivedFrom":subQ1}),-1.0]])]});}
            var Q16;
            {var subQ0=sQuery(id+"F7.wireOp",EDGE,"E497.MirrorCS");var subQ1=sQuery(id+"F7.wireOp",EDGE,"E496.MirrorCS");var subQ2=makeQuery(id+"F7.imprint","INTERSECT",VERTEX,{"derivedFrom":[subQ1,subQ0]});Q16=makeQuery(id+"F7.imprint","IMPRINT",FACE,{"disambiguationData":[TD([[makeQuery(id+"F7.imprint","IMPRINT",EDGE,{"disambiguationData":[TD([[subQ2,-1.0]])],"derivedFrom":subQ1}),1.0]])]});}
            var Q17;
            {var subQ0=sQuery(id+"F7.wireOp",EDGE,"E501.MirrorCS");var subQ5=sQuery(id+"F7.wireOp",EDGE,"E496.MirrorCS");var subQ7=makeQuery(id+"F7.imprint","INTERSECT",VERTEX,{"derivedFrom":[subQ5,subQ0]});Q17=makeQuery(id+"F7.imprint","IMPRINT",FACE,{"disambiguationData":[TD([[makeQuery(id+"F7.imprint","IMPRINT",EDGE,{"disambiguationData":[TD([[subQ7,1.0]])],"derivedFrom":subQ5}),1.0]])]});}
            var Q18;
            {var subQ0=sQuery(id+"F7.wireOp",EDGE,"E501.MirrorCS");var subQ1=sQuery(id+"F7.wireOp",EDGE,"E496.MirrorCS");var subQ2=makeQuery(id+"F7.imprint","INTERSECT",VERTEX,{"derivedFrom":[subQ1,subQ0]});Q18=makeQuery(id+"F7.imprint","IMPRINT",FACE,{"disambiguationData":[TD([[makeQuery(id+"F7.imprint","IMPRINT",EDGE,{"disambiguationData":[TD([[subQ2,1.0]])],"derivedFrom":subQ1}),-1.0]])]});}
            var Q19;
            {var subQ0=sQuery(id+"F7.wireOp",EDGE,"E501.MirrorCS");var subQ1=sQuery(id+"F7.wireOp",EDGE,"E498.MirrorCS");var subQ2=makeQuery(id+"F7.imprint","INTERSECT",VERTEX,{"derivedFrom":[subQ1,subQ0]});Q19=makeQuery(id+"F7.imprint","IMPRINT",FACE,{"disambiguationData":[TD([[makeQuery(id+"F7.imprint","IMPRINT",EDGE,{"disambiguationData":[TD([[subQ2,1.0]])],"derivedFrom":subQ1}),-1.0]])]});}
            var Q20;
            {var subQ1=makeQuery(id+"F1.opExtrude","CAP_EDGE",EDGE,{"disambiguationData":[OSD([sQuery(id+"F0.wireOp",EDGE,"E436.left")])],"isStart":false});var subQ5=sQuery(id+"F7.wireOp",EDGE,"E497.MirrorCS");var subQ6=makeQuery(id+"F7.imprint","INTERSECT",VERTEX,{"derivedFrom":[subQ1,subQ5]});Q20=makeQuery(id+"F7.imprint","IMPRINT",FACE,{"disambiguationData":[TD([[makeQuery(id+"F7.imprint","IMPRINT",EDGE,{"disambiguationData":[TD([[subQ6,-1.0]])],"derivedFrom":subQ5}),1.0]])]});}
            var Q21;
            {var subQ0=sQuery(id+"F7.wireOp",EDGE,"E496.MirrorCS");var subQ1=sQuery(id+"F7.wireOp",EDGE,"E494.MirrorCS");var subQ2=makeQuery(id+"F7.imprint","INTERSECT",VERTEX,{"derivedFrom":[subQ1,subQ0]});Q21=makeQuery(id+"F7.imprint","IMPRINT",FACE,{"disambiguationData":[TD([[makeQuery(id+"F7.imprint","IMPRINT",EDGE,{"disambiguationData":[TD([[subQ2,1.0]])],"derivedFrom":subQ1}),-1.0]])]});}
            var Q22;
            {var subQ0=sQuery(id+"F7.wireOp",EDGE,"E497.MirrorCS");var subQ1=makeQuery(id+"F1.opExtrude","CAP_EDGE",EDGE,{"disambiguationData":[OSD([sQuery(id+"F0.wireOp",EDGE,"E436.left")])],"isStart":false});var subQ2=makeQuery(id+"F7.imprint","INTERSECT",VERTEX,{"derivedFrom":[subQ1,subQ0]});Q22=makeQuery(id+"F7.imprint","IMPRINT",FACE,{"disambiguationData":[TD([[makeQuery(id+"F7.imprint","IMPRINT",EDGE,{"disambiguationData":[TD([[subQ2,-1.0]])],"derivedFrom":subQ0}),-1.0]])]});}
            var Q23;
            {var subQ3=sQuery(id+"F7.wireOp",EDGE,"E502");Q23=makeQuery(id+"F7.imprint","IMPRINT",FACE,{"disambiguationData":[TD([[makeQuery(id+"F7.imprint","IMPRINT",EDGE,{"derivedFrom":subQ3}),1.0]])]});}
            var Q24;
            {var subQ3=sQuery(id+"F7.wireOp",EDGE,"E503");Q24=makeQuery(id+"F7.imprint","IMPRINT",FACE,{"disambiguationData":[TD([[makeQuery(id+"F7.imprint","IMPRINT",EDGE,{"derivedFrom":subQ3}),1.0]])]});}
            var Q25;
            {var subQ0=sQuery(id+"F7.wireOp",EDGE,"E486.MirrorCS");var subQ1=makeQuery(id+"F1.opExtrude","CAP_EDGE",EDGE,{"disambiguationData":[OSD([sQuery(id+"F0.wireOp",EDGE,"E436.left")])],"isStart":false});var subQ2=makeQuery(id+"F7.imprint","INTERSECT",VERTEX,{"derivedFrom":[subQ1,subQ0]});Q25=makeQuery(id+"F7.imprint","IMPRINT",FACE,{"disambiguationData":[TD([[makeQuery(id+"F7.imprint","IMPRINT",EDGE,{"disambiguationData":[TD([[subQ2,1.0]])],"derivedFrom":subQ0}),1.0]])]});}
            extrude(context, id + "F8", {"entities" : qUnion([Q0, Q1, Q2, Q3, Q4, Q5, Q6, Q7, Q8, Q9, Q10, Q11, Q12, Q13, Q14, Q15, Q16, Q17, Q18, Q19, Q20, Q21, Q22, Q23, Q24, Q25]), "operationType" : NewBodyOperationType.ADD, "oppositeDirection" : true, "depth" : 7 * mm, "offsetDistance" : 25 * mm});
        }
        {
            var Q0;
            Q0=makeQuery(id+"F8.opExtrude","SWEPT_FACE",FACE,{"disambiguationData":[OSD([sQuery(id+"F7.wireOp",EDGE,"E491.MirrorCS")])]});
            var sketch = newSketch(context, id + "F9", { "sketchPlane" : qUnion([Q0])});
            skLineSegment(sketch, "E504.0", {"start": v(195.74, 349.03) * mm, "end": v(195.74, 334.03) * mm});
            skLineSegment(sketch, "E504.1", {"start": v(188.74, 349.03) * mm, "end": v(195.74, 349.03) * mm});
            skCircle(sketch, "E504.2", {"center": v(192.24, 344.03) * mm, "radius": 1.5 * mm});
            skLineSegment(sketch, "E504.3", {"start": v(188.74, 349.03) * mm, "end": v(188.74, 334.03) * mm});
            skLineSegment(sketch, "E504.4", {"start": v(188.74, 258.75) * mm, "end": v(188.74, 221.53) * mm});
            skLineSegment(sketch, "E504.5", {"start": v(188.74, 221.53) * mm, "end": v(195.74, 221.53) * mm});
            skLineSegment(sketch, "E504.6", {"start": v(195.74, 258.75) * mm, "end": v(195.74, 221.53) * mm});
            skCircle(sketch, "E504.7", {"center": v(192.24, 226.53) * mm, "radius": 1.5 * mm});
            skLineSegment(sketch, "E505", {"start": v(188.74, 258.75) * mm, "end": v(188.74, 334.03) * mm});
            skLineSegment(sketch, "E506", {"start": v(195.74, 258.75) * mm, "end": v(195.74, 334.03) * mm});
            skSolve(sketch);
        }
        {
            var Q0;
            {var subQ1=sQuery(id+"F9.wireOp",EDGE,"E504.4");Q0=makeQuery(id+"F9.imprint","IMPRINT",FACE,{"disambiguationData":[TD([[makeQuery(id+"F9.imprint","IMPRINT",EDGE,{"derivedFrom":subQ1}),1.0]])]});}
            var Q1;
            {var subQ1=sQuery(id+"F7.wireOp",EDGE,"E491.MirrorCS");var subQ2=makeQuery(id+"F8.opExtrude","SWEPT_EDGE",EDGE,{"disambiguationData":[OSD([sQuery(id+"F7.wireOp",EDGE,"E489.MirrorCS"),subQ1])]});Q1=makeQuery(id+"F9.imprint","IMPRINT",FACE,{"disambiguationData":[TD([[makeQuery(id+"F9.imprint","IMPRINT",EDGE,{"derivedFrom":subQ2}),-1.0]])]});}
            var Q2;
            {var subQ3=sQuery(id+"F9.wireOp",EDGE,"E504.0");Q2=makeQuery(id+"F9.imprint","IMPRINT",FACE,{"disambiguationData":[TD([[makeQuery(id+"F9.imprint","IMPRINT",EDGE,{"derivedFrom":subQ3}),-1.0]])]});}
            extrude(context, id + "F10", {"entities" : qUnion([Q0, Q1, Q2]), "operationType" : NewBodyOperationType.ADD, "depth" : 5.08 * mm, "offsetDistance" : 25 * mm});
        }
        {
            var Q0;
            Q0=makeQuery(id+"F10.opExtrude","CAP_EDGE",EDGE,{"disambiguationData":[OSD([sQuery(id+"F9.wireOp",EDGE,"E504.1")])],"isStart":false});
            var Q1;
            {var subQ0=sQuery(id+"F9.wireOp",EDGE,"E505");var subQ1=sQuery(id+"F9.wireOp",EDGE,"E504.4");var subQ2=sQuery(id+"F9.wireOp",EDGE,"E504.3");var subQ4=sQuery(id+"F7.wireOp",EDGE,"E476");Q1=makeQuery(id+"F10.boolean.opBoolean","SPLIT",EDGE,{"disambiguationData":[TD([makeQuery(id+"F8.opExtrude","SWEPT_FACE",FACE,{"disambiguationData":[OSD([subQ4])]})])],"derivedFrom":makeQuery(id+"F10.opExtrude","CAP_EDGE",EDGE,{"disambiguationData":[OSD([subQ2,subQ1,subQ0])],"isStart":true})});}
            var Q2;
            Q2=makeQuery(id+"F10.opExtrude","CAP_EDGE",EDGE,{"disambiguationData":[OSD([sQuery(id+"F9.wireOp",EDGE,"E504.3"),sQuery(id+"F9.wireOp",EDGE,"E504.4"),sQuery(id+"F9.wireOp",EDGE,"E505")])],"isStart":false});
            var Q3;
            Q3=makeQuery(id+"F10.opExtrude","CAP_EDGE",EDGE,{"disambiguationData":[OSD([sQuery(id+"F9.wireOp",EDGE,"E504.1")])],"isStart":true});
            var Q4;
            {var subQ0=sQuery(id+"F9.wireOp",EDGE,"E505");var subQ2=sQuery(id+"F9.wireOp",EDGE,"E504.4");var subQ3=sQuery(id+"F9.wireOp",EDGE,"E504.3");var subQ4=sQuery(id+"F7.wireOp",EDGE,"E501.MirrorCS");Q4=makeQuery(id+"F10.boolean.opBoolean","SPLIT",EDGE,{"disambiguationData":[TD([makeQuery(id+"F8.opExtrude","SWEPT_FACE",FACE,{"disambiguationData":[OSD([subQ4])]})])],"derivedFrom":makeQuery(id+"F10.opExtrude","CAP_EDGE",EDGE,{"disambiguationData":[OSD([subQ3,subQ2,subQ0])],"isStart":true})});}
            var Q5;
            Q5=makeQuery(id+"F10.opExtrude","SWEPT_EDGE",EDGE,{"disambiguationData":[OSD([sQuery(id+"F9.wireOp",EDGE,"E504.4"),sQuery(id+"F9.wireOp",EDGE,"E504.5")])]});
            var Q6;
            {var subQ1=sQuery(id+"F0.wireOp",EDGE,"E436.left");var subQ2=sQuery(id+"F0.wireOp",EDGE,"E436.top");Q6=makeQuery(id+"F8.boolean.opBoolean","SPLIT",EDGE,{"disambiguationData":[TD([makeQuery(id+"F1.opExtrude","SWEPT_FACE",FACE,{"disambiguationData":[OSD([subQ2])]})])],"derivedFrom":makeQuery(id+"F1.opExtrude","CAP_EDGE",EDGE,{"disambiguationData":[OSD([subQ1])],"isStart":false})});}
            var Q7;
            Q7=makeQuery(id+"F1.opExtrude","SWEPT_EDGE",EDGE,{"disambiguationData":[OSD([sQuery(id+"F0.wireOp",EDGE,"E436.top"),sQuery(id+"F0.wireOp",EDGE,"E436.left")])]});
            var Q8;
            Q8=makeQuery(id+"F1.opExtrude","CAP_EDGE",EDGE,{"disambiguationData":[OSD([sQuery(id+"F0.wireOp",EDGE,"E436.left")])],"isStart":true});
            var Q9;
            Q9=makeQuery(id+"F1.opExtrude","SWEPT_EDGE",EDGE,{"disambiguationData":[OSD([sQuery(id+"F0.wireOp",EDGE,"E436.bottom"),sQuery(id+"F0.wireOp",EDGE,"E436.left")])]});
            var Q10;
            Q10=makeQuery(id+"F1.opExtrude","CAP_EDGE",EDGE,{"disambiguationData":[OSD([sQuery(id+"F0.wireOp",EDGE,"E436.bottom")])],"isStart":false});
            var Q11;
            Q11=makeQuery(id+"F1.opExtrude","CAP_EDGE",EDGE,{"disambiguationData":[OSD([sQuery(id+"F0.wireOp",EDGE,"E436.bottom")])],"isStart":true});
            var Q12;
            Q12=makeQuery(id+"F10.opExtrude","CAP_EDGE",EDGE,{"disambiguationData":[OSD([sQuery(id+"F9.wireOp",EDGE,"E504.5")])],"isStart":false});
            var Q13;
            Q13=makeQuery(id+"F10.opExtrude","CAP_EDGE",EDGE,{"disambiguationData":[OSD([sQuery(id+"F9.wireOp",EDGE,"E504.5")])],"isStart":true});
            var Q14;
            Q14=makeQuery(id+"F1.opExtrude","CAP_EDGE",EDGE,{"disambiguationData":[OSD([sQuery(id+"F0.wireOp",EDGE,"E436.top")])],"isStart":true});
            var Q15;
            Q15=makeQuery(id+"F1.opExtrude","CAP_EDGE",EDGE,{"disambiguationData":[OSD([sQuery(id+"F0.wireOp",EDGE,"E436.top")])],"isStart":false});
            var Q16;
            Q16=makeQuery(id+"F8.opExtrude","CAP_EDGE",EDGE,{"disambiguationData":[OSD([sQuery(id+"F7.wireOp",EDGE,"E501.MirrorCS")])],"isStart":true});
            var Q17;
            Q17=makeQuery(id+"F8.opExtrude","CAP_EDGE",EDGE,{"disambiguationData":[OSD([sQuery(id+"F7.wireOp",EDGE,"E499.MirrorCS")])],"isStart":true});
            var Q18;
            Q18=makeQuery(id+"F8.opExtrude","CAP_EDGE",EDGE,{"disambiguationData":[OSD([sQuery(id+"F7.wireOp",EDGE,"E497.MirrorCS")])],"isStart":true});
            var Q19;
            Q19=makeQuery(id+"F8.opExtrude","CAP_EDGE",EDGE,{"disambiguationData":[OSD([sQuery(id+"F7.wireOp",EDGE,"E498.MirrorCS")])],"isStart":true});
            var Q20;
            Q20=makeQuery(id+"F8.opExtrude","CAP_EDGE",EDGE,{"disambiguationData":[OSD([sQuery(id+"F7.wireOp",EDGE,"E496.MirrorCS")])],"isStart":true});
            var Q21;
            Q21=makeQuery(id+"F8.opExtrude","CAP_EDGE",EDGE,{"disambiguationData":[OSD([sQuery(id+"F7.wireOp",EDGE,"E502")])],"isStart":true});
            var Q22;
            Q22=makeQuery(id+"F8.opExtrude","CAP_EDGE",EDGE,{"disambiguationData":[OSD([sQuery(id+"F7.wireOp",EDGE,"E489.MirrorCS")])],"isStart":true});
            var Q23;
            Q23=makeQuery(id+"F8.opExtrude","CAP_EDGE",EDGE,{"disambiguationData":[OSD([sQuery(id+"F7.wireOp",EDGE,"E494.MirrorCS")])],"isStart":true});
            var Q24;
            {var subQ0=sQuery(id+"F7.wireOp",EDGE,"E489.MirrorCS");var subQ3=sQuery(id+"F9.wireOp",EDGE,"E505");var subQ4=sQuery(id+"F9.wireOp",EDGE,"E504.4");var subQ5=sQuery(id+"F9.wireOp",EDGE,"E504.3");Q24=makeQuery(id+"F10.boolean.opBoolean","SPLIT",EDGE,{"disambiguationData":[TD([makeQuery(id+"F8.opExtrude","SWEPT_FACE",FACE,{"disambiguationData":[OSD([subQ0])]})])],"derivedFrom":makeQuery(id+"F10.opExtrude","CAP_EDGE",EDGE,{"disambiguationData":[OSD([subQ5,subQ4,subQ3])],"isStart":true})});}
            var Q25;
            Q25=makeQuery(id+"F8.opExtrude","CAP_EDGE",EDGE,{"disambiguationData":[OSD([sQuery(id+"F7.wireOp",EDGE,"E490.MirrorCS")])],"isStart":true});
            var Q26;
            Q26=makeQuery(id+"F8.opExtrude","CAP_EDGE",EDGE,{"disambiguationData":[OSD([sQuery(id+"F7.wireOp",EDGE,"E486.MirrorCS")])],"isStart":true});
            var Q27;
            Q27=makeQuery(id+"F8.opExtrude","CAP_EDGE",EDGE,{"disambiguationData":[OSD([sQuery(id+"F7.wireOp",EDGE,"E488.MirrorCS")])],"isStart":true});
            var Q28;
            Q28=makeQuery(id+"F8.opExtrude","CAP_EDGE",EDGE,{"disambiguationData":[OSD([sQuery(id+"F7.wireOp",EDGE,"E492.MirrorCS")])],"isStart":true});
            var Q29;
            Q29=makeQuery(id+"F8.opExtrude","CAP_EDGE",EDGE,{"disambiguationData":[OSD([sQuery(id+"F7.wireOp",EDGE,"E503")])],"isStart":true});
            var Q30;
            Q30=makeQuery(id+"F8.opExtrude","CAP_EDGE",EDGE,{"disambiguationData":[OSD([sQuery(id+"F7.wireOp",EDGE,"E485.MirrorCS")])],"isStart":true});
            var Q31;
            Q31=makeQuery(id+"F8.opExtrude","CAP_EDGE",EDGE,{"disambiguationData":[OSD([sQuery(id+"F7.wireOp",EDGE,"E477")])],"isStart":true});
            var Q32;
            {var subQ1=sQuery(id+"F7.wireOp",EDGE,"E477");var subQ3=sQuery(id+"F9.wireOp",EDGE,"E505");var subQ4=sQuery(id+"F9.wireOp",EDGE,"E504.4");var subQ5=sQuery(id+"F9.wireOp",EDGE,"E504.3");Q32=makeQuery(id+"F10.boolean.opBoolean","SPLIT",EDGE,{"disambiguationData":[TD([makeQuery(id+"F8.opExtrude","SWEPT_FACE",FACE,{"disambiguationData":[OSD([subQ1])]})])],"derivedFrom":makeQuery(id+"F10.opExtrude","CAP_EDGE",EDGE,{"disambiguationData":[OSD([subQ5,subQ4,subQ3])],"isStart":true})});}
            var Q33;
            Q33=makeQuery(id+"F8.opExtrude","CAP_EDGE",EDGE,{"disambiguationData":[OSD([sQuery(id+"F7.wireOp",EDGE,"E482")])],"isStart":true});
            var Q34;
            Q34=makeQuery(id+"F8.opExtrude","CAP_EDGE",EDGE,{"disambiguationData":[OSD([sQuery(id+"F7.wireOp",EDGE,"E479")])],"isStart":true});
            var Q35;
            Q35=makeQuery(id+"F8.opExtrude","CAP_EDGE",EDGE,{"disambiguationData":[OSD([sQuery(id+"F7.wireOp",EDGE,"E483")])],"isStart":true});
            var Q36;
            Q36=makeQuery(id+"F8.opExtrude","CAP_EDGE",EDGE,{"disambiguationData":[OSD([sQuery(id+"F7.wireOp",EDGE,"E480")])],"isStart":true});
            var Q37;
            Q37=makeQuery(id+"F8.opExtrude","CAP_EDGE",EDGE,{"disambiguationData":[OSD([sQuery(id+"F7.wireOp",EDGE,"E476")])],"isStart":true});
            var Q38;
            {var subQ1=sQuery(id+"F0.wireOp",EDGE,"E436.left");var subQ2=sQuery(id+"F0.wireOp",EDGE,"E436.bottom");Q38=makeQuery(id+"F8.boolean.opBoolean","SPLIT",EDGE,{"disambiguationData":[TD([makeQuery(id+"F1.opExtrude","SWEPT_FACE",FACE,{"disambiguationData":[OSD([subQ2])]})])],"derivedFrom":makeQuery(id+"F1.opExtrude","CAP_EDGE",EDGE,{"disambiguationData":[OSD([subQ1])],"isStart":false})});}
            var Q39;
            Q39=makeQuery(id+"F10.opExtrude","SWEPT_EDGE",EDGE,{"disambiguationData":[OSD([sQuery(id+"F9.wireOp",EDGE,"E504.1"),sQuery(id+"F9.wireOp",EDGE,"E504.3")])]});
            fillet(context, id + "F11", {"entities" : qUnion([Q0, Q1, Q2, Q3, Q4, Q5, Q6, Q7, Q8, Q9, Q10, Q11, Q12, Q13, Q14, Q15, Q16, Q17, Q18, Q19, Q20, Q21, Q22, Q23, Q24, Q25, Q26, Q27, Q28, Q29, Q30, Q31, Q32, Q33, Q34, Q35, Q36, Q37, Q38, Q39]), "radius" : 2 * mm, "tangentPropagation" : true, "allowEdgeOverflow" : false});
        }
        {
            var Q0;
            Q0=makeQuery(id+"F1.opExtrude","SWEPT_FACE",FACE,{"disambiguationData":[OSD([sQuery(id+"F0.wireOp",EDGE,"E441"),sQuery(id+"F0.wireOp",EDGE,"E449")])]});
            var sketch = newSketch(context, id + "F12", { "sketchPlane" : qUnion([Q0])});
            skLineSegment(sketch, "E507", {"start": v(-220.14, 39.55) * mm, "end": v(-232.69, 5.08) * mm});
            skLineSegment(sketch, "E508", {"start": v(-220.14, 39.55) * mm, "end": v(-220.14, 5.08) * mm, "construction": true});
            skLineSegment(sketch, "E509.MirrorCS", {"start": v(-220.14, 39.55) * mm, "end": v(-207.6, 5.08) * mm});
            skLineSegment(sketch, "E510", {"start": v(-225.69, 5.08) * mm, "end": v(-220.14, 20.32) * mm});
            skLineSegment(sketch, "E511.MirrorCS", {"start": v(-214.6, 5.08) * mm, "end": v(-220.14, 20.32) * mm});
            skLineSegment(sketch, "E512", {"start": v(-227.14, 20.32) * mm, "end": v(-213.14, 20.32) * mm});
            skLineSegment(sketch, "E513", {"start": v(-227.87, 18.32) * mm, "end": v(-212.41, 18.32) * mm});
            skLineSegment(sketch, "E514", {"start": v(-231.96, 7.08) * mm, "end": v(-208.32, 7.08) * mm});
            skLineSegment(sketch, "E515", {"start": v(-207.6, 5.08) * mm, "end": v(-207.6, 39.55) * mm, "construction": true});
            skLineSegment(sketch, "E516", {"start": v(-208.32, 7.08) * mm, "end": v(-207.6, 7.08) * mm});
            skLineSegment(sketch, "E517.MirrorCS", {"start": v(-188.05, 20.32) * mm, "end": v(-202.05, 20.32) * mm});
            skLineSegment(sketch, "E518.MirrorCS", {"start": v(-187.32, 18.32) * mm, "end": v(-202.77, 18.32) * mm});
            skLineSegment(sketch, "E519.MirrorCS", {"start": v(-200.6, 5.08) * mm, "end": v(-195.05, 20.32) * mm});
            skLineSegment(sketch, "E520.MirrorCS", {"start": v(-189.5, 5.08) * mm, "end": v(-195.05, 20.32) * mm});
            skLineSegment(sketch, "E521.MirrorCS", {"start": v(-195.05, 39.55) * mm, "end": v(-182.5, 5.08) * mm});
            skLineSegment(sketch, "E522.MirrorCS", {"start": v(-195.05, 39.55) * mm, "end": v(-207.6, 5.08) * mm});
            skLineSegment(sketch, "E523.MirrorCS", {"start": v(-183.23, 7.08) * mm, "end": v(-206.87, 7.08) * mm});
            skLineSegment(sketch, "E524.MirrorCS", {"start": v(-206.87, 7.08) * mm, "end": v(-207.6, 7.08) * mm});
            skSolve(sketch);
        }
        {
            var Q0;
            {var subQ0=sQuery(id+"F12.wireOp",EDGE,"E512");var subQ1=sQuery(id+"F12.wireOp",EDGE,"E509.MirrorCS");var subQ2=makeQuery(id+"F12.imprint","INTERSECT",VERTEX,{"derivedFrom":[subQ1,subQ0]});Q0=makeQuery(id+"F12.imprint","IMPRINT",FACE,{"disambiguationData":[TD([[makeQuery(id+"F12.imprint","IMPRINT",EDGE,{"disambiguationData":[TD([[subQ2,-1.0]])],"derivedFrom":subQ1}),-1.0]])]});}
            var Q1;
            {var subQ0=sQuery(id+"F12.wireOp",EDGE,"E512");var subQ1=sQuery(id+"F12.wireOp",EDGE,"E507");var subQ2=makeQuery(id+"F12.imprint","INTERSECT",VERTEX,{"derivedFrom":[subQ1,subQ0]});Q1=makeQuery(id+"F12.imprint","IMPRINT",FACE,{"disambiguationData":[TD([[makeQuery(id+"F12.imprint","IMPRINT",EDGE,{"disambiguationData":[TD([[subQ2,-1.0]])],"derivedFrom":subQ1}),1.0]])]});}
            var Q2;
            {var subQ1=sQuery(id+"F12.wireOp",EDGE,"E510");var subQ3=sQuery(id+"F12.wireOp",EDGE,"E513");var subQ4=makeQuery(id+"F12.imprint","INTERSECT",VERTEX,{"derivedFrom":[subQ1,subQ3]});Q2=makeQuery(id+"F12.imprint","IMPRINT",FACE,{"disambiguationData":[TD([[makeQuery(id+"F12.imprint","IMPRINT",EDGE,{"disambiguationData":[TD([[subQ4,-1.0]])],"derivedFrom":subQ3}),1.0]])]});}
            var Q3;
            {var subQ0=sQuery(id+"F12.wireOp",EDGE,"E513");var subQ1=sQuery(id+"F12.wireOp",EDGE,"E509.MirrorCS");var subQ2=makeQuery(id+"F12.imprint","INTERSECT",VERTEX,{"derivedFrom":[subQ1,subQ0]});Q3=makeQuery(id+"F12.imprint","IMPRINT",FACE,{"disambiguationData":[TD([[makeQuery(id+"F12.imprint","IMPRINT",EDGE,{"disambiguationData":[TD([[subQ2,-1.0]])],"derivedFrom":subQ1}),-1.0]])]});}
            var Q4;
            {var subQ0=sQuery(id+"F12.wireOp",EDGE,"E513");var subQ1=sQuery(id+"F12.wireOp",EDGE,"E507");var subQ2=makeQuery(id+"F12.imprint","INTERSECT",VERTEX,{"derivedFrom":[subQ1,subQ0]});Q4=makeQuery(id+"F12.imprint","IMPRINT",FACE,{"disambiguationData":[TD([[makeQuery(id+"F12.imprint","IMPRINT",EDGE,{"disambiguationData":[TD([[subQ2,-1.0]])],"derivedFrom":subQ1}),1.0]])]});}
            var Q5;
            {var subQ0=sQuery(id+"F12.wireOp",EDGE,"E507");var subQ3=sQuery(id+"F12.wireOp",EDGE,"E514");var subQ4=makeQuery(id+"F12.imprint","INTERSECT",VERTEX,{"derivedFrom":[subQ0,subQ3]});Q5=makeQuery(id+"F12.imprint","IMPRINT",FACE,{"disambiguationData":[TD([[makeQuery(id+"F12.imprint","IMPRINT",EDGE,{"disambiguationData":[TD([[subQ4,-1.0]])],"derivedFrom":subQ3}),-1.0]])]});}
            var Q6;
            {var subQ0=sQuery(id+"F12.wireOp",EDGE,"E510");var subQ3=sQuery(id+"F12.wireOp",EDGE,"E514");var subQ4=makeQuery(id+"F12.imprint","INTERSECT",VERTEX,{"derivedFrom":[subQ0,subQ3]});Q6=makeQuery(id+"F12.imprint","IMPRINT",FACE,{"disambiguationData":[TD([[makeQuery(id+"F12.imprint","IMPRINT",EDGE,{"disambiguationData":[TD([[subQ4,-1.0]])],"derivedFrom":subQ3}),-1.0]])]});}
            var Q7;
            {var subQ0=sQuery(id+"F12.wireOp",EDGE,"E509.MirrorCS");var subQ3=sQuery(id+"F12.wireOp",EDGE,"E514");var subQ4=makeQuery(id+"F12.imprint","INTERSECT",VERTEX,{"derivedFrom":[subQ0,subQ3]});Q7=makeQuery(id+"F12.imprint","IMPRINT",FACE,{"disambiguationData":[TD([[makeQuery(id+"F12.imprint","IMPRINT",EDGE,{"disambiguationData":[TD([[subQ4,1.0]])],"derivedFrom":subQ3}),-1.0]])]});}
            var Q8;
            {var subQ0=sQuery(id+"F12.wireOp",EDGE,"E522.MirrorCS");var subQ1=sQuery(id+"F12.wireOp",EDGE,"E518.MirrorCS");var subQ2=makeQuery(id+"F12.imprint","INTERSECT",VERTEX,{"derivedFrom":[subQ1,subQ0]});Q8=makeQuery(id+"F12.imprint","IMPRINT",FACE,{"disambiguationData":[TD([[makeQuery(id+"F12.imprint","IMPRINT",EDGE,{"disambiguationData":[TD([[subQ2,1.0]])],"derivedFrom":subQ1}),1.0]])]});}
            var Q9;
            {var subQ0=sQuery(id+"F12.wireOp",EDGE,"E522.MirrorCS");var subQ5=sQuery(id+"F12.wireOp",EDGE,"E518.MirrorCS");var subQ7=makeQuery(id+"F12.imprint","INTERSECT",VERTEX,{"derivedFrom":[subQ5,subQ0]});Q9=makeQuery(id+"F12.imprint","IMPRINT",FACE,{"disambiguationData":[TD([[makeQuery(id+"F12.imprint","IMPRINT",EDGE,{"disambiguationData":[TD([[subQ7,1.0]])],"derivedFrom":subQ5}),-1.0]])]});}
            var Q10;
            {var subQ0=sQuery(id+"F12.wireOp",EDGE,"E521.MirrorCS");var subQ5=sQuery(id+"F12.wireOp",EDGE,"E518.MirrorCS");var subQ6=makeQuery(id+"F12.imprint","INTERSECT",VERTEX,{"derivedFrom":[subQ5,subQ0]});Q10=makeQuery(id+"F12.imprint","IMPRINT",FACE,{"disambiguationData":[TD([[makeQuery(id+"F12.imprint","IMPRINT",EDGE,{"disambiguationData":[TD([[subQ6,-1.0]])],"derivedFrom":subQ5}),-1.0]])]});}
            var Q11;
            {var subQ0=sQuery(id+"F12.wireOp",EDGE,"E521.MirrorCS");var subQ1=sQuery(id+"F12.wireOp",EDGE,"E518.MirrorCS");var subQ2=makeQuery(id+"F12.imprint","INTERSECT",VERTEX,{"derivedFrom":[subQ1,subQ0]});Q11=makeQuery(id+"F12.imprint","IMPRINT",FACE,{"disambiguationData":[TD([[makeQuery(id+"F12.imprint","IMPRINT",EDGE,{"disambiguationData":[TD([[subQ2,-1.0]])],"derivedFrom":subQ1}),1.0]])]});}
            var Q12;
            {var subQ0=sQuery(id+"F12.wireOp",EDGE,"E520.MirrorCS");var subQ1=sQuery(id+"F12.wireOp",EDGE,"E518.MirrorCS");var subQ2=makeQuery(id+"F12.imprint","INTERSECT",VERTEX,{"derivedFrom":[subQ1,subQ0]});Q12=makeQuery(id+"F12.imprint","IMPRINT",FACE,{"disambiguationData":[TD([[makeQuery(id+"F12.imprint","IMPRINT",EDGE,{"disambiguationData":[TD([[subQ2,-1.0]])],"derivedFrom":subQ1}),-1.0]])]});}
            var Q13;
            {var subQ3=sQuery(id+"F12.wireOp",EDGE,"E516");Q13=makeQuery(id+"F12.imprint","IMPRINT",FACE,{"disambiguationData":[TD([[makeQuery(id+"F12.imprint","IMPRINT",EDGE,{"derivedFrom":subQ3}),-1.0]])]});}
            var Q14;
            {var subQ0=sQuery(id+"F12.wireOp",EDGE,"E519.MirrorCS");var subQ3=sQuery(id+"F12.wireOp",EDGE,"E523.MirrorCS");var subQ4=makeQuery(id+"F12.imprint","INTERSECT",VERTEX,{"derivedFrom":[subQ0,subQ3]});Q14=makeQuery(id+"F12.imprint","IMPRINT",FACE,{"disambiguationData":[TD([[makeQuery(id+"F12.imprint","IMPRINT",EDGE,{"disambiguationData":[TD([[subQ4,1.0]])],"derivedFrom":subQ0}),1.0]])]});}
            var Q15;
            {var subQ0=sQuery(id+"F12.wireOp",EDGE,"E519.MirrorCS");var subQ3=sQuery(id+"F12.wireOp",EDGE,"E523.MirrorCS");var subQ4=makeQuery(id+"F12.imprint","INTERSECT",VERTEX,{"derivedFrom":[subQ0,subQ3]});Q15=makeQuery(id+"F12.imprint","IMPRINT",FACE,{"disambiguationData":[TD([[makeQuery(id+"F12.imprint","IMPRINT",EDGE,{"disambiguationData":[TD([[subQ4,1.0]])],"derivedFrom":subQ3}),1.0]])]});}
            var Q16;
            {var subQ3=sQuery(id+"F12.wireOp",EDGE,"E523.MirrorCS");var subQ5=sQuery(id+"F12.wireOp",EDGE,"E521.MirrorCS");var subQ7=makeQuery(id+"F12.imprint","INTERSECT",VERTEX,{"derivedFrom":[subQ5,subQ3]});Q16=makeQuery(id+"F12.imprint","IMPRINT",FACE,{"disambiguationData":[TD([[makeQuery(id+"F12.imprint","IMPRINT",EDGE,{"disambiguationData":[TD([[subQ7,-1.0]])],"derivedFrom":subQ3}),1.0]])]});}
            var Q17;
            Q17=makeQuery(id+"F1.opExtrude","SWEPT_FACE",FACE,{"disambiguationData":[OSD([sQuery(id+"F0.wireOp",EDGE,"E443"),sQuery(id+"F0.wireOp",EDGE,"E448")])]});
            extrude(context, id + "F13", {"entities" : qUnion([Q0, Q1, Q2, Q3, Q4, Q5, Q6, Q7, Q8, Q9, Q10, Q11, Q12, Q13, Q14, Q15, Q16]), "endBound" : BoundingType.UP_TO_SURFACE, "oppositeDirection" : true, "depth" : 7 * mm, "endBoundEntityFace" : qUnion([Q17]), "offsetDistance" : 25 * mm});
        }
        {
            var Q0;
            Q0=makeQuery(id+"F13.opExtrude","SWEPT_BODY",BODY,{"disambiguationData":[OSD([sQuery(id+"F0.wireOp",EDGE,"E441"),sQuery(id+"F0.wireOp",EDGE,"E449"),sQuery(id+"F12.wireOp",EDGE,"E507"),sQuery(id+"F12.wireOp",EDGE,"E509.MirrorCS"),sQuery(id+"F12.wireOp",EDGE,"E510"),sQuery(id+"F12.wireOp",EDGE,"E511.MirrorCS"),sQuery(id+"F12.wireOp",EDGE,"E512"),sQuery(id+"F12.wireOp",EDGE,"E513"),sQuery(id+"F12.wireOp",EDGE,"E514"),sQuery(id+"F12.wireOp",EDGE,"E516"),sQuery(id+"F12.wireOp",EDGE,"E517.MirrorCS"),sQuery(id+"F12.wireOp",EDGE,"E518.MirrorCS"),sQuery(id+"F12.wireOp",EDGE,"E519.MirrorCS"),sQuery(id+"F12.wireOp",EDGE,"E520.MirrorCS"),sQuery(id+"F12.wireOp",EDGE,"E521.MirrorCS"),sQuery(id+"F12.wireOp",EDGE,"E522.MirrorCS"),sQuery(id+"F12.wireOp",EDGE,"E523.MirrorCS"),sQuery(id+"F12.wireOp",EDGE,"E524.MirrorCS")])]});
            var Q1;
            Q1=makeQuery(id+"F1.opExtrude","SWEPT_BODY",BODY,{"disambiguationData":[OSD([sQuery(id+"F0.wireOp",EDGE,"E439.top"),sQuery(id+"F0.wireOp",EDGE,"E440"),sQuery(id+"F0.wireOp",EDGE,"E441"),sQuery(id+"F0.wireOp",EDGE,"E442"),sQuery(id+"F0.wireOp",EDGE,"E443"),sQuery(id+"F0.wireOp",EDGE,"E444"),sQuery(id+"F0.wireOp",EDGE,"E445"),sQuery(id+"F0.wireOp",EDGE,"E447"),sQuery(id+"F0.wireOp",EDGE,"E448"),sQuery(id+"F0.wireOp",EDGE,"E449")])]});
            booleanBodies(context, id + "F14", {"operationType" : BooleanOperationType.UNION, "tools" : qUnion([Q0, Q1])});
        }
        {
            var Q0;
            Q0=makeQuery(id+"F13.opExtrude","SWEPT_FACE",FACE,{"disambiguationData":[OSD([sQuery(id+"F12.wireOp",EDGE,"E512")])]});
            var sketch = newSketch(context, id + "F15", { "sketchPlane" : qUnion([Q0])});
            skLineSegment(sketch, "E525.0", {"start": v(261.86, 182.5) * mm, "end": v(261.86, 157.93) * mm});
            skLineSegment(sketch, "E525.1", {"start": v(268.86, 157.93) * mm, "end": v(268.86, 182.5) * mm});
            skLineSegment(sketch, "E525.2", {"start": v(261.86, 157.93) * mm, "end": v(268.86, 157.93) * mm});
            skCircle(sketch, "E525.3", {"center": v(265.36, 162.93) * mm, "radius": 1.5 * mm});
            skCircle(sketch, "E525.4", {"center": v(265.36, 290.23) * mm, "radius": 1.5 * mm});
            skCircle(sketch, "E525.5", {"center": v(265.36, 302.93) * mm, "radius": 1.5 * mm});
            skCircle(sketch, "E525.6", {"center": v(265.36, 315.63) * mm, "radius": 1.5 * mm});
            skLineSegment(sketch, "E525.7", {"start": v(261.86, 322.93) * mm, "end": v(261.86, 232.69) * mm});
            skLineSegment(sketch, "E525.8", {"start": v(268.86, 232.69) * mm, "end": v(268.86, 322.93) * mm});
            skLineSegment(sketch, "E525.9", {"start": v(261.86, 322.93) * mm, "end": v(268.86, 322.93) * mm});
            skLineSegment(sketch, "E526", {"start": v(261.86, 182.5) * mm, "end": v(261.86, 232.69) * mm});
            skLineSegment(sketch, "E527", {"start": v(268.86, 182.5) * mm, "end": v(268.86, 232.69) * mm});
            skSolve(sketch);
        }
        {
            var Q0;
            Q0=makeQuery(id+"F15.imprint","IMPRINT",FACE,{"disambiguationData":[TD([[makeQuery(id+"F15.imprint","IMPRINT",EDGE,{"derivedFrom":sQuery(id+"F15.wireOp",EDGE,"E525.4")}),-1.0]])]});
            var Q1;
            {var subQ3=sQuery(id+"F15.wireOp",EDGE,"E525.0");Q1=makeQuery(id+"F15.imprint","IMPRINT",FACE,{"disambiguationData":[TD([[makeQuery(id+"F15.imprint","IMPRINT",EDGE,{"derivedFrom":subQ3}),1.0]])]});}
            var Q2;
            {var subQ1=sQuery(id+"F12.wireOp",EDGE,"E512");var subQ2=makeQuery(id+"F13.opExtrude","SWEPT_EDGE",EDGE,{"disambiguationData":[OSD([sQuery(id+"F12.wireOp",EDGE,"E507"),subQ1])]});Q2=makeQuery(id+"F15.imprint","IMPRINT",FACE,{"disambiguationData":[TD([[makeQuery(id+"F15.imprint","IMPRINT",EDGE,{"derivedFrom":subQ2}),1.0]])]});}
            extrude(context, id + "F16", {"entities" : qUnion([Q0, Q1, Q2]), "operationType" : NewBodyOperationType.ADD, "depth" : 5.08 * mm, "offsetDistance" : 25 * mm});
        }
        {
            var Q0;
            Q0=makeQuery(id+"F16.opExtrude","CAP_EDGE",EDGE,{"disambiguationData":[OSD([sQuery(id+"F15.wireOp",EDGE,"E525.0"),sQuery(id+"F15.wireOp",EDGE,"E525.7"),sQuery(id+"F15.wireOp",EDGE,"E526")])],"isStart":false});
            var Q1;
            {var subQ0=sQuery(id+"F15.wireOp",EDGE,"E526");var subQ1=sQuery(id+"F15.wireOp",EDGE,"E525.7");var subQ3=sQuery(id+"F15.wireOp",EDGE,"E525.0");var subQ4=sQuery(id+"F12.wireOp",EDGE,"E521.MirrorCS");Q1=makeQuery(id+"F16.boolean.opBoolean","SPLIT",EDGE,{"disambiguationData":[TD([makeQuery(id+"F13.opExtrude","SWEPT_FACE",FACE,{"disambiguationData":[OSD([subQ4])]})])],"derivedFrom":makeQuery(id+"F16.opExtrude","CAP_EDGE",EDGE,{"disambiguationData":[OSD([subQ3,subQ1,subQ0])],"isStart":true})});}
            var Q2;
            Q2=makeQuery(id+"F13.opExtrude","CAP_EDGE",EDGE,{"disambiguationData":[OSD([sQuery(id+"F12.wireOp",EDGE,"E521.MirrorCS")])],"isStart":true});
            var Q3;
            {var subQ1=sQuery(id+"F0.wireOp",EDGE,"E449");var subQ2=sQuery(id+"F0.wireOp",EDGE,"E441");var subQ3=sQuery(id+"F0.wireOp",EDGE,"E439.top");Q3=makeQuery(id+"F14.opBoolean","SPLIT",EDGE,{"disambiguationData":[TD([makeQuery(id+"F1.opExtrude","SWEPT_FACE",FACE,{"disambiguationData":[OSD([subQ3])]})])],"derivedFrom":makeQuery(id+"F1.opExtrude","CAP_EDGE",EDGE,{"disambiguationData":[OSD([subQ2,subQ1])],"isStart":false})});}
            var Q4;
            Q4=makeQuery(id+"F1.opExtrude","SWEPT_EDGE",EDGE,{"disambiguationData":[OSD([sQuery(id+"F0.wireOp",EDGE,"E439.top"),sQuery(id+"F0.wireOp",EDGE,"E449")])]});
            var Q5;
            Q5=makeQuery(id+"F13.opExtrude","SWEPT_EDGE",EDGE,{"disambiguationData":[OSD([sQuery(id+"F0.wireOp",EDGE,"E441"),sQuery(id+"F0.wireOp",EDGE,"E449"),sQuery(id+"F12.wireOp",EDGE,"E521.MirrorCS")])]});
            var Q6;
            Q6=makeQuery(id+"F1.opExtrude","CAP_EDGE",EDGE,{"disambiguationData":[OSD([sQuery(id+"F0.wireOp",EDGE,"E439.top")])],"isStart":false});
            var Q7;
            Q7=makeQuery(id+"F16.opExtrude","CAP_EDGE",EDGE,{"disambiguationData":[OSD([sQuery(id+"F15.wireOp",EDGE,"E525.2")])],"isStart":false});
            var Q8;
            Q8=makeQuery(id+"F16.opExtrude","CAP_EDGE",EDGE,{"disambiguationData":[OSD([sQuery(id+"F15.wireOp",EDGE,"E525.2")])],"isStart":true});
            var Q9;
            Q9=makeQuery(id+"F1.opExtrude","CAP_EDGE",EDGE,{"disambiguationData":[OSD([sQuery(id+"F0.wireOp",EDGE,"E439.top")])],"isStart":true});
            var Q10;
            Q10=makeQuery(id+"F16.opExtrude","SWEPT_EDGE",EDGE,{"disambiguationData":[OSD([sQuery(id+"F15.wireOp",EDGE,"E525.0"),sQuery(id+"F15.wireOp",EDGE,"E525.2")])]});
            var Q11;
            Q11=makeQuery(id+"F13.opExtrude","CAP_EDGE",EDGE,{"disambiguationData":[OSD([sQuery(id+"F12.wireOp",EDGE,"E516"),sQuery(id+"F12.wireOp",EDGE,"E524.MirrorCS")])],"isStart":true});
            var Q12;
            Q12=makeQuery(id+"F13.opExtrude","CAP_EDGE",EDGE,{"disambiguationData":[OSD([sQuery(id+"F12.wireOp",EDGE,"E522.MirrorCS")])],"isStart":true});
            var Q13;
            Q13=makeQuery(id+"F13.opExtrude","CAP_EDGE",EDGE,{"disambiguationData":[OSD([sQuery(id+"F12.wireOp",EDGE,"E509.MirrorCS")])],"isStart":true});
            var Q14;
            {var subQ0=sQuery(id+"F12.wireOp",EDGE,"E509.MirrorCS");var subQ4=sQuery(id+"F15.wireOp",EDGE,"E526");var subQ5=sQuery(id+"F15.wireOp",EDGE,"E525.7");var subQ6=sQuery(id+"F15.wireOp",EDGE,"E525.0");Q14=makeQuery(id+"F16.boolean.opBoolean","SPLIT",EDGE,{"disambiguationData":[TD([makeQuery(id+"F13.opExtrude","SWEPT_FACE",FACE,{"disambiguationData":[OSD([subQ0])]})])],"derivedFrom":makeQuery(id+"F16.opExtrude","CAP_EDGE",EDGE,{"disambiguationData":[OSD([subQ6,subQ5,subQ4])],"isStart":true})});}
            var Q15;
            Q15=makeQuery(id+"F13.opExtrude","CAP_EDGE",EDGE,{"disambiguationData":[OSD([sQuery(id+"F12.wireOp",EDGE,"E518.MirrorCS")])],"isStart":true});
            var Q16;
            Q16=makeQuery(id+"F13.opExtrude","CAP_EDGE",EDGE,{"disambiguationData":[OSD([sQuery(id+"F12.wireOp",EDGE,"E520.MirrorCS")])],"isStart":true});
            var Q17;
            Q17=makeQuery(id+"F13.opExtrude","CAP_EDGE",EDGE,{"disambiguationData":[OSD([sQuery(id+"F12.wireOp",EDGE,"E519.MirrorCS")])],"isStart":true});
            var Q18;
            Q18=makeQuery(id+"F13.opExtrude","CAP_EDGE",EDGE,{"disambiguationData":[OSD([sQuery(id+"F12.wireOp",EDGE,"E514")])],"isStart":true});
            var Q19;
            Q19=makeQuery(id+"F13.opExtrude","CAP_EDGE",EDGE,{"disambiguationData":[OSD([sQuery(id+"F12.wireOp",EDGE,"E511.MirrorCS")])],"isStart":true});
            var Q20;
            Q20=makeQuery(id+"F13.opExtrude","CAP_EDGE",EDGE,{"disambiguationData":[OSD([sQuery(id+"F12.wireOp",EDGE,"E510")])],"isStart":true});
            var Q21;
            Q21=makeQuery(id+"F13.opExtrude","CAP_EDGE",EDGE,{"disambiguationData":[OSD([sQuery(id+"F12.wireOp",EDGE,"E513")])],"isStart":true});
            var Q22;
            Q22=makeQuery(id+"F1.opExtrude","CAP_EDGE",EDGE,{"disambiguationData":[OSD([sQuery(id+"F0.wireOp",EDGE,"E441"),sQuery(id+"F0.wireOp",EDGE,"E449")])],"isStart":true});
            var Q23;
            Q23=makeQuery(id+"F13.opExtrude","CAP_EDGE",EDGE,{"disambiguationData":[OSD([sQuery(id+"F12.wireOp",EDGE,"E507")])],"isStart":true});
            var Q24;
            {var subQ1=sQuery(id+"F0.wireOp",EDGE,"E449");var subQ2=sQuery(id+"F0.wireOp",EDGE,"E442");var subQ3=sQuery(id+"F0.wireOp",EDGE,"E441");Q24=makeQuery(id+"F14.opBoolean","SPLIT",EDGE,{"disambiguationData":[TD([makeQuery(id+"F1.opExtrude","SWEPT_FACE",FACE,{"disambiguationData":[OSD([subQ2])]})])],"derivedFrom":makeQuery(id+"F1.opExtrude","CAP_EDGE",EDGE,{"disambiguationData":[OSD([subQ3,subQ1])],"isStart":false})});}
            var Q25;
            {var subQ0=sQuery(id+"F15.wireOp",EDGE,"E526");var subQ2=sQuery(id+"F15.wireOp",EDGE,"E525.7");var subQ3=sQuery(id+"F15.wireOp",EDGE,"E525.0");var subQ4=sQuery(id+"F12.wireOp",EDGE,"E507");Q25=makeQuery(id+"F16.boolean.opBoolean","SPLIT",EDGE,{"disambiguationData":[TD([makeQuery(id+"F13.opExtrude","SWEPT_FACE",FACE,{"disambiguationData":[OSD([subQ4])]})])],"derivedFrom":makeQuery(id+"F16.opExtrude","CAP_EDGE",EDGE,{"disambiguationData":[OSD([subQ3,subQ2,subQ0])],"isStart":true})});}
            var Q26;
            Q26=makeQuery(id+"F1.opExtrude","CAP_EDGE",EDGE,{"disambiguationData":[OSD([sQuery(id+"F0.wireOp",EDGE,"E442")])],"isStart":false});
            var Q27;
            Q27=makeQuery(id+"F1.opExtrude","SWEPT_EDGE",EDGE,{"disambiguationData":[OSD([sQuery(id+"F0.wireOp",EDGE,"E441"),sQuery(id+"F0.wireOp",EDGE,"E442")])]});
            var Q28;
            Q28=makeQuery(id+"F1.opExtrude","CAP_EDGE",EDGE,{"disambiguationData":[OSD([sQuery(id+"F0.wireOp",EDGE,"E442")])],"isStart":true});
            var Q29;
            Q29=makeQuery(id+"F16.opExtrude","CAP_EDGE",EDGE,{"disambiguationData":[OSD([sQuery(id+"F15.wireOp",EDGE,"E525.9")])],"isStart":false});
            var Q30;
            Q30=makeQuery(id+"F16.opExtrude","CAP_EDGE",EDGE,{"disambiguationData":[OSD([sQuery(id+"F15.wireOp",EDGE,"E525.9")])],"isStart":true});
            var Q31;
            Q31=makeQuery(id+"F16.opExtrude","SWEPT_EDGE",EDGE,{"disambiguationData":[OSD([sQuery(id+"F15.wireOp",EDGE,"E525.7"),sQuery(id+"F15.wireOp",EDGE,"E525.9")])]});
            var Q32;
            Q32=makeQuery(id+"F13.opExtrude","CAP_EDGE",EDGE,{"disambiguationData":[OSD([sQuery(id+"F12.wireOp",EDGE,"E523.MirrorCS")])],"isStart":true});
            fillet(context, id + "F17", {"entities" : qUnion([Q0, Q1, Q2, Q3, Q4, Q5, Q6, Q7, Q8, Q9, Q10, Q11, Q12, Q13, Q14, Q15, Q16, Q17, Q18, Q19, Q20, Q21, Q22, Q23, Q24, Q25, Q26, Q27, Q28, Q29, Q30, Q31, Q32]), "radius" : 2 * mm, "tangentPropagation" : true, "allowEdgeOverflow" : false});
        }
        {
            var Q0;
            Q0=makeQuery(id+"F1.opExtrude","CAP_FACE",FACE,{"disambiguationData":[OSD([sQuery(id+"F0.wireOp",EDGE,"E0.bottom"),sQuery(id+"F0.wireOp",EDGE,"E0.top"),sQuery(id+"F0.wireOp",EDGE,"E0.left"),sQuery(id+"F0.wireOp",EDGE,"E0.right"),sQuery(id+"F0.wireOp",EDGE,"E1"),sQuery(id+"F0.wireOp",EDGE,"E2.left"),sQuery(id+"F0.wireOp",EDGE,"E2.right"),sQuery(id+"F0.wireOp",EDGE,"E3"),sQuery(id+"F0.wireOp",EDGE,"E5.MirrorCS"),sQuery(id+"F0.wireOp",EDGE,"E7.MirrorC"),sQuery(id+"F0.wireOp",EDGE,"E8"),sQuery(id+"F0.wireOp",EDGE,"E10.bottom"),sQuery(id+"F0.wireOp",EDGE,"E10.top"),sQuery(id+"F0.wireOp",EDGE,"E13"),sQuery(id+"F0.wireOp",EDGE,"E15.MirrorC"),sQuery(id+"F0.wireOp",EDGE,"E28"),sQuery(id+"F0.wireOp",EDGE,"E29"),sQuery(id+"F0.wireOp",EDGE,"E31.MirrorCS"),sQuery(id+"F0.wireOp",EDGE,"E32.MirrorCS"),sQuery(id+"F0.wireOp",EDGE,"E34"),sQuery(id+"F0.wireOp",EDGE,"E37.MirrorCS"),sQuery(id+"F0.wireOp",EDGE,"E38"),sQuery(id+"F0.wireOp",EDGE,"E39"),sQuery(id+"F0.wireOp",EDGE,"E40"),sQuery(id+"F0.wireOp",EDGE,"E41.MirrorCS"),sQuery(id+"F0.wireOp",EDGE,"E42.MirrorCS"),sQuery(id+"F0.wireOp",EDGE,"E43.MirrorCS"),sQuery(id+"F0.wireOp",EDGE,"E44"),sQuery(id+"F0.wireOp",EDGE,"E45.MirrorCS"),sQuery(id+"F0.wireOp",EDGE,"E51"),sQuery(id+"F0.wireOp",EDGE,"E52.MirrorCS"),sQuery(id+"F0.wireOp",EDGE,"E54"),sQuery(id+"F0.wireOp",EDGE,"E55.MirrorCS"),sQuery(id+"F0.wireOp",EDGE,"E66"),sQuery(id+"F0.wireOp",EDGE,"E67.MirrorC"),sQuery(id+"F0.wireOp",EDGE,"E68"),sQuery(id+"F0.wireOp",EDGE,"E250"),sQuery(id+"F0.wireOp",EDGE,"E268.bottom"),sQuery(id+"F0.wireOp",EDGE,"E268.left"),sQuery(id+"F0.wireOp",EDGE,"E268.right"),sQuery(id+"F0.wireOp",EDGE,"E269.MirrorCS"),sQuery(id+"F0.wireOp",EDGE,"E270"),sQuery(id+"F0.wireOp",EDGE,"E273"),sQuery(id+"F0.wireOp",EDGE,"E274"),sQuery(id+"F0.wireOp",EDGE,"E452"),sQuery(id+"F0.wireOp",EDGE,"E453.MirrorC"),sQuery(id+"F0.wireOp",EDGE,"E454")])],"isStart":false});
            var sketch = newSketch(context, id + "F18", { "sketchPlane" : qUnion([Q0])});
            skCircle(sketch, "E528.0", {"center": v(-122.66, 55.57) * mm, "radius": 1.5 * mm});
            skCircle(sketch, "E529.0", {"center": v(-105.16, 55.57) * mm, "radius": 1.5 * mm});
            skCircle(sketch, "E530.0", {"center": v(-94.79, 23.27) * mm, "radius": 2.25 * mm});
            skCircle(sketch, "E531", {"center": v(-122.66, 55.57) * mm, "radius": 4.5 * mm});
            skCircle(sketch, "E532", {"center": v(-105.16, 55.57) * mm, "radius": 4.5 * mm});
            skCircle(sketch, "E533", {"center": v(-94.79, 23.27) * mm, "radius": 5.25 * mm});
            skLineSegment(sketch, "E534", {"start": v(-122.66, 60.07) * mm, "end": v(-105.16, 60.07) * mm});
            skLineSegment(sketch, "E535", {"start": v(-89.82, 24.98) * mm, "end": v(-100.9, 57.04) * mm});
            skLineSegment(sketch, "E536", {"start": v(-126.12, 52.7) * mm, "end": v(-98.82, 19.9) * mm});
            skSolve(sketch);
        }
        {
            var Q0;
            {var subQ24=sQuery(id+"F18.wireOp",EDGE,"E534");Q0=makeQuery(id+"F18.imprint","IMPRINT",FACE,{"disambiguationData":[TD([[makeQuery(id+"F18.imprint","IMPRINT",EDGE,{"derivedFrom":subQ24}),-1.0]])]});}
            var Q1;
            {var subQ2=sQuery(id+"F0.wireOp",EDGE,"E5.MirrorCS");Q1=makeQuery(id+"F18.imprint","IMPRINT",FACE,{"disambiguationData":[TD([[makeQuery(id+"F18.imprint","IMPRINT",EDGE,{"derivedFrom":makeQuery(id+"F1.opExtrude","CAP_EDGE",EDGE,{"disambiguationData":[OSD([subQ2])],"isStart":false})}),-1.0]])]});}
            var Q2;
            Q2=makeQuery(id+"F18.imprint","IMPRINT",FACE,{"disambiguationData":[TD([[makeQuery(id+"F18.imprint","IMPRINT",EDGE,{"derivedFrom":sQuery(id+"F18.wireOp",EDGE,"E529.0")}),-1.0]])]});
            var Q3;
            Q3=makeQuery(id+"F18.imprint","IMPRINT",FACE,{"disambiguationData":[TD([[makeQuery(id+"F18.imprint","IMPRINT",EDGE,{"derivedFrom":sQuery(id+"F18.wireOp",EDGE,"E528.0")}),1.0]])]});
            var Q4;
            Q4=makeQuery(id+"F18.imprint","IMPRINT",FACE,{"disambiguationData":[TD([[makeQuery(id+"F18.imprint","IMPRINT",EDGE,{"derivedFrom":sQuery(id+"F18.wireOp",EDGE,"E530.0")}),-1.0]])]});
            var Q5;
            {var subQ0=sQuery(id+"F18.wireOp",EDGE,"E536");var subQ1=sQuery(id+"F0.wireOp",EDGE,"E3");var subQ2=sQuery(id+"F0.wireOp",EDGE,"E0.top");var subQ3=makeQuery(id+"F2.opFillet","BLEND_EDGE",EDGE,{"blendedFrom":[makeQuery(id+"F1.opExtrude","SWEPT_EDGE",EDGE,{"disambiguationData":[OSD([subQ2,subQ1])]}),makeQuery(id+"F1.opExtrude","CAP_FACE",FACE,{"disambiguationData":[OSD([sQuery(id+"F0.wireOp",EDGE,"E0.bottom"),subQ2,sQuery(id+"F0.wireOp",EDGE,"E0.left"),sQuery(id+"F0.wireOp",EDGE,"E0.right"),sQuery(id+"F0.wireOp",EDGE,"E1"),sQuery(id+"F0.wireOp",EDGE,"E2.left"),sQuery(id+"F0.wireOp",EDGE,"E2.right"),subQ1,sQuery(id+"F0.wireOp",EDGE,"E5.MirrorCS"),sQuery(id+"F0.wireOp",EDGE,"E7.MirrorC"),sQuery(id+"F0.wireOp",EDGE,"E8"),sQuery(id+"F0.wireOp",EDGE,"E10.bottom"),sQuery(id+"F0.wireOp",EDGE,"E10.top"),sQuery(id+"F0.wireOp",EDGE,"E13"),sQuery(id+"F0.wireOp",EDGE,"E15.MirrorC"),sQuery(id+"F0.wireOp",EDGE,"E28"),sQuery(id+"F0.wireOp",EDGE,"E29"),sQuery(id+"F0.wireOp",EDGE,"E31.MirrorCS"),sQuery(id+"F0.wireOp",EDGE,"E32.MirrorCS"),sQuery(id+"F0.wireOp",EDGE,"E34"),sQuery(id+"F0.wireOp",EDGE,"E37.MirrorCS"),sQuery(id+"F0.wireOp",EDGE,"E38"),sQuery(id+"F0.wireOp",EDGE,"E39"),sQuery(id+"F0.wireOp",EDGE,"E40"),sQuery(id+"F0.wireOp",EDGE,"E41.MirrorCS"),sQuery(id+"F0.wireOp",EDGE,"E42.MirrorCS"),sQuery(id+"F0.wireOp",EDGE,"E43.MirrorCS"),sQuery(id+"F0.wireOp",EDGE,"E44"),sQuery(id+"F0.wireOp",EDGE,"E45.MirrorCS"),sQuery(id+"F0.wireOp",EDGE,"E51"),sQuery(id+"F0.wireOp",EDGE,"E52.MirrorCS"),sQuery(id+"F0.wireOp",EDGE,"E54"),sQuery(id+"F0.wireOp",EDGE,"E55.MirrorCS"),sQuery(id+"F0.wireOp",EDGE,"E66"),sQuery(id+"F0.wireOp",EDGE,"E67.MirrorC"),sQuery(id+"F0.wireOp",EDGE,"E68"),sQuery(id+"F0.wireOp",EDGE,"E250"),sQuery(id+"F0.wireOp",EDGE,"E268.bottom"),sQuery(id+"F0.wireOp",EDGE,"E268.left"),sQuery(id+"F0.wireOp",EDGE,"E268.right"),sQuery(id+"F0.wireOp",EDGE,"E269.MirrorCS"),sQuery(id+"F0.wireOp",EDGE,"E270"),sQuery(id+"F0.wireOp",EDGE,"E273"),sQuery(id+"F0.wireOp",EDGE,"E274"),sQuery(id+"F0.wireOp",EDGE,"E452"),sQuery(id+"F0.wireOp",EDGE,"E453.MirrorC"),sQuery(id+"F0.wireOp",EDGE,"E454")])],"isStart":false})],"blendedInto":[makeQuery(id+"F1.opExtrude","CAP_FACE",FACE,{"disambiguationData":[OSD([sQuery(id+"F0.wireOp",EDGE,"E0.bottom"),subQ2,sQuery(id+"F0.wireOp",EDGE,"E0.left"),sQuery(id+"F0.wireOp",EDGE,"E0.right"),sQuery(id+"F0.wireOp",EDGE,"E1"),sQuery(id+"F0.wireOp",EDGE,"E2.left"),sQuery(id+"F0.wireOp",EDGE,"E2.right"),subQ1,sQuery(id+"F0.wireOp",EDGE,"E5.MirrorCS"),sQuery(id+"F0.wireOp",EDGE,"E7.MirrorC"),sQuery(id+"F0.wireOp",EDGE,"E8"),sQuery(id+"F0.wireOp",EDGE,"E10.bottom"),sQuery(id+"F0.wireOp",EDGE,"E10.top"),sQuery(id+"F0.wireOp",EDGE,"E13"),sQuery(id+"F0.wireOp",EDGE,"E15.MirrorC"),sQuery(id+"F0.wireOp",EDGE,"E28"),sQuery(id+"F0.wireOp",EDGE,"E29"),sQuery(id+"F0.wireOp",EDGE,"E31.MirrorCS"),sQuery(id+"F0.wireOp",EDGE,"E32.MirrorCS"),sQuery(id+"F0.wireOp",EDGE,"E34"),sQuery(id+"F0.wireOp",EDGE,"E37.MirrorCS"),sQuery(id+"F0.wireOp",EDGE,"E38"),sQuery(id+"F0.wireOp",EDGE,"E39"),sQuery(id+"F0.wireOp",EDGE,"E40"),sQuery(id+"F0.wireOp",EDGE,"E41.MirrorCS"),sQuery(id+"F0.wireOp",EDGE,"E42.MirrorCS"),sQuery(id+"F0.wireOp",EDGE,"E43.MirrorCS"),sQuery(id+"F0.wireOp",EDGE,"E44"),sQuery(id+"F0.wireOp",EDGE,"E45.MirrorCS"),sQuery(id+"F0.wireOp",EDGE,"E51"),sQuery(id+"F0.wireOp",EDGE,"E52.MirrorCS"),sQuery(id+"F0.wireOp",EDGE,"E54"),sQuery(id+"F0.wireOp",EDGE,"E55.MirrorCS"),sQuery(id+"F0.wireOp",EDGE,"E66"),sQuery(id+"F0.wireOp",EDGE,"E67.MirrorC"),sQuery(id+"F0.wireOp",EDGE,"E68"),sQuery(id+"F0.wireOp",EDGE,"E250"),sQuery(id+"F0.wireOp",EDGE,"E268.bottom"),sQuery(id+"F0.wireOp",EDGE,"E268.left"),sQuery(id+"F0.wireOp",EDGE,"E268.right"),sQuery(id+"F0.wireOp",EDGE,"E269.MirrorCS"),sQuery(id+"F0.wireOp",EDGE,"E270"),sQuery(id+"F0.wireOp",EDGE,"E273"),sQuery(id+"F0.wireOp",EDGE,"E274"),sQuery(id+"F0.wireOp",EDGE,"E452"),sQuery(id+"F0.wireOp",EDGE,"E453.MirrorC"),sQuery(id+"F0.wireOp",EDGE,"E454")])],"isStart":false})]});var subQ4=makeQuery(id+"F18.imprint","INTERSECT",VERTEX,{"disambiguationData":[OD(0.0)],"derivedFrom":[subQ3,subQ0]});Q5=makeQuery(id+"F18.imprint","IMPRINT",FACE,{"disambiguationData":[TD([[makeQuery(id+"F18.imprint","IMPRINT",EDGE,{"disambiguationData":[TD([[subQ4,-1.0]])],"derivedFrom":subQ0}),1.0]])]});}
            extrude(context, id + "F19", {"entities" : qUnion([Q0, Q1, Q2, Q3, Q4, Q5]), "depth" : 5.08 * mm, "offsetDistance" : 25 * mm});
        }
    });
